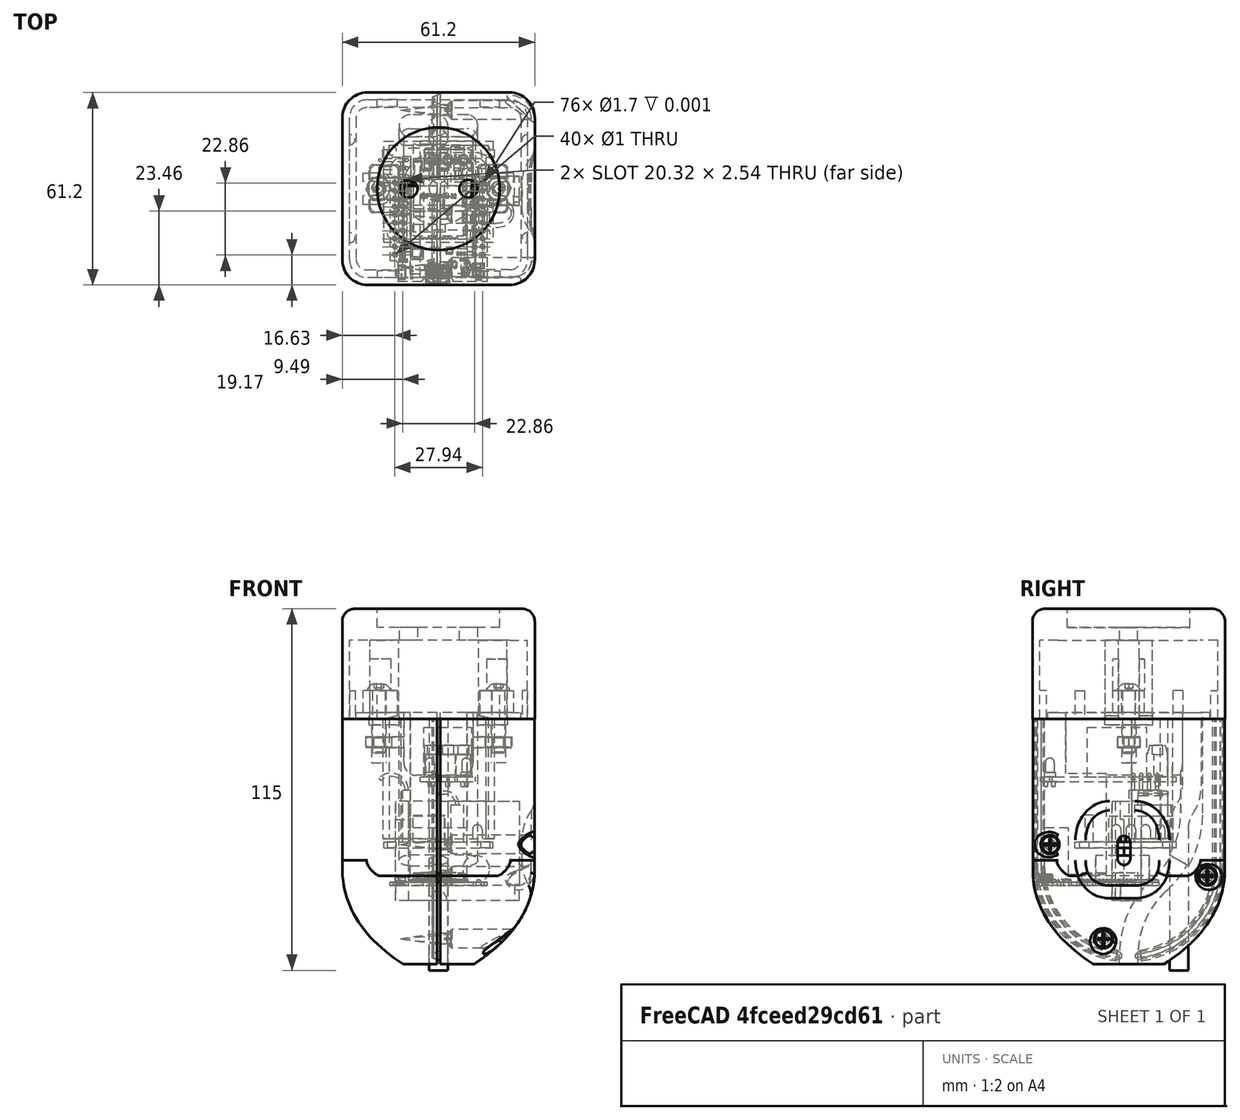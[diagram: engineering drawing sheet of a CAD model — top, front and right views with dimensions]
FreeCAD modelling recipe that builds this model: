
FCSTD DOCUMENT  (FreeCAD 1.0R39109 (Git))
Label: BedroomFan
License: All rights reserved
LicenseURL: http://en.wikipedia.org/wiki/All_rights_reserved
objects: Sketcher::SketchObject×104, PartDesign::Pocket×33, PartDesign::Body×22, PartDesign::Pad×17, PartDesign::Revolution×13, PartDesign::Groove×9, PartDesign::SubShapeBinder×9, PartDesign::Mirrored×8, PartDesign::SubtractivePipe×7, Part::Compound×5, PartDesign::Fillet×4, PartDesign::Plane×4, Part::FeaturePython×4, PartDesign::PolarPattern×3, PartDesign::AdditivePipe×3, PartDesign::SubtractiveLoft×2, PartDesign::LinearPattern×2, PartDesign::Point×2, Part::Feature×1, PartDesign::MultiTransform×1
note: 547 computed .brp shape members not serialized (recipe doc carries the construction recipe); baked Part::Feature solids carry a one-line shape summary decoded from their .brp

FEATURE [Part::Feature] Part__Feature  label="MH-ET_LIVE_MiniKit"
  shape: bbox 31.02 x 99.68 x 39.44 mm, 5494 faces, 23 solids (baked)
FEATURE [Sketcher::SketchObject] Sketch009
  ArcFitTolerance = 0
  AttachmentSupport = -> [XY_Plane001]
  FullyConstrained = true
  MakeInternals = false
  MapMode = 5
  sketch-geometry (8):
    g0: LineSegment StartX=0 StartY=8.8 StartZ=0 EndX=43.2 EndY=8.8 EndZ=0
    g1: LineSegment StartX=43.2 StartY=8.8 StartZ=0 EndX=43.2 EndY=-8.8 EndZ=0
    g2: LineSegment StartX=43.2 StartY=-8.8 StartZ=0 EndX=0 EndY=-8.8 EndZ=0
    g3: LineSegment StartX=0 StartY=-8.8 StartZ=0 EndX=0 EndY=8.8 EndZ=0
    g4: Circle CenterX=3.2 CenterY=2.54 CenterZ=0 NormalX=0 NormalY=0 NormalZ=1 AngleXU=0 Radius=0.4
    g5: Circle CenterX=3.2 CenterY=0 CenterZ=0 NormalX=0 NormalY=0 NormalZ=1 AngleXU=0 Radius=0.4
    g6: Circle CenterX=3.2 CenterY=-2.54 CenterZ=0 NormalX=0 NormalY=0 NormalZ=1 AngleXU=0 Radius=0.4
    g7: LineSegment [constr] StartX=3.2 StartY=2.54 StartZ=0 EndX=3.2 EndY=-2.54 EndZ=0
  constraints (21):
    c: Coincident(g0,g1)
    c: Coincident(g1,g2)
    c: Coincident(g2,g3)
    c: Coincident(g3,g0)
    c: Horizontal(g0)
    c: Horizontal(g2)
    c: Vertical(g3)
    c: PointOnObject(g0,g-2)
    c: Symmetric(g1,g0,g-1)
    c: DistanceY(g1,g1) = 17.6
    c: DistanceX(g0,g0) = 43.2
    c: PointOnObject(g5,g-1)
    c: Symmetric(g6,g4,g-1)
    c: Coincident(g7,g4)
    c: Coincident(g7,g6)
    c: PointOnObject(g5,g7)
    c: Equal(g6,g5)
    c: Equal(g5,g4)
    c: Radius(g4) = 0.4
    c: DistanceY(g7,g7) = 5.08
    c: DistanceX(g4) = 3.2
FEATURE [PartDesign::Pad] Pad006
  Direction = (0,0,1)
  Length = 1.6
  Length2 = 100
  Profile = -> Sketch009
  Suppressed = false
  Type = 0
FEATURE [PartDesign::Body] Body001  label="PCB"
  AllowCompound = false
  Group = -> [Sketch009,Pad006]
  Origin = -> Origin001
  Tip = -> Pad006
FEATURE [Sketcher::SketchObject] Sketch010
  ArcFitTolerance = 0
  AttachmentOffset = pos=(0,0,1.6) rot=(0,0,1;0rad)
  AttachmentSupport = -> [XY_Plane002]
  FullyConstrained = true
  MakeInternals = false
  MapMode = 5
  Placement = pos=(0,0,1.6) rot=(0,0,1;0rad)
  sketch-geometry (4):
    g0: LineSegment StartX=14.8 StartY=7.6 StartZ=0 EndX=33.8 EndY=7.6 EndZ=0
    g1: LineSegment StartX=33.8 StartY=7.6 StartZ=0 EndX=33.8 EndY=-7.6 EndZ=0
    g2: LineSegment StartX=33.8 StartY=-7.6 StartZ=0 EndX=14.8 EndY=-7.6 EndZ=0
    g3: LineSegment StartX=14.8 StartY=-7.6 StartZ=0 EndX=14.8 EndY=7.6 EndZ=0
  constraints (11):
    c: Coincident(g0,g1)
    c: Coincident(g1,g2)
    c: Coincident(g2,g3)
    c: Coincident(g3,g0)
    c: Horizontal(g0)
    c: Horizontal(g2)
    c: Vertical(g3)
    c: Symmetric(g1,g0,g-1)
    c: DistanceX(g0,g0) = 19
    c: DistanceY(g1,g1) = 15.2
    c: DistanceX(g0) = 14.8
FEATURE [PartDesign::Pad] Pad007
  Direction = (0,0,1)
  Length = 15.7
  Length2 = 100
  Profile = -> Sketch010
  Suppressed = false
  Type = 0
FEATURE [PartDesign::Body] Body002  label="JQC-3FF-S-Z"
  AllowCompound = false
  Group = -> [Sketch010,Pad007]
  Origin = -> Origin002
  Tip = -> Pad007
FEATURE [Sketcher::SketchObject] Sketch011
  ArcFitTolerance = 0
  AttachmentSupport = -> [XZ_Plane003]
  FullyConstrained = true
  MakeInternals = false
  MapMode = 5
  Placement = pos=(0,0,0) rot=(1,0,0;1.5708rad)
  sketch-geometry (7):
    g0: LineSegment StartX=34.6 StartY=11.6 StartZ=0 EndX=39.6 EndY=11.6 EndZ=0
    g1: LineSegment StartX=40.4 StartY=8.6 StartZ=0 EndX=40.4 EndY=1.6 EndZ=0
    g2: LineSegment StartX=40.4 StartY=1.6 StartZ=0 EndX=33.8 EndY=1.6 EndZ=0
    g3: LineSegment StartX=33.8 StartY=1.6 StartZ=0 EndX=33.8 EndY=8.6 EndZ=0
    g4: LineSegment StartX=34.6 StartY=11.6 StartZ=0 EndX=33.8 EndY=8.6 EndZ=0
    g5: LineSegment StartX=39.6 StartY=11.6 StartZ=0 EndX=40.4 EndY=8.6 EndZ=0
    g6: LineSegment [constr] StartX=37.1 StartY=11.6 StartZ=0 EndX=37.1 EndY=1.6 EndZ=0
  constraints (19):
    c: Coincident(g1,g2)
    c: Coincident(g2,g3)
    c: Horizontal(g0)
    c: Vertical(g1)
    c: DistanceY(g1) = 1.6
    c: Coincident(g3,g4)
    c: Coincident(g4,g0)
    c: Coincident(g0,g5)
    c: Coincident(g1,g5)
    c: PointOnObject(g6,g0)
    c: PointOnObject(g6,g2)
    c: Symmetric(g1,g2,g6)
    c: Symmetric(g1,g3,g6)
    c: Symmetric(g0,g0,g6)
    c: DistanceX(g2) = 33.8
    c: DistanceX(g0,g0) = 5
    c: DistanceY(g1,g0) = 10
    c: DistanceY(g1,g1) = 7
    c: DistanceX(g1) = 40.4
FEATURE [PartDesign::Pad] Pad008
  Direction = (0,-1,2e-16)
  Length = 15
  Length2 = 100
  Midplane = true
  Placement = pos=(0,0,0) rot=(1,0,0;1.5708rad)
  Profile = -> Sketch011
  Suppressed = false
  Type = 0
FEATURE [Sketcher::SketchObject] Sketch012
  ArcFitTolerance = 0
  AttachmentOffset = pos=(0,0,36) rot=(0,0,1;0rad)
  AttachmentSupport = -> [YZ_Plane003]
  FullyConstrained = true
  MakeInternals = false
  MapMode = 5
  Placement = pos=(36,0,0) rot=(0.57735,0.57735,0.57735;2.0944rad)
  sketch-geometry (16):
    g0: LineSegment StartX=-7.05 StartY=8.6 StartZ=0 EndX=-2.65 EndY=8.6 EndZ=0
    g1: LineSegment StartX=-2.65 StartY=8.6 StartZ=0 EndX=-2.65 EndY=2.1 EndZ=0
    g2: LineSegment StartX=-2.65 StartY=2.1 StartZ=0 EndX=-7.05 EndY=2.1 EndZ=0
    g3: LineSegment StartX=-7.05 StartY=2.1 StartZ=0 EndX=-7.05 EndY=8.6 EndZ=0
    g4: LineSegment [constr] StartX=-7.05 StartY=8.6 StartZ=0 EndX=-7.5 EndY=8.6 EndZ=0
    g5: LineSegment [constr] StartX=-2.2 StartY=8.6 StartZ=0 EndX=-2.65 EndY=8.6 EndZ=0
    g6: LineSegment StartX=-2.2 StartY=8.6 StartZ=0 EndX=2.2 EndY=8.6 EndZ=0
    g7: LineSegment StartX=2.2 StartY=8.6 StartZ=0 EndX=2.2 EndY=2.1 EndZ=0
    g8: LineSegment StartX=2.2 StartY=2.1 StartZ=0 EndX=-2.2 EndY=2.1 EndZ=0
    g9: LineSegment StartX=-2.2 StartY=2.1 StartZ=0 EndX=-2.2 EndY=8.6 EndZ=0
    g10: LineSegment StartX=2.65 StartY=8.6 StartZ=0 EndX=7.05 EndY=8.6 EndZ=0
    g11: LineSegment StartX=7.05 StartY=8.6 StartZ=0 EndX=7.05 EndY=2.1 EndZ=0
    g12: LineSegment StartX=7.05 StartY=2.1 StartZ=0 EndX=2.65 EndY=2.1 EndZ=0
    g13: LineSegment StartX=2.65 StartY=2.1 StartZ=0 EndX=2.65 EndY=8.6 EndZ=0
    g14: LineSegment [constr] StartX=2.65 StartY=8.6 StartZ=0 EndX=2.2 EndY=8.6 EndZ=0
    g15: LineSegment [constr] StartX=7.05 StartY=8.6 StartZ=0 EndX=7.5 EndY=8.6 EndZ=0
  constraints (45):
    c: Coincident(g0,g1)
    c: Coincident(g1,g2)
    c: Coincident(g2,g3)
    c: Coincident(g3,g0)
    c: Horizontal(g0)
    c: Horizontal(g2)
    c: Vertical(g1)
    c: Vertical(g3)
    c: DistanceX(g0,g0) = 4.4
    c: DistanceY(g0) = 8.6
    c: DistanceY(g3,g3) = 6.5
    c: Coincident(g4,g0)
    c: Horizontal(g4)
    c: Coincident(g5,g0)
    c: Equal(g5,g4)
    c: Horizontal(g5)
    c: Coincident(g6,g7)
    c: Coincident(g7,g8)
    c: Coincident(g8,g9)
    c: Coincident(g9,g6)
    c: Horizontal(g6)
    c: Horizontal(g8)
    c: Vertical(g7)
    c: Vertical(g9)
    c: Coincident(g6,g5)
    c: Coincident(g10,g11)
    c: Coincident(g11,g12)
    c: Coincident(g12,g13)
    c: Coincident(g13,g10)
    c: Horizontal(g10)
    c: Horizontal(g12)
    c: Vertical(g11)
    c: Vertical(g13)
    c: Coincident(g14,g10)
    c: Coincident(g14,g6)
    c: Horizontal(g14)
    c: Coincident(g15,g10)
    c: Equal(g15,g14)
    c: Equal(g14,g5)
    c: DistanceX(g4,g15) = 15
    c: Equal(g0,g6)
    c: Equal(g6,g10)
    c: Symmetric(g4,g15,g-2)
    c: Equal(g1,g9)
    c: Equal(g9,g13)
FEATURE [PartDesign::Pocket] Pocket
  BaseFeature = -> Pad008
  Direction = (-1,0,0)
  Length = 5
  Length2 = 100
  Placement = pos=(0,0,0) rot=(1,0,0;1.5708rad)
  Profile = -> Sketch012
  Reversed = true
  Suppressed = false
  Type = 1
FEATURE [Sketcher::SketchObject] Sketch013
  ArcFitTolerance = 0
  AttachmentOffset = pos=(0,0,8.6) rot=(0,0,1;0rad)
  AttachmentSupport = -> [XY_Plane003]
  ExternalGeometry = -> [Pocket]
  FullyConstrained = true
  MakeInternals = false
  MapMode = 5
  Placement = pos=(0,0,8.6) rot=(0,0,1;0rad)
  sketch-geometry (5):
    g0: Circle CenterX=37.1 CenterY=-4.85 CenterZ=0 NormalX=0 NormalY=0 NormalZ=1 AngleXU=0 Radius=1.75
    g1: LineSegment [constr] StartX=37.1 StartY=-2.65 StartZ=0 EndX=37.1 EndY=-7.05 EndZ=0
    g2: LineSegment [constr] StartX=38.85 StartY=-4.85 StartZ=0 EndX=35.35 EndY=-4.85 EndZ=0
    g3: Circle CenterX=37.1 CenterY=4.85 CenterZ=0 NormalX=0 NormalY=0 NormalZ=1 AngleXU=0 Radius=1.75
    g4: Circle CenterX=37.1 CenterY=0 CenterZ=0 NormalX=0 NormalY=0 NormalZ=1 AngleXU=0 Radius=1.75
  constraints (14):
    c: PointOnObject(g1,g-3)
    c: PointOnObject(g1,g-4)
    c: PointOnObject(g2,g0)
    c: PointOnObject(g2,g0)
    c: PointOnObject(g0,g1)
    c: PointOnObject(g0,g2)
    c: Symmetric(g-3,g-4,g2)
    c: Radius(g0) = 1.75
    c: Symmetric(g-5,g-6,g1)
    c: PointOnObject(g4,g-1)
    c: Symmetric(g3,g0,g-1)
    c: PointOnObject(g4,g1)
    c: Equal(g0,g4)
    c: Equal(g4,g3)
FEATURE [PartDesign::Pocket] Pocket001
  BaseFeature = -> Pocket
  Direction = (0,0,-1)
  Length = 5
  Length2 = 100
  Placement = pos=(0,0,0) rot=(1,0,0;1.5708rad)
  Profile = -> Sketch013
  Reversed = true
  Suppressed = false
  Type = 1
FEATURE [PartDesign::Body] Body003  label="Connectors"
  AllowCompound = false
  Group = -> [Sketch011,Pad008,Sketch012,Pocket,Sketch013,Pocket001]
  Origin = -> Origin003
  Tip = -> Pocket001
FEATURE [Sketcher::SketchObject] Sketch014
  ArcFitTolerance = 0
  AttachmentOffset = pos=(0,0,2.9) rot=(0,0,1;0rad)
  AttachmentSupport = -> [YZ_Plane004]
  FullyConstrained = true
  MakeInternals = false
  MapMode = 5
  Placement = pos=(2.9,0,0) rot=(0.57735,0.57735,0.57735;2.0944rad)
  sketch-geometry (6):
    g0: ArcOfCircle CenterX=0 CenterY=6.05 CenterZ=0 NormalX=0 NormalY=0 NormalZ=1 AngleXU=0 Radius=1.45 StartAngle=1.5708 EndAngle=3.14159
    g1: LineSegment StartX=-1.45 StartY=6.05 StartZ=0 EndX=-1.45 EndY=3 EndZ=0
    g2: LineSegment StartX=-1.45 StartY=3 StartZ=0 EndX=-1.75 EndY=3 EndZ=0
    g3: LineSegment StartX=-1.75 StartY=3 StartZ=0 EndX=-1.75 EndY=1.6 EndZ=0
    g4: LineSegment StartX=-1.75 StartY=1.6 StartZ=0 EndX=0 EndY=1.6 EndZ=0
    g5: LineSegment StartX=0 StartY=1.6 StartZ=0 EndX=0 EndY=7.5 EndZ=0
  constraints (18):
    c: Vertical(g1)
    c: Coincident(g1,g2)
    c: Coincident(g2,g3)
    c: Coincident(g3,g4)
    c: Horizontal(g4)
    c: Coincident(g4,g5)
    c: Coincident(g5,g0)
    c: Vertical(g5)
    c: Tangent(g0,g1) = -1.5708
    c: PointOnObject(g0,g5)
    c: Horizontal(g2)
    c: Vertical(g3)
    c: DistanceY(g3) = 1.6
    c: DistanceY(g0) = 7.5
    c: DistanceX(g0,g0) = 1.45
    c: DistanceX(g4,g4) = 1.75
    c: DistanceY(g2) = 3
    c: PointOnObject(g4,g-2)
FEATURE [PartDesign::Revolution] Revolution001
  Angle = 360
  Angle2 = 60
  Axis = (0,0,1)
  Base = (2.9,0,0)
  Placement = pos=(0,0,0) rot=(0.57735,0.57735,0.57735;2.0944rad)
  Profile = -> Sketch014
  ReferenceAxis = -> Sketch014 [V_Axis]
  Suppressed = false
  Type = 0
FEATURE [PartDesign::Body] Body004  label="LEDgreen"
  AllowCompound = false
  Group = -> [Sketch014,Revolution001]
  Origin = -> Origin004
  Placement = pos=(0,5.8,0) rot=(0,0,1;0rad)
  Tip = -> Revolution001
FEATURE [Sketcher::SketchObject] Sketch015
  ArcFitTolerance = 0
  AttachmentOffset = pos=(0,0,2.9) rot=(0,0,1;0rad)
  AttachmentSupport = -> [YZ_Plane004]
  FullyConstrained = true
  MakeInternals = false
  MapMode = 5
  Placement = pos=(2.9,0,0) rot=(0.57735,0.57735,0.57735;2.0944rad)
  sketch-geometry (6):
    g0: ArcOfCircle CenterX=0 CenterY=6.05 CenterZ=0 NormalX=0 NormalY=0 NormalZ=1 AngleXU=0 Radius=1.45 StartAngle=1.5708 EndAngle=3.14159
    g1: LineSegment StartX=-1.45 StartY=6.05 StartZ=0 EndX=-1.45 EndY=3 EndZ=0
    g2: LineSegment StartX=-1.45 StartY=3 StartZ=0 EndX=-1.75 EndY=3 EndZ=0
    g3: LineSegment StartX=-1.75 StartY=3 StartZ=0 EndX=-1.75 EndY=1.6 EndZ=0
    g4: LineSegment StartX=-1.75 StartY=1.6 StartZ=0 EndX=0 EndY=1.6 EndZ=0
    g5: LineSegment StartX=1e-16 StartY=1.6 StartZ=0 EndX=1e-16 EndY=7.5 EndZ=0
  constraints (18):
    c: Vertical(g1)
    c: Coincident(g1,g2)
    c: Coincident(g2,g3)
    c: Coincident(g3,g4)
    c: Horizontal(g4)
    c: Coincident(g4,g5)
    c: Coincident(g5,g0)
    c: Vertical(g5)
    c: Tangent(g0,g1) = -1.5708
    c: PointOnObject(g0,g5)
    c: Horizontal(g2)
    c: Vertical(g3)
    c: DistanceY(g3) = 1.6
    c: DistanceY(g0) = 7.5
    c: DistanceX(g0,g0) = 1.45
    c: DistanceX(g4,g4) = 1.75
    c: DistanceY(g2) = 3
    c: PointOnObject(g4,g-2)
FEATURE [PartDesign::Revolution] Revolution002
  Angle = 360
  Angle2 = 60
  Axis = (0,0,1)
  Base = (2.9,0,0)
  Placement = pos=(0,0,0) rot=(0.57735,0.57735,0.57735;2.0944rad)
  Profile = -> Sketch015
  ReferenceAxis = -> Sketch015 [V_Axis]
  Suppressed = false
  Type = 0
FEATURE [PartDesign::Body] Body005  label="LEDred"
  AllowCompound = false
  Group = -> [Sketch015,Revolution002]
  Origin = -> Origin005
  Placement = pos=(0,-5.8,0) rot=(0,0,1;0rad)
  Tip = -> Revolution002
FEATURE [Sketcher::SketchObject] Sketch016
  ArcFitTolerance = 0
  AttachmentSupport = -> [YZ_Plane006]
  FullyConstrained = true
  MakeInternals = false
  MapMode = 5
  Placement = pos=(0,0,0) rot=(0.57735,0.57735,0.57735;2.0944rad)
  sketch-geometry (5):
    g0: LineSegment StartX=1.2 StartY=0 StartZ=0 EndX=0 EndY=0 EndZ=0
    g1: LineSegment StartX=0 StartY=0 StartZ=0 EndX=0 EndY=-1.5 EndZ=0
    g2: LineSegment StartX=0 StartY=-1.5 StartZ=0 EndX=0.6 EndY=-1.5 EndZ=0
    g3: LineSegment StartX=0.6 StartY=-1.5 StartZ=0 EndX=0.6 EndY=-0.6 EndZ=0
    g4: ArcOfCircle CenterX=1.2 CenterY=-0.6 CenterZ=0 NormalX=0 NormalY=0 NormalZ=1 AngleXU=0 Radius=0.6 StartAngle=1.5708 EndAngle=3.14159
  constraints (13):
    c: PointOnObject(g0,g-1)
    c: Coincident(g0,g-1)
    c: Coincident(g0,g1)
    c: PointOnObject(g1,g-2)
    c: Coincident(g1,g2)
    c: Horizontal(g2)
    c: Coincident(g2,g3)
    c: Vertical(g3)
    c: Tangent(g0,g4) = -1.5708
    c: Tangent(g3,g4) = 1.5708
    c: DistanceX(g2,g2) = 0.6
    c: DistanceY(g1,g1) = 1.5
    c: Radius(g4) = 0.6
FEATURE [PartDesign::Revolution] Revolution003
  Angle = 360
  Angle2 = 60
  Axis = (0,0,1)
  Base = (0,0,0)
  Placement = pos=(0,0,0) rot=(0.57735,0.57735,0.57735;2.0944rad)
  Profile = -> Sketch016
  ReferenceAxis = -> Sketch016 [V_Axis]
  Reversed = true
  Suppressed = false
  Type = 0
FEATURE [PartDesign::Body] Body006  label="Pin001"
  AllowCompound = false
  Group = -> [Sketch016,Revolution003]
  Origin = -> Origin006
  Placement = pos=(1.7,5.7,0) rot=(0,0,1;0rad)
  Tip = -> Revolution003
FEATURE [Sketcher::SketchObject] Sketch017
  ArcFitTolerance = 0
  AttachmentSupport = -> [YZ_Plane006]
  FullyConstrained = true
  MakeInternals = false
  MapMode = 5
  Placement = pos=(0,0,0) rot=(0.57735,0.57735,0.57735;2.0944rad)
  sketch-geometry (5):
    g0: LineSegment StartX=1.2 StartY=0 StartZ=0 EndX=0 EndY=0 EndZ=0
    g1: LineSegment StartX=0 StartY=0 StartZ=0 EndX=0 EndY=-1.5 EndZ=0
    g2: LineSegment StartX=0 StartY=-1.5 StartZ=0 EndX=0.6 EndY=-1.5 EndZ=0
    g3: LineSegment StartX=0.6 StartY=-1.5 StartZ=0 EndX=0.6 EndY=-0.6 EndZ=0
    g4: ArcOfCircle CenterX=1.2 CenterY=-0.6 CenterZ=0 NormalX=0 NormalY=0 NormalZ=1 AngleXU=0 Radius=0.6 StartAngle=1.5708 EndAngle=3.14159
  constraints (13):
    c: PointOnObject(g0,g-1)
    c: Coincident(g0,g-1)
    c: Coincident(g0,g1)
    c: PointOnObject(g1,g-2)
    c: Coincident(g1,g2)
    c: Horizontal(g2)
    c: Coincident(g2,g3)
    c: Vertical(g3)
    c: Tangent(g0,g4) = -1.5708
    c: Tangent(g3,g4) = 1.5708
    c: DistanceX(g2,g2) = 0.6
    c: DistanceY(g1,g1) = 1.5
    c: Radius(g4) = 0.6
FEATURE [PartDesign::Revolution] Revolution004
  Angle = 360
  Angle2 = 60
  Axis = (0,0,1)
  Base = (0,0,0)
  Placement = pos=(0,0,0) rot=(0.57735,0.57735,0.57735;2.0944rad)
  Profile = -> Sketch017
  ReferenceAxis = -> Sketch017 [V_Axis]
  Reversed = true
  Suppressed = false
  Type = 0
FEATURE [PartDesign::Body] Body007  label="Pin002"
  AllowCompound = false
  Group = -> [Sketch017,Revolution004]
  Origin = -> Origin007
  Placement = pos=(4.1,5.7,0) rot=(0,0,1;0rad)
  Tip = -> Revolution004
FEATURE [Sketcher::SketchObject] Sketch018
  ArcFitTolerance = 0
  AttachmentSupport = -> [YZ_Plane006]
  FullyConstrained = true
  MakeInternals = false
  MapMode = 5
  Placement = pos=(0,0,0) rot=(0.57735,0.57735,0.57735;2.0944rad)
  sketch-geometry (5):
    g0: LineSegment StartX=1.2 StartY=0 StartZ=0 EndX=0 EndY=0 EndZ=0
    g1: LineSegment StartX=0 StartY=0 StartZ=0 EndX=0 EndY=-1.5 EndZ=0
    g2: LineSegment StartX=0 StartY=-1.5 StartZ=0 EndX=0.6 EndY=-1.5 EndZ=0
    g3: LineSegment StartX=0.6 StartY=-1.5 StartZ=0 EndX=0.6 EndY=-0.6 EndZ=0
    g4: ArcOfCircle CenterX=1.2 CenterY=-0.6 CenterZ=0 NormalX=0 NormalY=0 NormalZ=1 AngleXU=0 Radius=0.6 StartAngle=1.5708 EndAngle=3.14159
  constraints (13):
    c: PointOnObject(g0,g-1)
    c: Coincident(g0,g-1)
    c: Coincident(g0,g1)
    c: PointOnObject(g1,g-2)
    c: Coincident(g1,g2)
    c: Horizontal(g2)
    c: Coincident(g2,g3)
    c: Vertical(g3)
    c: Tangent(g0,g4) = -1.5708
    c: Tangent(g3,g4) = 1.5708
    c: DistanceX(g2,g2) = 0.6
    c: DistanceY(g1,g1) = 1.5
    c: Radius(g4) = 0.6
FEATURE [PartDesign::Revolution] Revolution005
  Angle = 360
  Angle2 = 60
  Axis = (0,0,1)
  Base = (0,0,0)
  Placement = pos=(0,0,0) rot=(0.57735,0.57735,0.57735;2.0944rad)
  Profile = -> Sketch018
  ReferenceAxis = -> Sketch018 [V_Axis]
  Reversed = true
  Suppressed = false
  Type = 0
FEATURE [PartDesign::Body] Body008  label="Pin003"
  AllowCompound = false
  Group = -> [Sketch018,Revolution005]
  Origin = -> Origin008
  Placement = pos=(4.1,-5.9,0) rot=(0,0,1;0rad)
  Tip = -> Revolution005
FEATURE [Sketcher::SketchObject] Sketch019
  ArcFitTolerance = 0
  AttachmentSupport = -> [YZ_Plane006]
  FullyConstrained = true
  MakeInternals = false
  MapMode = 5
  Placement = pos=(0,0,0) rot=(0.57735,0.57735,0.57735;2.0944rad)
  sketch-geometry (5):
    g0: LineSegment StartX=1.2 StartY=0 StartZ=0 EndX=0 EndY=0 EndZ=0
    g1: LineSegment StartX=0 StartY=0 StartZ=0 EndX=0 EndY=-1.5 EndZ=0
    g2: LineSegment StartX=0 StartY=-1.5 StartZ=0 EndX=0.6 EndY=-1.5 EndZ=0
    g3: LineSegment StartX=0.6 StartY=-1.5 StartZ=0 EndX=0.6 EndY=-0.6 EndZ=0
    g4: ArcOfCircle CenterX=1.2 CenterY=-0.6 CenterZ=0 NormalX=0 NormalY=0 NormalZ=1 AngleXU=0 Radius=0.6 StartAngle=1.5708 EndAngle=3.14159
  constraints (13):
    c: PointOnObject(g0,g-1)
    c: Coincident(g0,g-1)
    c: Coincident(g0,g1)
    c: PointOnObject(g1,g-2)
    c: Coincident(g1,g2)
    c: Horizontal(g2)
    c: Coincident(g2,g3)
    c: Vertical(g3)
    c: Tangent(g0,g4) = -1.5708
    c: Tangent(g3,g4) = 1.5708
    c: DistanceX(g2,g2) = 0.6
    c: DistanceY(g1,g1) = 1.5
    c: Radius(g4) = 0.6
FEATURE [PartDesign::Revolution] Revolution006
  Angle = 360
  Angle2 = 60
  Axis = (0,0,1)
  Base = (0,0,0)
  Placement = pos=(0,0,0) rot=(0.57735,0.57735,0.57735;2.0944rad)
  Profile = -> Sketch019
  ReferenceAxis = -> Sketch019 [V_Axis]
  Reversed = true
  Suppressed = false
  Type = 0
FEATURE [PartDesign::Body] Body009  label="Pin004"
  AllowCompound = false
  Group = -> [Sketch019,Revolution006]
  Origin = -> Origin009
  Placement = pos=(1.7,-5.9,0) rot=(0,0,1;0rad)
  Tip = -> Revolution006
FEATURE [Sketcher::SketchObject] Sketch020
  ArcFitTolerance = 0
  AttachmentSupport = -> [YZ_Plane006]
  FullyConstrained = true
  MakeInternals = false
  MapMode = 5
  Placement = pos=(0,0,0) rot=(0.57735,0.57735,0.57735;2.0944rad)
  sketch-geometry (5):
    g0: LineSegment StartX=1.2 StartY=0 StartZ=0 EndX=0 EndY=0 EndZ=0
    g1: LineSegment StartX=0 StartY=0 StartZ=0 EndX=0 EndY=-1.5 EndZ=0
    g2: LineSegment StartX=0 StartY=-1.5 StartZ=0 EndX=0.6 EndY=-1.5 EndZ=0
    g3: LineSegment StartX=0.6 StartY=-1.5 StartZ=0 EndX=0.6 EndY=-0.6 EndZ=0
    g4: ArcOfCircle CenterX=1.2 CenterY=-0.6 CenterZ=0 NormalX=0 NormalY=0 NormalZ=1 AngleXU=0 Radius=0.6 StartAngle=1.5708 EndAngle=3.14159
  constraints (13):
    c: PointOnObject(g0,g-1)
    c: Coincident(g0,g-1)
    c: Coincident(g0,g1)
    c: PointOnObject(g1,g-2)
    c: Coincident(g1,g2)
    c: Horizontal(g2)
    c: Coincident(g2,g3)
    c: Vertical(g3)
    c: Tangent(g0,g4) = -1.5708
    c: Tangent(g3,g4) = 1.5708
    c: DistanceX(g2,g2) = 0.6
    c: DistanceY(g1,g1) = 1.5
    c: Radius(g4) = 0.6
FEATURE [PartDesign::Revolution] Revolution007
  Angle = 360
  Angle2 = 60
  Axis = (0,0,1)
  Base = (0,0,0)
  Placement = pos=(0,0,0) rot=(0.57735,0.57735,0.57735;2.0944rad)
  Profile = -> Sketch020
  ReferenceAxis = -> Sketch020 [V_Axis]
  Reversed = true
  Suppressed = false
  Type = 0
FEATURE [PartDesign::Body] Body010  label="Pin005"
  AllowCompound = false
  Group = -> [Sketch020,Revolution007]
  Origin = -> Origin010
  Placement = pos=(37.1,-4.8,0) rot=(0,0,1;0rad)
  Tip = -> Revolution007
FEATURE [Sketcher::SketchObject] Sketch021
  ArcFitTolerance = 0
  AttachmentSupport = -> [YZ_Plane006]
  FullyConstrained = true
  MakeInternals = false
  MapMode = 5
  Placement = pos=(0,0,0) rot=(0.57735,0.57735,0.57735;2.0944rad)
  sketch-geometry (5):
    g0: LineSegment StartX=1.2 StartY=0 StartZ=0 EndX=0 EndY=0 EndZ=0
    g1: LineSegment StartX=0 StartY=0 StartZ=0 EndX=0 EndY=-1.5 EndZ=0
    g2: LineSegment StartX=0 StartY=-1.5 StartZ=0 EndX=0.6 EndY=-1.5 EndZ=0
    g3: LineSegment StartX=0.6 StartY=-1.5 StartZ=0 EndX=0.6 EndY=-0.6 EndZ=0
    g4: ArcOfCircle CenterX=1.2 CenterY=-0.6 CenterZ=0 NormalX=0 NormalY=0 NormalZ=1 AngleXU=0 Radius=0.6 StartAngle=1.5708 EndAngle=3.14159
  constraints (13):
    c: PointOnObject(g0,g-1)
    c: Coincident(g0,g-1)
    c: Coincident(g0,g1)
    c: PointOnObject(g1,g-2)
    c: Coincident(g1,g2)
    c: Horizontal(g2)
    c: Coincident(g2,g3)
    c: Vertical(g3)
    c: Tangent(g0,g4) = -1.5708
    c: Tangent(g3,g4) = 1.5708
    c: DistanceX(g2,g2) = 0.6
    c: DistanceY(g1,g1) = 1.5
    c: Radius(g4) = 0.6
FEATURE [PartDesign::Revolution] Revolution008
  Angle = 360
  Angle2 = 60
  Axis = (0,0,1)
  Base = (0,0,0)
  Placement = pos=(0,0,0) rot=(0.57735,0.57735,0.57735;2.0944rad)
  Profile = -> Sketch021
  ReferenceAxis = -> Sketch021 [V_Axis]
  Reversed = true
  Suppressed = false
  Type = 0
FEATURE [PartDesign::Body] Body011  label="Pin006"
  AllowCompound = false
  Group = -> [Sketch021,Revolution008]
  Origin = -> Origin011
  Placement = pos=(37.1,9e-16,0) rot=(0,0,1;0rad)
  Tip = -> Revolution008
FEATURE [Sketcher::SketchObject] Sketch022
  ArcFitTolerance = 0
  AttachmentSupport = -> [YZ_Plane006]
  FullyConstrained = true
  MakeInternals = false
  MapMode = 5
  Placement = pos=(0,0,0) rot=(0.57735,0.57735,0.57735;2.0944rad)
  sketch-geometry (5):
    g0: LineSegment StartX=1.2 StartY=0 StartZ=0 EndX=0 EndY=0 EndZ=0
    g1: LineSegment StartX=0 StartY=0 StartZ=0 EndX=0 EndY=-1.5 EndZ=0
    g2: LineSegment StartX=0 StartY=-1.5 StartZ=0 EndX=0.6 EndY=-1.5 EndZ=0
    g3: LineSegment StartX=0.6 StartY=-1.5 StartZ=0 EndX=0.6 EndY=-0.6 EndZ=0
    g4: ArcOfCircle CenterX=1.2 CenterY=-0.6 CenterZ=0 NormalX=0 NormalY=0 NormalZ=1 AngleXU=0 Radius=0.6 StartAngle=1.5708 EndAngle=3.14159
  constraints (13):
    c: PointOnObject(g0,g-1)
    c: Coincident(g0,g-1)
    c: Coincident(g0,g1)
    c: PointOnObject(g1,g-2)
    c: Coincident(g1,g2)
    c: Horizontal(g2)
    c: Coincident(g2,g3)
    c: Vertical(g3)
    c: Tangent(g0,g4) = -1.5708
    c: Tangent(g3,g4) = 1.5708
    c: DistanceX(g2,g2) = 0.6
    c: DistanceY(g1,g1) = 1.5
    c: Radius(g4) = 0.6
FEATURE [PartDesign::Revolution] Revolution009
  Angle = 360
  Angle2 = 60
  Axis = (0,0,1)
  Base = (0,0,0)
  Placement = pos=(0,0,0) rot=(0.57735,0.57735,0.57735;2.0944rad)
  Profile = -> Sketch022
  ReferenceAxis = -> Sketch022 [V_Axis]
  Reversed = true
  Suppressed = false
  Type = 0
FEATURE [PartDesign::Body] Body012  label="Pin007"
  AllowCompound = false
  Group = -> [Sketch022,Revolution009]
  Origin = -> Origin012
  Placement = pos=(37.1,4.8,0) rot=(0,0,1;0rad)
  Tip = -> Revolution009
FEATURE [Part::Compound] Compound  label="Relay JQC-3FF-S-Z"
  Links = -> [Body001,Body002,Body003,Body004,Body005,Body006,Body007,Body008,Body009,Body010,Body011,Body012]
  Placement = pos=(3,-28,-20) rot=(0,0,1;1.5708rad)
FEATURE [Sketcher::SketchObject] Sketch023
  ArcFitTolerance = 0
  AttachmentSupport = -> [XY_Plane013]
  FullyConstrained = true
  MakeInternals = false
  MapMode = 5
  sketch-geometry (12):
    g0: LineSegment StartX=-22.6 StartY=30.6 StartZ=0 EndX=22.6 EndY=30.6 EndZ=0
    g1: LineSegment StartX=30.6 StartY=22.6 StartZ=0 EndX=30.6 EndY=-22.6 EndZ=0
    g2: LineSegment StartX=22.6 StartY=-30.6 StartZ=0 EndX=-22.6 EndY=-30.6 EndZ=0
    g3: LineSegment StartX=-30.6 StartY=-22.6 StartZ=0 EndX=-30.6 EndY=22.6 EndZ=0
    g4: ArcOfCircle CenterX=-22.6 CenterY=22.6 CenterZ=0 NormalX=0 NormalY=0 NormalZ=1 AngleXU=0 Radius=8 StartAngle=1.5708 EndAngle=3.14159
    g5: ArcOfCircle CenterX=22.6 CenterY=22.6 CenterZ=0 NormalX=0 NormalY=0 NormalZ=1 AngleXU=0 Radius=8 StartAngle=2.39e-14 EndAngle=1.5708
    g6: ArcOfCircle CenterX=22.6 CenterY=-22.6 CenterZ=0 NormalX=0 NormalY=0 NormalZ=1 AngleXU=0 Radius=8 StartAngle=4.71239 EndAngle=6.28319
    g7: ArcOfCircle CenterX=-22.6 CenterY=-22.6 CenterZ=0 NormalX=0 NormalY=0 NormalZ=1 AngleXU=0 Radius=8 StartAngle=3.14159 EndAngle=4.71239
    g8: LineSegment [constr] StartX=-22.6 StartY=22.6 StartZ=0 EndX=22.6 EndY=22.6 EndZ=0
    g9: LineSegment [constr] StartX=22.6 StartY=22.6 StartZ=0 EndX=22.6 EndY=-22.6 EndZ=0
    g10: LineSegment [constr] StartX=22.6 StartY=-22.6 StartZ=0 EndX=-22.6 EndY=-22.6 EndZ=0
    g11: LineSegment [constr] StartX=-22.6 StartY=-22.6 StartZ=0 EndX=-22.6 EndY=22.6 EndZ=0
  constraints (26):
    c: Horizontal(g0)
    c: Horizontal(g2)
    c: Vertical(g1)
    c: Vertical(g3)
    c: Tangent(g3,g4) = 1.5708
    c: Tangent(g0,g4) = 1.5708
    c: Tangent(g0,g5) = 1.5708
    c: Tangent(g1,g5) = 1.5708
    c: Tangent(g1,g6) = 1.5708
    c: Tangent(g2,g6) = 1.5708
    c: Tangent(g2,g7) = 1.5708
    c: Tangent(g3,g7) = 1.5708
    c: Coincident(g8,g9)
    c: Coincident(g9,g10)
    c: Coincident(g10,g11)
    c: Coincident(g11,g8)
    c: Horizontal(g10)
    c: Coincident(g8,g4)
    c: Coincident(g9,g6)
    c: Coincident(g5,g8)
    c: Coincident(g7,g10)
    c: Symmetric(g5,g6,g-1)
    c: Symmetric(g5,g4,g-2)
    c: Equal(g9,g8)
    c: DistanceX(g3,g1) = 61.2
    c: Radius(g5) = 8
FEATURE [PartDesign::Pad] Pad009
  Direction = (0,0,1)
  Length = 35
  Length2 = 100
  Profile = -> Sketch023
  Suppressed = false
  Type = 0
FEATURE [Sketcher::SketchObject] Sketch024
  ArcFitTolerance = 0
  AttachmentSupport = -> [XY_Plane013]
  ExternalGeometry = -> [Sketch023]
  FullyConstrained = true
  MakeInternals = false
  MapMode = 5
  sketch-geometry (12):
    g0: LineSegment [constr] StartX=22.6 StartY=22.6 StartZ=0 EndX=-22.6 EndY=22.6 EndZ=0
    g1: LineSegment [constr] StartX=-22.6 StartY=22.6 StartZ=0 EndX=-22.6 EndY=-22.6 EndZ=0
    g2: LineSegment [constr] StartX=-22.6 StartY=-22.6 StartZ=0 EndX=22.6 EndY=-22.6 EndZ=0
    g3: LineSegment [constr] StartX=22.6 StartY=-22.6 StartZ=0 EndX=22.6 EndY=22.6 EndZ=0
    g4: LineSegment StartX=-22.6 StartY=28.3 StartZ=0 EndX=22.6 EndY=28.3 EndZ=0
    g5: LineSegment StartX=28.3 StartY=22.6 StartZ=0 EndX=28.3 EndY=-22.6 EndZ=0
    g6: LineSegment StartX=22.6 StartY=-28.3 StartZ=0 EndX=-22.6 EndY=-28.3 EndZ=0
    g7: LineSegment StartX=-28.3 StartY=-22.6 StartZ=0 EndX=-28.3 EndY=22.6 EndZ=0
    g8: ArcOfCircle CenterX=22.6 CenterY=22.6 CenterZ=0 NormalX=0 NormalY=0 NormalZ=1 AngleXU=0 Radius=5.7 StartAngle=0 EndAngle=1.5708
    g9: ArcOfCircle CenterX=-22.6 CenterY=22.6 CenterZ=0 NormalX=0 NormalY=0 NormalZ=1 AngleXU=0 Radius=5.7 StartAngle=1.5708 EndAngle=3.14159
    g10: ArcOfCircle CenterX=-22.6 CenterY=-22.6 CenterZ=0 NormalX=0 NormalY=0 NormalZ=1 AngleXU=0 Radius=5.7 StartAngle=3.14159 EndAngle=4.71239
    g11: ArcOfCircle CenterX=22.6 CenterY=-22.6 CenterZ=0 NormalX=0 NormalY=0 NormalZ=1 AngleXU=0 Radius=5.7 StartAngle=4.71239 EndAngle=6.28319
  constraints (25):
    c: Coincident(g0,g1)
    c: Coincident(g1,g2)
    c: Coincident(g2,g3)
    c: Coincident(g3,g0)
    c: Horizontal(g2)
    c: Vertical(g1)
    c: Coincident(g0,g-3)
    c: Symmetric(g0,g2,g-1)
    c: Symmetric(g0,g0,g-2)
    c: Horizontal(g4)
    c: Horizontal(g6)
    c: Vertical(g5)
    c: Tangent(g5,g8) = 1.5708
    c: Tangent(g4,g8) = 1.5708
    c: Tangent(g4,g9) = 1.5708
    c: Tangent(g7,g9) = 1.5708
    c: Tangent(g7,g10) = 1.5708
    c: Tangent(g6,g10) = 1.5708
    c: Tangent(g6,g11) = 1.5708
    c: Tangent(g5,g11) = 1.5708
    c: Coincident(g0,g8)
    c: Coincident(g0,g9)
    c: Coincident(g1,g10)
    c: Coincident(g2,g11)
    c: DistanceX(g5,g-3) = 2.3
FEATURE [PartDesign::Pocket] Pocket002
  BaseFeature = -> Pad009
  Direction = (0,0,-1)
  Length = 25
  Length2 = 100
  Profile = -> Sketch024
  Reversed = true
  Suppressed = false
  Type = 0
FEATURE [Sketcher::SketchObject] Sketch025
  ArcFitTolerance = 0
  AttachmentSupport = -> [XY_Plane013]
  FullyConstrained = true
  MakeInternals = false
  MapMode = 5
  sketch-geometry (4):
    g0: LineSegment StartX=19.5 StartY=28.6 StartZ=0 EndX=13.1 EndY=28.6 EndZ=0
    g1: LineSegment StartX=13.1 StartY=28.6 StartZ=0 EndX=13.1 EndY=26.1 EndZ=0
    g2: LineSegment StartX=13.1 StartY=26.1 StartZ=0 EndX=19.5 EndY=26.1 EndZ=0
    g3: LineSegment StartX=19.5 StartY=26.1 StartZ=0 EndX=19.5 EndY=28.6 EndZ=0
  constraints (12):
    c: Coincident(g0,g1)
    c: Coincident(g1,g2)
    c: Coincident(g2,g3)
    c: Coincident(g3,g0)
    c: Horizontal(g0)
    c: Horizontal(g2)
    c: Vertical(g1)
    c: Vertical(g3)
    c: DistanceX(g2) = 19.5
    c: DistanceX(g2,g2) = 6.4
    c: DistanceY(g2) = 26.1
    c: DistanceY(g3,g3) = 2.5
FEATURE [PartDesign::Pad] Pad010
  BaseFeature = -> Pocket002
  Direction = (0,0,1)
  Length = 9
  Length2 = 100
  Profile = -> Sketch025
  Suppressed = false
  Type = 0
FEATURE [Sketcher::SketchObject] Sketch026
  ArcFitTolerance = 0
  AttachmentSupport = -> [XY_Plane013]
  FullyConstrained = true
  MakeInternals = false
  MapMode = 5
  sketch-geometry (2):
    g0: Circle CenterX=28.1 CenterY=15.6 CenterZ=0 NormalX=0 NormalY=0 NormalZ=1 AngleXU=0 Radius=1.55
    g1: LineSegment [constr] StartX=28.1 StartY=15.6 StartZ=0 EndX=26.55 EndY=15.6 EndZ=0
  constraints (6):
    c: Radius(g0) = 1.55
    c: Coincident(g1,g0)
    c: PointOnObject(g1,g0)
    c: Horizontal(g1)
    c: DistanceX(g1) = 26.55
    c: DistanceY(g0) = 15.6
FEATURE [PartDesign::Pad] Pad011
  BaseFeature = -> Pad010
  Direction = (0,0,1)
  Length = 9
  Length2 = 100
  Profile = -> Sketch026
  Suppressed = false
  Type = 0
FEATURE [Sketcher::SketchObject] Sketch027
  ArcFitTolerance = 0
  AttachmentSupport = -> [XY_Plane013]
  FullyConstrained = true
  MakeInternals = false
  MapMode = 5
  sketch-geometry (6):
    g0: LineSegment StartX=21.8 StartY=3.3 StartZ=0 EndX=12.7 EndY=3.3 EndZ=0
    g1: LineSegment StartX=12.7 StartY=3.3 StartZ=0 EndX=12.7 EndY=5.5 EndZ=0
    g2: LineSegment StartX=14.7 StartY=7.5 StartZ=0 EndX=19.8 EndY=7.5 EndZ=0
    g3: LineSegment StartX=21.8 StartY=5.5 StartZ=0 EndX=21.8 EndY=3.3 EndZ=0
    g4: ArcOfCircle CenterX=19.8 CenterY=5.5 CenterZ=0 NormalX=0 NormalY=0 NormalZ=1 AngleXU=0 Radius=2 StartAngle=6.77e-14 EndAngle=1.5708
    g5: ArcOfCircle CenterX=14.7 CenterY=5.5 CenterZ=0 NormalX=0 NormalY=0 NormalZ=1 AngleXU=0 Radius=2 StartAngle=1.5708 EndAngle=3.14159
  constraints (16):
    c: Coincident(g0,g1)
    c: Coincident(g3,g0)
    c: Horizontal(g0)
    c: Horizontal(g2)
    c: Vertical(g1)
    c: Vertical(g3)
    c: Tangent(g3,g4) = 1.5708
    c: Tangent(g2,g4) = 1.5708
    c: Tangent(g2,g5) = 1.5708
    c: Tangent(g1,g5) = 1.5708
    c: DistanceX(g0,g0) = 9.1
    c: DistanceY(g0,g2) = 4.2
    c: DistanceY(g0) = 3.3
    c: DistanceX(g3) = 21.8
    c: Equal(g5,g4)
    c: Radius(g4) = 2
FEATURE [PartDesign::Pad] Pad012
  BaseFeature = -> Pad011
  Direction = (0,0,1)
  Length = 33
  Length2 = 100
  Profile = -> Sketch027
  Suppressed = false
  Type = 0
FEATURE [PartDesign::Mirrored] Mirrored
  MirrorPlane = -> YZ_Plane014
  Suppressed = false
  TransformMode = 0
FEATURE [PartDesign::Mirrored] Mirrored001
  MirrorPlane = -> XZ_Plane013
  Suppressed = false
  TransformMode = 0
FEATURE [PartDesign::MultiTransform] MultiTransform
  BaseFeature = -> Pad012
  Originals = -> [Pad010,Pad012,Pad011]
  Suppressed = false
  TransformMode = 0
  Transformations = -> [Mirrored,Mirrored001]
FEATURE [Sketcher::SketchObject] Sketch028
  ArcFitTolerance = 0
  AttachmentSupport = -> [XZ_Plane013]
  FullyConstrained = true
  MakeInternals = false
  MapMode = 5
  Placement = pos=(0,0,0) rot=(1,0,0;1.5708rad)
  sketch-geometry (4):
    g0: LineSegment StartX=-12.75 StartY=1 StartZ=0 EndX=12.75 EndY=1 EndZ=0
    g1: LineSegment StartX=12.75 StartY=1 StartZ=0 EndX=17.5 EndY=0 EndZ=0
    g2: LineSegment StartX=17.5 StartY=0 StartZ=0 EndX=-17.5 EndY=0 EndZ=0
    g3: LineSegment StartX=-17.5 StartY=0 StartZ=0 EndX=-12.75 EndY=1 EndZ=0
  constraints (10):
    c: Coincident(g0,g1)
    c: Coincident(g1,g2)
    c: Coincident(g2,g3)
    c: Coincident(g3,g0)
    c: PointOnObject(g1,g-1)
    c: Symmetric(g0,g0,g-2)
    c: Symmetric(g1,g2,g-2)
    c: DistanceX(g2,g2) = 35
    c: DistanceX(g0,g0) = 25.5
    c: DistanceY(g1,g1) = 1
FEATURE [PartDesign::Pocket] Pocket003
  BaseFeature = -> MultiTransform
  Direction = (0,1,-2e-16)
  Length = 20
  Length2 = 100
  Midplane = true
  Profile = -> Sketch028
  Suppressed = false
  Type = 0
FEATURE [Sketcher::SketchObject] Sketch029
  ArcFitTolerance = 0
  AttachmentOffset = pos=(0,0,2) rot=(0,0,1;0rad)
  AttachmentSupport = -> [XY_Plane013]
  FullyConstrained = true
  MakeInternals = false
  MapMode = 5
  Placement = pos=(0,0,2) rot=(0,0,1;0rad)
  sketch-geometry (9):
    g0: LineSegment StartX=23.95 StartY=5 StartZ=0 EndX=12.95 EndY=5 EndZ=0
    g1: LineSegment StartX=12.95 StartY=5 StartZ=0 EndX=12.95 EndY=-5 EndZ=0
    g2: LineSegment StartX=12.95 StartY=-5 StartZ=0 EndX=23.95 EndY=-5 EndZ=0
    g3: LineSegment StartX=23.95 StartY=-5 StartZ=0 EndX=23.95 EndY=-2.25 EndZ=0
    g4: ArcOfCircle CenterX=19 CenterY=0 CenterZ=0 NormalX=0 NormalY=0 NormalZ=1 AngleXU=0 Radius=2.25 StartAngle=1.5708 EndAngle=4.71239
    g5: LineSegment StartX=19 StartY=-2.25 StartZ=0 EndX=23.95 EndY=-2.25 EndZ=0
    g6: LineSegment StartX=19 StartY=2.25 StartZ=0 EndX=23.95 EndY=2.25 EndZ=0
    g7: LineSegment StartX=23.95 StartY=2.25 StartZ=0 EndX=23.95 EndY=5 EndZ=0
    g8: GeomPoint [constr] X=16.75 Y=0 Z=0
  constraints (23):
    c: Coincident(g0,g1)
    c: Coincident(g1,g2)
    c: Coincident(g2,g3)
    c: Coincident(g7,g0)
    c: Horizontal(g0)
    c: Horizontal(g2)
    c: Vertical(g1)
    c: Symmetric(g2,g0,g-1)
    c: Tangent(g4,g6) = 1.5708
    c: Tangent(g4,g5) = -1.5708
    c: Horizontal(g5)
    c: PointOnObject(g4,g-1)
    c: Coincident(g7,g6)
    c: Tangent(g3,g7)
    c: Coincident(g5,g3)
    c: Radius(g4) = 2.25
    c: Horizontal(g6)
    c: PointOnObject(g8,g4)
    c: PointOnObject(g8,g-1)
    c: DistanceX(g4) = 19
    c: DistanceX(g0) = 23.95
    c: DistanceY(g2,g0) = 10
    c: DistanceX(g0,g0) = 11
FEATURE [PartDesign::Pad] Pad013
  BaseFeature = -> Pocket003
  Direction = (0,0,1)
  Length = 7
  Length2 = 100
  Profile = -> Sketch029
  Suppressed = false
  Type = 0
FEATURE [Sketcher::SketchObject] Sketch030
  ArcFitTolerance = 0
  AttachmentOffset = pos=(0,0,9) rot=(0,0,1;0rad)
  AttachmentSupport = -> [XY_Plane013]
  FullyConstrained = true
  MakeInternals = false
  MapMode = 5
  Placement = pos=(0,0,9) rot=(0,0,1;0rad)
  sketch-geometry (4):
    g0: ArcOfCircle CenterX=19 CenterY=0 CenterZ=0 NormalX=0 NormalY=0 NormalZ=1 AngleXU=0 Radius=5 StartAngle=1.5708 EndAngle=4.71239
    g1: LineSegment StartX=19 StartY=-5 StartZ=0 EndX=25 EndY=-5 EndZ=0
    g2: LineSegment StartX=19 StartY=5 StartZ=0 EndX=25 EndY=5 EndZ=0
    g3: LineSegment StartX=25 StartY=5 StartZ=0 EndX=25 EndY=-5 EndZ=0
  constraints (11):
    c: Tangent(g0,g2) = 1.5708
    c: Tangent(g0,g1) = -1.5708
    c: Coincident(g1,g3) = -1.5708
    c: Coincident(g2,g3) = 1.5708
    c: Horizontal(g1)
    c: PointOnObject(g0,g-1)
    c: Vertical(g3)
    c: DistanceX(g0) = 19
    c: Radius(g0) = 5
    c: Horizontal(g2)
    c: DistanceX(g2) = 25
FEATURE [PartDesign::Pocket] Pocket004
  BaseFeature = -> Pad013
  Direction = (0,0,-1)
  Length = 10
  Length2 = 100
  Profile = -> Sketch030
  Reversed = true
  Suppressed = false
  Type = 0
FEATURE [PartDesign::Mirrored] Mirrored002
  BaseFeature = -> Pocket004
  MirrorPlane = -> YZ_Plane014
  Originals = -> [Pad013,Pocket004]
  Suppressed = false
  TransformMode = 0
FEATURE [Sketcher::SketchObject] Sketch031
  ArcFitTolerance = 0
  AttachmentSupport = -> [XZ_Plane013]
  FullyConstrained = true
  MakeInternals = false
  MapMode = 5
  Placement = pos=(0,0,0) rot=(1,0,0;1.5708rad)
  sketch-geometry (4):
    g0: LineSegment StartX=0 StartY=35 StartZ=0 EndX=0 EndY=29 EndZ=0
    g1: LineSegment StartX=0 StartY=29 StartZ=0 EndX=19.5 EndY=29 EndZ=0
    g2: LineSegment StartX=19.5 StartY=29 StartZ=0 EndX=19.5 EndY=35 EndZ=0
    g3: LineSegment StartX=0 StartY=35 StartZ=0 EndX=19.5 EndY=35 EndZ=0
  constraints (12):
    c: Coincident(g0,g1)
    c: Coincident(g1,g2)
    c: Horizontal(g1)
    c: Vertical(g0)
    c: Vertical(g2)
    c: PointOnObject(g0,g-2)
    c: DistanceX(g2) = 19.5
    c: DistanceY(g2) = 35
    c: DistanceY(g2,g2) = 6
    c: Coincident(g3,g0)
    c: Coincident(g3,g2)
    c: Horizontal(g3)
FEATURE [PartDesign::Groove] Groove
  Angle = 360
  Angle2 = 60
  Axis = (-3e-16,3e-16,1)
  Base = (0,0,0)
  BaseFeature = -> Mirrored002
  Profile = -> Sketch031
  ReferenceAxis = -> Z_Axis013
  Suppressed = false
  Type = 0
FEATURE [Sketcher::SketchObject] Sketch032
  ArcFitTolerance = 0
  AttachmentSupport = -> [XY_Plane013]
  FullyConstrained = true
  MakeInternals = false
  MapMode = 5
  sketch-geometry (2):
    g0: Circle CenterX=9.5 CenterY=0 CenterZ=0 NormalX=0 NormalY=0 NormalZ=1 AngleXU=0 Radius=2.85
    g1: Circle CenterX=-9.5 CenterY=0 CenterZ=0 NormalX=0 NormalY=0 NormalZ=1 AngleXU=0 Radius=2.85
  constraints (5):
    c: PointOnObject(g0,g-1)
    c: Symmetric(g0,g1,g-2)
    c: DistanceX(g1,g0) = 19
    c: Equal(g1,g0)
    c: Radius(g0) = 2.85
FEATURE [PartDesign::Pocket] Pocket005
  BaseFeature = -> Groove
  Direction = (0,0,-1)
  Length = 5
  Length2 = 100
  Midplane = true
  Profile = -> Sketch032
  Suppressed = false
  Type = 1
FEATURE [PartDesign::Fillet] Fillet001
  Base = -> Pocket005 [Edge52]
  BaseFeature = -> Pocket005
  Radius = 4
  SupportTransform = false
  Suppressed = false
  UseAllEdges = false
FEATURE [PartDesign::Body] Body013  label="Wallsocket"
  AllowCompound = false
  Group = -> [Sketch023,Pad009,Sketch024,Pocket002,Sketch025,Pad010,Sketch026,Pad011,Sketch027,Pad012,MultiTransform,Mirrored,Mirrored001,Sketch028,Pocket003,Sketch029,Pad013,Sketch030,Pocket004,Mirrored002,Sketch031,Groove,Sketch032,Pocket005,Fillet001]
  Origin = -> Origin013
  Tip = -> Fillet001
FEATURE [Sketcher::SketchObject] Sketch033  label="bl base"
  ArcFitTolerance = 0
  AttachmentSupport = -> [XZ_Plane014]
  FullyConstrained = true
  MakeInternals = false
  MapMode = 5
  Placement = pos=(0,0,0) rot=(1,0,0;1.5708rad)
  sketch-geometry (4):
    g0: LineSegment StartX=-30.5 StartY=2 StartZ=0 EndX=30.5 EndY=2 EndZ=0
    g1: LineSegment StartX=30.5 StartY=2 StartZ=0 EndX=30.5 EndY=-78 EndZ=0
    g2: LineSegment StartX=30.5 StartY=-78 StartZ=0 EndX=-30.5 EndY=-78 EndZ=0
    g3: LineSegment StartX=-30.5 StartY=-78 StartZ=0 EndX=-30.5 EndY=2 EndZ=0
  constraints (11):
    c: Coincident(g0,g1)
    c: Coincident(g1,g2)
    c: Coincident(g2,g3)
    c: Coincident(g3,g0)
    c: Horizontal(g2)
    c: Vertical(g1)
    c: Vertical(g3)
    c: Symmetric(g0,g0,g-2)
    c: DistanceY(g0) = 2
    c: DistanceX(g0,g0) = 61
    c: DistanceY(g1,g1) = 80
FEATURE [PartDesign::Pad] Pad014  label="BL Base"
  Direction = (0,-1,2e-16)
  Length = 61
  Length2 = 100
  Midplane = true
  Placement = pos=(0,0,0) rot=(1,0,0;1.5708rad)
  Profile = -> Sketch033
  Suppressed = false
  Type = 0
FEATURE [Sketcher::SketchObject] Sketch035  label="bm side -46"
  ArcFitTolerance = 0
  AttachmentOffset = pos=(0,0,-50) rot=(0,0,1;0rad)
  AttachmentSupport = -> [XY_Plane014]
  FullyConstrained = true
  MakeInternals = false
  MapMode = 5
  Placement = pos=(0,0,-50) rot=(0,0,1;0rad)
  sketch-geometry (16):
    g0: LineSegment StartX=-18.5 StartY=30.5 StartZ=0 EndX=18.5 EndY=30.5 EndZ=0
    g1: LineSegment StartX=30.5 StartY=18.5 StartZ=0 EndX=30.5 EndY=-18.5 EndZ=0
    g2: LineSegment StartX=18.5 StartY=-30.5 StartZ=0 EndX=-18.5 EndY=-30.5 EndZ=0
    g3: LineSegment StartX=-30.5 StartY=-18.5 StartZ=0 EndX=-30.5 EndY=18.5 EndZ=0
    g4: ArcOfCircle CenterX=18.5 CenterY=18.5 CenterZ=0 NormalX=0 NormalY=0 NormalZ=1 AngleXU=0 Radius=12 StartAngle=0 EndAngle=1.5708
    g5: ArcOfCircle CenterX=18.5 CenterY=-18.5 CenterZ=0 NormalX=0 NormalY=0 NormalZ=1 AngleXU=0 Radius=12 StartAngle=4.71239 EndAngle=6.28319
    g6: ArcOfCircle CenterX=-18.5 CenterY=-18.5 CenterZ=0 NormalX=0 NormalY=0 NormalZ=1 AngleXU=0 Radius=12 StartAngle=3.14159 EndAngle=4.71239
    g7: ArcOfCircle CenterX=-18.5 CenterY=18.5 CenterZ=0 NormalX=0 NormalY=0 NormalZ=1 AngleXU=0 Radius=12 StartAngle=1.5708 EndAngle=3.14159
    g8: LineSegment [constr] StartX=-18.5 StartY=18.5 StartZ=0 EndX=18.5 EndY=18.5 EndZ=0
    g9: LineSegment [constr] StartX=18.5 StartY=18.5 StartZ=0 EndX=18.5 EndY=-18.5 EndZ=0
    g10: LineSegment [constr] StartX=18.5 StartY=-18.5 StartZ=0 EndX=-18.5 EndY=-18.5 EndZ=0
    g11: LineSegment [constr] StartX=-18.5 StartY=-18.5 StartZ=0 EndX=-18.5 EndY=18.5 EndZ=0
    g12: LineSegment StartX=-32.5 StartY=32.5 StartZ=0 EndX=32.5 EndY=32.5 EndZ=0
    g13: LineSegment StartX=32.5 StartY=32.5 StartZ=0 EndX=32.5 EndY=-32.5 EndZ=0
    g14: LineSegment StartX=32.5 StartY=-32.5 StartZ=0 EndX=-32.5 EndY=-32.5 EndZ=0
    g15: LineSegment StartX=-32.5 StartY=-32.5 StartZ=0 EndX=-32.5 EndY=32.5 EndZ=0
  constraints (36):
    c: Horizontal(g0)
    c: Horizontal(g2)
    c: Vertical(g1)
    c: Vertical(g3)
    c: Tangent(g0,g4) = 1.5708
    c: Tangent(g1,g4) = 1.5708
    c: Tangent(g2,g5) = 1.5708
    c: Tangent(g1,g5) = 1.5708
    c: Tangent(g3,g6) = 1.5708
    c: Tangent(g2,g6) = 1.5708
    c: Tangent(g0,g7) = 1.5708
    c: Tangent(g3,g7) = 1.5708
    c: Coincident(g8,g9)
    c: Coincident(g9,g10)
    c: Coincident(g10,g11)
    c: Coincident(g11,g8)
    c: Horizontal(g10)
    c: Coincident(g8,g7)
    c: Coincident(g9,g5)
    c: Coincident(g4,g8)
    c: Coincident(g6,g10)
    c: DistanceX(g3,g1) = 61
    c: Radius(g4) = 12
    c: Equal(g9,g8)
    c: Symmetric(g4,g5,g-1)
    c: Symmetric(g4,g7,g-2)
    c: Coincident(g12,g13)
    c: Coincident(g13,g14)
    c: Coincident(g14,g15)
    c: Coincident(g15,g12)
    c: Horizontal(g14)
    c: Vertical(g15)
    c: Symmetric(g12,g13,g-1)
    c: Symmetric(g12,g12,g-2)
    c: Equal(g12,g13)
    c: DistanceX(g12,g12) = 65
FEATURE [Sketcher::SketchObject] Sketch036  label="bm side -45"
  ArcFitTolerance = 0
  AttachmentOffset = pos=(0,0,-45) rot=(0,0,1;0rad)
  AttachmentSupport = -> [XY_Plane014]
  FullyConstrained = true
  MakeInternals = false
  MapMode = 5
  Placement = pos=(0,0,-45) rot=(0,0,1;0rad)
  sketch-geometry (16):
    g0: LineSegment StartX=-22.5 StartY=30.5 StartZ=0 EndX=22.5 EndY=30.5 EndZ=0
    g1: LineSegment StartX=30.5 StartY=22.5 StartZ=0 EndX=30.5 EndY=-22.5 EndZ=0
    g2: LineSegment StartX=22.5 StartY=-30.5 StartZ=0 EndX=-22.5 EndY=-30.5 EndZ=0
    g3: LineSegment StartX=-30.5 StartY=-22.5 StartZ=0 EndX=-30.5 EndY=22.5 EndZ=0
    g4: ArcOfCircle CenterX=22.5 CenterY=22.5 CenterZ=0 NormalX=0 NormalY=0 NormalZ=1 AngleXU=0 Radius=8 StartAngle=1e-16 EndAngle=1.5708
    g5: ArcOfCircle CenterX=22.5 CenterY=-22.5 CenterZ=0 NormalX=0 NormalY=0 NormalZ=1 AngleXU=0 Radius=8 StartAngle=4.71239 EndAngle=6.28319
    g6: ArcOfCircle CenterX=-22.5 CenterY=-22.5 CenterZ=0 NormalX=0 NormalY=0 NormalZ=1 AngleXU=0 Radius=8 StartAngle=3.14159 EndAngle=4.71239
    g7: ArcOfCircle CenterX=-22.5 CenterY=22.5 CenterZ=0 NormalX=0 NormalY=0 NormalZ=1 AngleXU=0 Radius=8 StartAngle=1.5708 EndAngle=3.14159
    g8: LineSegment [constr] StartX=-22.5 StartY=22.5 StartZ=0 EndX=22.5 EndY=22.5 EndZ=0
    g9: LineSegment [constr] StartX=22.5 StartY=22.5 StartZ=0 EndX=22.5 EndY=-22.5 EndZ=0
    g10: LineSegment [constr] StartX=22.5 StartY=-22.5 StartZ=0 EndX=-22.5 EndY=-22.5 EndZ=0
    g11: LineSegment [constr] StartX=-22.5 StartY=-22.5 StartZ=0 EndX=-22.5 EndY=22.5 EndZ=0
    g12: LineSegment StartX=-32.5 StartY=32.5 StartZ=0 EndX=32.5 EndY=32.5 EndZ=0
    g13: LineSegment StartX=32.5 StartY=32.5 StartZ=0 EndX=32.5 EndY=-32.5 EndZ=0
    g14: LineSegment StartX=32.5 StartY=-32.5 StartZ=0 EndX=-32.5 EndY=-32.5 EndZ=0
    g15: LineSegment StartX=-32.5 StartY=-32.5 StartZ=0 EndX=-32.5 EndY=32.5 EndZ=0
  constraints (36):
    c: Horizontal(g0)
    c: Horizontal(g2)
    c: Vertical(g1)
    c: Vertical(g3)
    c: Tangent(g0,g4) = 1.5708
    c: Tangent(g1,g4) = 1.5708
    c: Tangent(g2,g5) = 1.5708
    c: Tangent(g1,g5) = 1.5708
    c: Tangent(g3,g6) = 1.5708
    c: Tangent(g2,g6) = 1.5708
    c: Tangent(g0,g7) = 1.5708
    c: Tangent(g3,g7) = 1.5708
    c: Coincident(g8,g9)
    c: Coincident(g9,g10)
    c: Coincident(g10,g11)
    c: Coincident(g11,g8)
    c: Horizontal(g10)
    c: Coincident(g8,g7)
    c: Coincident(g9,g5)
    c: Coincident(g4,g8)
    c: Coincident(g6,g10)
    c: DistanceX(g3,g1) = 61
    c: Radius(g4) = 8
    c: Equal(g9,g8)
    c: Symmetric(g4,g5,g-1)
    c: Symmetric(g4,g7,g-2)
    c: Coincident(g12,g13)
    c: Coincident(g13,g14)
    c: Coincident(g14,g15)
    c: Coincident(g15,g12)
    c: Horizontal(g14)
    c: Vertical(g15)
    c: Symmetric(g12,g13,g-1)
    c: Symmetric(g12,g12,g-2)
    c: Equal(g12,g13)
    c: DistanceX(g12,g12) = 65
FEATURE [Sketcher::SketchObject] Sketch037  label="bm side -80"
  ArcFitTolerance = 0
  AttachmentOffset = pos=(0,0,-80) rot=(0,0,1;0rad)
  AttachmentSupport = -> [XY_Plane014]
  FullyConstrained = true
  MakeInternals = false
  MapMode = 5
  Placement = pos=(0,0,-80) rot=(0,0,1;0rad)
  sketch-geometry (16):
    g0: LineSegment StartX=-0.1 StartY=8 StartZ=0 EndX=0.1 EndY=8 EndZ=0
    g1: LineSegment StartX=8 StartY=0.1 StartZ=0 EndX=8 EndY=-0.1 EndZ=0
    g2: LineSegment StartX=0.1 StartY=-8 StartZ=0 EndX=-0.1 EndY=-8 EndZ=0
    g3: LineSegment StartX=-8 StartY=-0.1 StartZ=0 EndX=-8 EndY=0.1 EndZ=0
    g4: ArcOfCircle CenterX=0.1 CenterY=0.1 CenterZ=0 NormalX=0 NormalY=0 NormalZ=1 AngleXU=0 Radius=7.9 StartAngle=0 EndAngle=1.5708
    g5: ArcOfCircle CenterX=0.1 CenterY=-0.1 CenterZ=0 NormalX=0 NormalY=0 NormalZ=1 AngleXU=0 Radius=7.9 StartAngle=4.71239 EndAngle=6.28319
    g6: ArcOfCircle CenterX=-0.1 CenterY=-0.1 CenterZ=0 NormalX=0 NormalY=0 NormalZ=1 AngleXU=0 Radius=7.9 StartAngle=3.14159 EndAngle=4.71239
    g7: ArcOfCircle CenterX=-0.1 CenterY=0.1 CenterZ=0 NormalX=0 NormalY=0 NormalZ=1 AngleXU=0 Radius=7.9 StartAngle=1.5708 EndAngle=3.14159
    g8: LineSegment [constr] StartX=-0.1 StartY=0.1 StartZ=0 EndX=0.1 EndY=0.1 EndZ=0
    g9: LineSegment [constr] StartX=0.1 StartY=0.1 StartZ=0 EndX=0.1 EndY=-0.1 EndZ=0
    g10: LineSegment [constr] StartX=0.1 StartY=-0.1 StartZ=0 EndX=-0.1 EndY=-0.1 EndZ=0
    g11: LineSegment [constr] StartX=-0.1 StartY=-0.1 StartZ=0 EndX=-0.1 EndY=0.1 EndZ=0
    g12: LineSegment StartX=-32.5 StartY=32.5 StartZ=0 EndX=32.5 EndY=32.5 EndZ=0
    g13: LineSegment StartX=32.5 StartY=32.5 StartZ=0 EndX=32.5 EndY=-32.5 EndZ=0
    g14: LineSegment StartX=32.5 StartY=-32.5 StartZ=0 EndX=-32.5 EndY=-32.5 EndZ=0
    g15: LineSegment StartX=-32.5 StartY=-32.5 StartZ=0 EndX=-32.5 EndY=32.5 EndZ=0
  constraints (36):
    c: Horizontal(g0)
    c: Horizontal(g2)
    c: Vertical(g1)
    c: Vertical(g3)
    c: Tangent(g0,g4) = 1.5708
    c: Tangent(g1,g4) = 1.5708
    c: Tangent(g2,g5) = 1.5708
    c: Tangent(g1,g5) = 1.5708
    c: Tangent(g3,g6) = 1.5708
    c: Tangent(g2,g6) = 1.5708
    c: Tangent(g0,g7) = 1.5708
    c: Tangent(g3,g7) = 1.5708
    c: Coincident(g8,g9)
    c: Coincident(g9,g10)
    c: Coincident(g10,g11)
    c: Coincident(g11,g8)
    c: Horizontal(g10)
    c: Coincident(g8,g7)
    c: Coincident(g9,g5)
    c: Coincident(g4,g8)
    c: Coincident(g6,g10)
    c: DistanceX(g3,g1) = 16
    c: Radius(g4) = 7.9
    c: Equal(g9,g8)
    c: Symmetric(g4,g5,g-1)
    c: Symmetric(g4,g7,g-2)
    c: Coincident(g12,g13)
    c: Coincident(g13,g14)
    c: Coincident(g14,g15)
    c: Coincident(g15,g12)
    c: Horizontal(g14)
    c: Vertical(g15)
    c: Symmetric(g12,g13,g-1)
    c: Symmetric(g12,g12,g-2)
    c: Equal(g12,g13)
    c: DistanceX(g12,g12) = 65
FEATURE [PartDesign::SubtractiveLoft] SubtractiveLoft  label="BL Side rear"
  BaseFeature = -> Pad014
  Closed = false
  Placement = pos=(0,0,0) rot=(1,0,0;1.5708rad)
  Profile = -> Sketch036
  Ruled = false
  Sections = -> [Sketch035,Sketch037]
  Suppressed = false
FEATURE [Sketcher::SketchObject] Sketch039  label="c cable trj"
  ArcFitTolerance = 0
  AttachmentSupport = -> [YZ_Plane016]
  FullyConstrained = true
  MakeInternals = false
  MapMode = 5
  Placement = pos=(0,0,0) rot=(0.57735,0.57735,0.57735;2.0944rad)
  sketch-geometry (4):
    g0: LineSegment StartX=20 StartY=0 StartZ=0 EndX=20 EndY=-21.7335 EndZ=0
    g1: ArcOfCircle CenterX=8 CenterY=-21.7335 CenterZ=0 NormalX=0 NormalY=0 NormalZ=1 AngleXU=0 Radius=12 StartAngle=5.6975 EndAngle=6.28319
    g2: LineSegment StartX=16 StartY=-35 StartZ=0 EndX=16 EndY=-80 EndZ=0
    g3: ArcOfCircle CenterX=28 CenterY=-35 CenterZ=0 NormalX=0 NormalY=0 NormalZ=1 AngleXU=0 Radius=12 StartAngle=2.55591 EndAngle=3.14159
  constraints (12):
    c: PointOnObject(g0,g-1)
    c: Vertical(g0)
    c: DistanceX(g0) = 20
    c: Tangent(g0,g1) = 1.5708
    c: Radius(g1) = 12
    c: Vertical(g2)
    c: DistanceX(g-1,g2) = 16
    c: Tangent(g1,g3) = 1.5708
    c: Tangent(g2,g3) = -1.5708
    c: Equal(g3,g1)
    c: DistanceY(g2,g-1) = 35
    c: DistanceY(g2,g-1) = 80
FEATURE [PartDesign::Pocket] Pocket006  label="BL Side front"
  BaseFeature = -> SubtractiveLoft
  Direction = (0,0,-1)
  Length = 5
  Length2 = 100
  Placement = pos=(0,0,0) rot=(1,0,0;1.5708rad)
  Profile = -> Sketch036
  Reversed = true
  Suppressed = false
  Type = 1
FEATURE [Sketcher::SketchObject] Sketch040  label="bl cutout wallsocket"
  ArcFitTolerance = 0
  AttachmentSupport = -> [XY_Plane014]
  FullyConstrained = true
  MakeInternals = false
  MapMode = 5
  sketch-geometry (16):
    g0: LineSegment StartX=-22.7 StartY=25.8 StartZ=0 EndX=22.7 EndY=25.8 EndZ=0
    g1: LineSegment StartX=26.2 StartY=22.3 StartZ=0 EndX=26.2 EndY=-22.3 EndZ=0
    g2: LineSegment StartX=22.7 StartY=-25.8 StartZ=0 EndX=-22.7 EndY=-25.8 EndZ=0
    g3: LineSegment StartX=-26.2 StartY=-22.3 StartZ=0 EndX=-26.2 EndY=22.3 EndZ=0
    g4: ArcOfCircle CenterX=-22.7 CenterY=22.3 CenterZ=0 NormalX=0 NormalY=0 NormalZ=1 AngleXU=0 Radius=3.5 StartAngle=1.5708 EndAngle=3.14159
    g5: ArcOfCircle CenterX=22.7 CenterY=22.3 CenterZ=0 NormalX=0 NormalY=0 NormalZ=1 AngleXU=0 Radius=3.5 StartAngle=0 EndAngle=1.5708
    g6: ArcOfCircle CenterX=22.7 CenterY=-22.3 CenterZ=0 NormalX=0 NormalY=0 NormalZ=1 AngleXU=0 Radius=3.5 StartAngle=4.71239 EndAngle=6.28319
    g7: ArcOfCircle CenterX=-22.7 CenterY=-22.3 CenterZ=0 NormalX=0 NormalY=0 NormalZ=1 AngleXU=0 Radius=3.5 StartAngle=3.14159 EndAngle=4.71239
    g8: LineSegment [constr] StartX=-22.7 StartY=22.3 StartZ=0 EndX=22.7 EndY=22.3 EndZ=0
    g9: LineSegment [constr] StartX=22.7 StartY=22.3 StartZ=0 EndX=22.7 EndY=-22.3 EndZ=0
    g10: LineSegment [constr] StartX=22.7 StartY=-22.3 StartZ=0 EndX=-22.7 EndY=-22.3 EndZ=0
    g11: LineSegment [constr] StartX=-22.7 StartY=-22.3 StartZ=0 EndX=-22.7 EndY=22.3 EndZ=0
    g12: LineSegment StartX=-35 StartY=35 StartZ=0 EndX=35 EndY=35 EndZ=0
    g13: LineSegment StartX=35 StartY=35 StartZ=0 EndX=35 EndY=-35 EndZ=0
    g14: LineSegment StartX=35 StartY=-35 StartZ=0 EndX=-35 EndY=-35 EndZ=0
    g15: LineSegment StartX=-35 StartY=-35 StartZ=0 EndX=-35 EndY=35 EndZ=0
  constraints (36):
    c: Horizontal(g0)
    c: Horizontal(g2)
    c: Vertical(g1)
    c: Vertical(g3)
    c: Tangent(g3,g4) = 1.5708
    c: Tangent(g0,g4) = 1.5708
    c: Tangent(g0,g5) = 1.5708
    c: Tangent(g1,g5) = 1.5708
    c: Tangent(g1,g6) = 1.5708
    c: Tangent(g2,g6) = 1.5708
    c: Tangent(g3,g7) = 1.5708
    c: Tangent(g2,g7) = 1.5708
    c: Coincident(g8,g9)
    c: Coincident(g9,g10)
    c: Coincident(g10,g11)
    c: Coincident(g11,g8)
    c: Horizontal(g10)
    c: Coincident(g8,g4)
    c: Coincident(g9,g6)
    c: Coincident(g5,g8)
    c: Coincident(g7,g10)
    c: Symmetric(g4,g5,g-2)
    c: Symmetric(g5,g6,g-1)
    c: DistanceX(g3,g1) = 52.4
    c: DistanceY(g2,g0) = 51.6
    c: Radius(g5) = 3.5
    c: Coincident(g12,g13)
    c: Coincident(g13,g14)
    c: Coincident(g14,g15)
    c: Coincident(g15,g12)
    c: Horizontal(g14)
    c: Vertical(g15)
    c: Symmetric(g13,g12,g-1)
    c: Symmetric(g12,g12,g-2)
    c: Equal(g13,g12)
    c: DistanceX(g12,g12) = 70
FEATURE [PartDesign::Pocket] Pocket007  label="BL Cutout wallsocket"
  BaseFeature = -> Pocket006
  Direction = (0,0,-1)
  Length = 5
  Length2 = 100
  Placement = pos=(0,0,0) rot=(1,0,0;1.5708rad)
  Profile = -> Sketch040
  Reversed = true
  Suppressed = false
  Type = 1
FEATURE [Sketcher::SketchObject] Sketch041  label="bl cutout notch wallsocket"
  ArcFitTolerance = 0
  AttachmentOffset = pos=(0,0,-2) rot=(0,0,1;0rad)
  AttachmentSupport = -> [XY_Plane014]
  FullyConstrained = true
  MakeInternals = false
  MapMode = 5
  Placement = pos=(0,0,-2) rot=(0,0,1;0rad)
  sketch-geometry (12):
    g0: LineSegment StartX=13.6 StartY=7.6 StartZ=0 EndX=20.8 EndY=7.6 EndZ=0
    g1: LineSegment StartX=22 StartY=6.4 StartZ=0 EndX=22 EndY=-6.4 EndZ=0
    g2: LineSegment StartX=20.8 StartY=-7.6 StartZ=0 EndX=13.6 EndY=-7.6 EndZ=0
    g3: LineSegment StartX=12.4 StartY=-6.4 StartZ=0 EndX=12.4 EndY=6.4 EndZ=0
    g4: ArcOfCircle CenterX=13.6 CenterY=6.4 CenterZ=0 NormalX=0 NormalY=0 NormalZ=1 AngleXU=0 Radius=1.2 StartAngle=1.5708 EndAngle=3.14159
    g5: ArcOfCircle CenterX=20.8 CenterY=6.4 CenterZ=0 NormalX=0 NormalY=0 NormalZ=1 AngleXU=0 Radius=1.2 StartAngle=0 EndAngle=1.5708
    g6: ArcOfCircle CenterX=20.8 CenterY=-6.4 CenterZ=0 NormalX=0 NormalY=0 NormalZ=1 AngleXU=0 Radius=1.2 StartAngle=4.71239 EndAngle=6.28319
    g7: ArcOfCircle CenterX=13.6 CenterY=-6.4 CenterZ=0 NormalX=0 NormalY=0 NormalZ=1 AngleXU=0 Radius=1.2 StartAngle=3.14159 EndAngle=4.71239
    g8: LineSegment [constr] StartX=13.6 StartY=6.4 StartZ=0 EndX=20.8 EndY=6.4 EndZ=0
    g9: LineSegment [constr] StartX=20.8 StartY=6.4 StartZ=0 EndX=20.8 EndY=-6.4 EndZ=0
    g10: LineSegment [constr] StartX=20.8 StartY=-6.4 StartZ=0 EndX=13.6 EndY=-6.4 EndZ=0
    g11: LineSegment [constr] StartX=13.6 StartY=-6.4 StartZ=0 EndX=13.6 EndY=6.4 EndZ=0
  constraints (27):
    c: Horizontal(g0)
    c: Horizontal(g2)
    c: Vertical(g1)
    c: Vertical(g3)
    c: Tangent(g3,g4) = 1.5708
    c: Tangent(g0,g4) = 1.5708
    c: Tangent(g0,g5) = 1.5708
    c: Tangent(g1,g5) = 1.5708
    c: Tangent(g1,g6) = 1.5708
    c: Tangent(g2,g6) = 1.5708
    c: Tangent(g2,g7) = 1.5708
    c: Tangent(g3,g7) = 1.5708
    c: Coincident(g8,g9)
    c: Coincident(g9,g10)
    c: Coincident(g10,g11)
    c: Coincident(g11,g8)
    c: Horizontal(g8)
    c: Horizontal(g10)
    c: Coincident(g8,g4)
    c: Coincident(g9,g6)
    c: Coincident(g5,g8)
    c: Coincident(g7,g10)
    c: Symmetric(g5,g6,g-1)
    c: DistanceY(g2,g0) = 15.2
    c: DistanceX(g1) = 22
    c: DistanceX(g3,g1) = 9.6
    c: Radius(g5) = 1.2
FEATURE [PartDesign::Pocket] Pocket008  label="BL cutout notch wallsocket R"
  BaseFeature = -> Pocket007
  Direction = (0,0,-1)
  Length = 5
  Length2 = 100
  Placement = pos=(0,0,0) rot=(1,0,0;1.5708rad)
  Profile = -> Sketch041
  Reversed = true
  Suppressed = false
  Type = 1
FEATURE [PartDesign::Mirrored] Mirrored003  label="BL cutout notch wallsocket L"
  BaseFeature = -> Pocket008
  MirrorPlane = -> YZ_Plane015
  Originals = -> [Pocket008]
  Placement = pos=(0,0,0) rot=(1,0,0;1.5708rad)
  Suppressed = false
  TransformMode = 0
FEATURE [Sketcher::SketchObject] Sketch042  label="bl nutslot"
  ArcFitTolerance = 0
  AttachmentOffset = pos=(0,0,-5.7) rot=(0,0,1;0rad)
  AttachmentSupport = -> [XY_Plane014]
  FullyConstrained = true
  MakeInternals = false
  MapMode = 5
  Placement = pos=(0,0,-5.7) rot=(0,0,1;0rad)
  sketch-geometry (8):
    g0: LineSegment StartX=21.1218 StartY=3.675 StartZ=0 EndX=-21.1218 EndY=3.675 EndZ=0
    g1: LineSegment StartX=-21.1218 StartY=3.675 StartZ=0 EndX=-23.2435 EndY=9e-16 EndZ=0
    g2: LineSegment StartX=-23.2435 StartY=9e-16 StartZ=0 EndX=-21.1218 EndY=-3.675 EndZ=0
    g3: LineSegment StartX=-21.1218 StartY=-3.675 StartZ=0 EndX=21.1218 EndY=-3.675 EndZ=0
    g4: LineSegment StartX=21.1218 StartY=-3.675 StartZ=0 EndX=23.2435 EndY=0 EndZ=0
    g5: LineSegment StartX=23.2435 StartY=0 StartZ=0 EndX=21.1218 EndY=3.675 EndZ=0
    g6: Circle [constr] CenterX=-19 CenterY=0 CenterZ=0 NormalX=0 NormalY=0 NormalZ=1 AngleXU=0 Radius=3.675
    g7: Circle [constr] CenterX=19 CenterY=0 CenterZ=0 NormalX=0 NormalY=0 NormalZ=1 AngleXU=0 Radius=3.675
  constraints (22):
    c: Coincident(g0,g1)
    c: Coincident(g1,g2)
    c: Coincident(g2,g3)
    c: Coincident(g3,g4)
    c: Coincident(g4,g5)
    c: Coincident(g5,g0)
    c: Symmetric(g2,g0,g-1)
    c: Horizontal(g0)
    c: Horizontal(g3)
    c: Angle(g2,g1) = 2.0944
    c: Equal(g2,g1)
    c: Equal(g1,g5)
    c: Equal(g5,g4)
    c: DistanceY(g2,g0) = 7.35
    c: PointOnObject(g6,g-1)
    c: Tangent(g6,g0)
    c: Tangent(g6,g1)
    c: PointOnObject(g4,g-1)
    c: Tangent(g7,g5)
    c: Equal(g7,g6)
    c: Symmetric(g7,g6,g-2)
    c: DistanceX(g6,g7) = 38
FEATURE [PartDesign::Pocket] Pocket009  label="BL Nutslot"
  BaseFeature = -> Mirrored003
  Direction = (0,0,-1)
  Length = 3.5
  Length2 = 100
  Placement = pos=(0,0,0) rot=(1,0,0;1.5708rad)
  Profile = -> Sketch042
  Suppressed = false
  Type = 0
FEATURE [Sketcher::SketchObject] Sketch043  label="bl bolthole"
  ArcFitTolerance = 0
  AttachmentSupport = -> [XZ_Plane014]
  FullyConstrained = true
  MakeInternals = false
  MapMode = 5
  Placement = pos=(0,0,0) rot=(1,0,0;1.5708rad)
  sketch-geometry (5):
    g0: LineSegment StartX=19 StartY=3 StartZ=0 EndX=21.3 EndY=3 EndZ=0
    g1: LineSegment StartX=21.3 StartY=3 StartZ=0 EndX=21.3 EndY=-14 EndZ=0
    g2: LineSegment StartX=21.3 StartY=-14 StartZ=0 EndX=19 EndY=-14 EndZ=0
    g3: LineSegment StartX=19 StartY=-14 StartZ=0 EndX=19 EndY=3 EndZ=0
    g4: LineSegment [constr] StartX=19 StartY=-14 StartZ=0 EndX=19 EndY=-16.3 EndZ=0
  constraints (15):
    c: Coincident(g0,g1)
    c: Coincident(g1,g2)
    c: Coincident(g2,g3)
    c: Coincident(g3,g0)
    c: Horizontal(g0)
    c: Horizontal(g2)
    c: Vertical(g1)
    c: Vertical(g3)
    c: DistanceX(g0) = 19
    c: DistanceY(g0) = 3
    c: DistanceX(g0,g0) = 2.3
    c: DistanceY(g1,g1) = 17
    c: Coincident(g4,g2)
    c: Vertical(g4)
    c: Equal(g2,g4)
FEATURE [PartDesign::Groove] Groove001  label="BL Bolt hole R"
  Angle = 360
  Angle2 = 60
  Axis = (0,-5e-16,-2.3)
  Base = (19,-3.1e-15,-14)
  BaseFeature = -> Pocket009
  Placement = pos=(0,0,0) rot=(1,0,0;1.5708rad)
  Profile = -> Sketch043
  ReferenceAxis = -> Sketch043 [Axis]
  Reversed = true
  Suppressed = false
  Type = 0
FEATURE [PartDesign::Mirrored] Mirrored004  label="BL Bolt hole L"
  BaseFeature = -> Groove001
  MirrorPlane = -> YZ_Plane015
  Originals = -> [Groove001]
  Placement = pos=(0,0,0) rot=(1,0,0;1.5708rad)
  Suppressed = false
  TransformMode = 0
FEATURE [Sketcher::SketchObject] Sketch044  label="bl stepper pocket"
  ArcFitTolerance = 0
  AttachmentSupport = -> [XY_Plane014]
  FullyConstrained = true
  MakeInternals = false
  MapMode = 5
  sketch-geometry (12):
    g0: LineSegment StartX=-17.75 StartY=12.4 StartZ=0 EndX=-15.75 EndY=12.4 EndZ=0
    g1: LineSegment StartX=17.75 StartY=12.4 StartZ=0 EndX=17.75 EndY=9.9 EndZ=0
    g2: LineSegment StartX=17.75 StartY=9.9 StartZ=0 EndX=15 EndY=9.9 EndZ=0
    g3: LineSegment StartX=-17.75 StartY=9.9 StartZ=0 EndX=-17.75 EndY=12.4 EndZ=0
    g4: LineSegment StartX=-15.75 StartY=13.9 StartZ=0 EndX=15.75 EndY=13.9 EndZ=0
    g5: LineSegment StartX=15.75 StartY=13.9 StartZ=0 EndX=15.75 EndY=12.4 EndZ=0
    g6: LineSegment StartX=-15.75 StartY=12.4 StartZ=0 EndX=-15.75 EndY=13.9 EndZ=0
    g7: LineSegment StartX=15.75 StartY=12.4 StartZ=0 EndX=17.75 EndY=12.4 EndZ=0
    g8: LineSegment StartX=15 StartY=9.9 StartZ=0 EndX=15 EndY=0.9 EndZ=0
    g9: LineSegment StartX=15 StartY=0.9 StartZ=0 EndX=-12 EndY=0.9 EndZ=0
    g10: LineSegment StartX=-12 StartY=0.9 StartZ=0 EndX=-12 EndY=9.9 EndZ=0
    g11: LineSegment StartX=-12 StartY=9.9 StartZ=0 EndX=-17.75 EndY=9.9 EndZ=0
  constraints (32):
    c: Coincident(g7,g1)
    c: Coincident(g1,g2)
    c: Coincident(g11,g3)
    c: Coincident(g3,g0)
    c: Horizontal(g2)
    c: Vertical(g1)
    c: Vertical(g3)
    c: Symmetric(g7,g0,g-2)
    c: DistanceX(g0,g7) = 35.5
    c: DistanceY(g0) = 12.4
    c: DistanceY(g3,g3) = 2.5
    c: Coincident(g4,g5)
    c: Coincident(g6,g4)
    c: Vertical(g5)
    c: Vertical(g6)
    c: Symmetric(g4,g4,g-2)
    c: Tangent(g0,g7)
    c: Coincident(g0,g6)
    c: DistanceX(g0,g0) = 2
    c: DistanceY(g6,g6) = 1.5
    c: Coincident(g5,g7)
    c: Coincident(g8,g9)
    c: Coincident(g9,g10)
    c: Horizontal(g9)
    c: Vertical(g8)
    c: Vertical(g10)
    c: DistanceX(g8) = 15
    c: DistanceX(g10,g-1) = 12
    c: Tangent(g2,g11)
    c: Coincident(g10,g11)
    c: Coincident(g2,g8)
    c: DistanceY(g8,g8) = 9
FEATURE [PartDesign::Pocket] Pocket010  label="BL Stepper pocket"
  BaseFeature = -> Mirrored004
  Direction = (0,0,-1)
  Length = 38.2
  Length2 = 100
  Placement = pos=(0,0,0) rot=(1,0,0;1.5708rad)
  Profile = -> Sketch044
  Suppressed = false
  Type = 0
FEATURE [Sketcher::SketchObject] Sketch045  label="bl esp pcb pocket"
  ArcFitTolerance = 0
  AttachmentSupport = -> [YZ_Plane015]
  FullyConstrained = true
  MakeInternals = false
  MapMode = 5
  Placement = pos=(0,0,0) rot=(0.57735,0.57735,0.57735;2.0944rad)
  sketch-geometry (4):
    g0: LineSegment StartX=-4.3 StartY=-26.2 StartZ=0 EndX=-2.7 EndY=-26.2 EndZ=0
    g1: LineSegment StartX=-2.7 StartY=-26.2 StartZ=0 EndX=-2.7 EndY=-57.8 EndZ=0
    g2: LineSegment StartX=-2.7 StartY=-57.8 StartZ=0 EndX=-4.3 EndY=-57.8 EndZ=0
    g3: LineSegment StartX=-4.3 StartY=-57.8 StartZ=0 EndX=-4.3 EndY=-26.2 EndZ=0
  constraints (12):
    c: Coincident(g0,g1)
    c: Coincident(g1,g2)
    c: Coincident(g2,g3)
    c: Coincident(g3,g0)
    c: Horizontal(g0)
    c: Horizontal(g2)
    c: Vertical(g1)
    c: Vertical(g3)
    c: DistanceX(g0,g-1) = 2.7
    c: DistanceX(g0,g0) = 1.6
    c: DistanceY(g0,g-1) = 26.2
    c: DistanceY(g3,g3) = 31.6
FEATURE [PartDesign::Pocket] Pocket011  label="BL ESP PCB pocket"
  BaseFeature = -> Pocket010
  Direction = (-1,0,0)
  Length = 13.7
  Length2 = 25.7
  Placement = pos=(0,0,0) rot=(1,0,0;1.5708rad)
  Profile = -> Sketch045
  Suppressed = false
  Type = 4
FEATURE [Sketcher::SketchObject] Sketch046  label="bl esp component pocket"
  ArcFitTolerance = 0
  AttachmentSupport = -> [XZ_Plane014]
  ExternalGeometry = -> [Sketch045,Pocket011]
  FullyConstrained = true
  MakeInternals = false
  MapMode = 5
  Placement = pos=(0,0,0) rot=(1,0,0;1.5708rad)
  sketch-geometry (6):
    g0: LineSegment StartX=-9.5 StartY=-26.2 StartZ=0 EndX=25.7 EndY=-26.2 EndZ=0
    g1: LineSegment StartX=25.7 StartY=-26.2 StartZ=0 EndX=25.7 EndY=-52.8 EndZ=0
    g2: LineSegment StartX=24.2 StartY=-57.8 StartZ=0 EndX=-9.5 EndY=-57.8 EndZ=0
    g3: LineSegment StartX=-9.5 StartY=-57.8 StartZ=0 EndX=-9.5 EndY=-26.2 EndZ=0
    g4: LineSegment StartX=25.7 StartY=-52.8 StartZ=0 EndX=24.2 EndY=-52.8 EndZ=0
    g5: LineSegment StartX=24.2 StartY=-52.8 StartZ=0 EndX=24.2 EndY=-57.8 EndZ=0
  constraints (18):
    c: Coincident(g0,g1)
    c: Coincident(g2,g3)
    c: Coincident(g3,g0)
    c: Horizontal(g0)
    c: Horizontal(g2)
    c: Vertical(g1)
    c: Vertical(g3)
    c: PointOnObject(g-3,g0)
    c: PointOnObject(g-3,g2)
    c: DistanceX(g2,g-3) = 9.5
    c: DistanceX(g0) = 25.7
    c: Coincident(g4,g5)
    c: Horizontal(g4)
    c: Vertical(g5)
    c: Coincident(g1,g4)
    c: Coincident(g5,g2)
    c: DistanceY(g5,g5) = 5
    c: DistanceX(g4,g4) = 1.5
FEATURE [PartDesign::Pocket] Pocket012  label="BL ESP Component pocket"
  BaseFeature = -> Pocket011
  Direction = (0,1,-2e-16)
  Length = 4
  Length2 = 5.3
  Placement = pos=(0,0,0) rot=(1,0,0;1.5708rad)
  Profile = -> Sketch046
  Suppressed = false
  Type = 4
FEATURE [Sketcher::SketchObject] Sketch047  label="bl esp usb pocket"
  ArcFitTolerance = 0
  AttachmentOffset = pos=(0,0,18) rot=(0,0,1;0rad)
  AttachmentSupport = -> [YZ_Plane015]
  FullyConstrained = true
  MakeInternals = false
  MapMode = 5
  Placement = pos=(18,0,0) rot=(0.57735,0.57735,0.57735;2.0944rad)
  sketch-geometry (4):
    g0: ArcOfCircle CenterX=-1.5 CenterY=-39.2 CenterZ=0 NormalX=0 NormalY=0 NormalZ=1 AngleXU=0 Radius=2 StartAngle=1.4e-15 EndAngle=3.14159
    g1: ArcOfCircle CenterX=-1.5 CenterY=-44.5 CenterZ=0 NormalX=0 NormalY=0 NormalZ=1 AngleXU=0 Radius=2 StartAngle=3.14159 EndAngle=6.28319
    g2: LineSegment StartX=-3.5 StartY=-39.2 StartZ=0 EndX=-3.5 EndY=-44.5 EndZ=0
    g3: LineSegment StartX=0.5 StartY=-39.2 StartZ=0 EndX=0.5 EndY=-44.5 EndZ=0
  constraints (10):
    c: Tangent(g0,g3)
    c: Tangent(g0,g2)
    c: Tangent(g2,g1)
    c: Tangent(g3,g1)
    c: Vertical(g2)
    c: Equal(g0,g1)
    c: Radius(g0) = 2
    c: DistanceY(g1,g0) = 5.3
    c: DistanceY(g0,g-1) = 39.2
    c: DistanceX(g0,g-1) = 1.5
FEATURE [PartDesign::Pocket] Pocket013  label="BL ESP USB pocket"
  BaseFeature = -> Pocket012
  Direction = (-1,0,0)
  Length = 5
  Length2 = 100
  Placement = pos=(0,0,0) rot=(1,0,0;1.5708rad)
  Profile = -> Sketch047
  Reversed = true
  Suppressed = false
  Type = 1
FEATURE [Sketcher::SketchObject] Sketch048  label="bl usb recess trj"
  ArcFitTolerance = 0
  AttachmentSupport = -> [XZ_Plane014]
  FullyConstrained = true
  MakeInternals = false
  MapMode = 5
  Placement = pos=(0,0,0) rot=(1,0,0;1.5708rad)
  sketch-geometry (3):
    g0: ArcOfCircle CenterX=42.5 CenterY=-38.5 CenterZ=0 NormalX=0 NormalY=0 NormalZ=1 AngleXU=0 Radius=16 StartAngle=1.5708 EndAngle=3.14159
    g1: ArcOfCircle CenterX=42.5 CenterY=-45 CenterZ=0 NormalX=0 NormalY=0 NormalZ=1 AngleXU=0 Radius=16 StartAngle=3.14159 EndAngle=4.71239
    g2: LineSegment StartX=26.5 StartY=-38.5 StartZ=0 EndX=26.5 EndY=-45 EndZ=0
  constraints (10):
    c: Vertical(g2)
    c: DistanceX(g2) = 26.5
    c: Tangent(g0,g2) = -1.5708
    c: Tangent(g1,g2) = -1.5708
    c: DistanceY(g0,g-1) = 38.5
    c: DistanceY(g2,g2) = 6.5
    c: Radius(g1) = 16
    c: Equal(g1,g0)
    c: Vertical(g1,g0)
    c: Vertical(g0,g0)
FEATURE [Sketcher::SketchObject] Sketch049  label="bl usb recess crs"
  ArcFitTolerance = 0
  AttachmentOffset = pos=(0,0,-40) rot=(0,0,1;0rad)
  AttachmentSupport = -> [XY_Plane014]
  FullyConstrained = true
  MakeInternals = false
  MapMode = 5
  Placement = pos=(0,0,-40) rot=(0,0,1;0rad)
  sketch-geometry (4):
    g0: ArcOfCircle CenterX=38.5 CenterY=2 CenterZ=0 NormalX=0 NormalY=0 NormalZ=1 AngleXU=0 Radius=12 StartAngle=-3.6e-15 EndAngle=3.14159
    g1: ArcOfCircle CenterX=38.5 CenterY=-6 CenterZ=0 NormalX=0 NormalY=0 NormalZ=1 AngleXU=0 Radius=12 StartAngle=3.14159 EndAngle=6.28319
    g2: LineSegment StartX=26.5 StartY=2 StartZ=0 EndX=26.5 EndY=-6 EndZ=0
    g3: LineSegment StartX=50.5 StartY=2 StartZ=0 EndX=50.5 EndY=-6 EndZ=0
  constraints (10):
    c: Tangent(g0,g3)
    c: Tangent(g0,g2)
    c: Tangent(g2,g1)
    c: Tangent(g3,g1)
    c: Vertical(g2)
    c: Equal(g0,g1)
    c: DistanceX(g0) = 26.5
    c: DistanceY(g-1,g0) = 2
    c: DistanceY(g1,g-1) = 6
    c: Radius(g0) = 12
FEATURE [PartDesign::SubtractivePipe] SubtractivePipe  label="BL ESP USB recess"
  AuxilleryCurvelinear = true
  AuxillerySpineTangent = false
  BaseFeature = -> Pocket013
  Binormal = (0,0,0)
  Mode = 0
  Placement = pos=(0,0,0) rot=(1,0,0;1.5708rad)
  Profile = -> Sketch049
  Spine = -> Sketch048
  SpineTangent = false
  Suppressed = false
  Transformation = 0
  Transition = 0
FEATURE [Sketcher::SketchObject] Sketch050  label="bl esp antenna cutout"
  ArcFitTolerance = 0
  AttachmentOffset = pos=(0,0,1.5) rot=(0,0,1;0rad)
  AttachmentSupport = -> [XZ_Plane014]
  FullyConstrained = true
  MakeInternals = false
  MapMode = 5
  Placement = pos=(0,-1.5,3e-16) rot=(1,0,0;1.5708rad)
  sketch-geometry (4):
    g0: LineSegment StartX=-13.7 StartY=-32 StartZ=0 EndX=-5.7 EndY=-32 EndZ=0
    g1: LineSegment StartX=-5.7 StartY=-32 StartZ=0 EndX=-5.7 EndY=-52.5 EndZ=0
    g2: LineSegment StartX=-5.7 StartY=-52.5 StartZ=0 EndX=-13.7 EndY=-52.5 EndZ=0
    g3: LineSegment StartX=-13.7 StartY=-52.5 StartZ=0 EndX=-13.7 EndY=-32 EndZ=0
  constraints (12):
    c: Coincident(g0,g1)
    c: Coincident(g1,g2)
    c: Coincident(g2,g3)
    c: Coincident(g3,g0)
    c: Horizontal(g0)
    c: Horizontal(g2)
    c: Vertical(g1)
    c: Vertical(g3)
    c: DistanceX(g0,g-1) = 13.7
    c: DistanceX(g0,g0) = 8
    c: DistanceY(g0,g-1) = 32
    c: DistanceY(g3,g3) = 20.5
FEATURE [PartDesign::Pocket] Pocket014  label="BL ESP antenna cutout"
  BaseFeature = -> SubtractivePipe
  Direction = (0,1,-2e-16)
  Length = 2
  Length2 = 100
  Placement = pos=(0,0,0) rot=(1,0,0;1.5708rad)
  Profile = -> Sketch050
  Reversed = true
  Suppressed = false
  Type = 0
FEATURE [Sketcher::SketchObject] Sketch051  label="bl relay cutout"
  ArcFitTolerance = 0
  AttachmentSupport = -> [YZ_Plane015]
  FullyConstrained = true
  MakeInternals = false
  MapMode = 5
  Placement = pos=(0,0,0) rot=(0.57735,0.57735,0.57735;2.0944rad)
  sketch-geometry (6):
    g0: LineSegment StartX=-7.1 StartY=5 StartZ=0 EndX=-27 EndY=5 EndZ=0
    g1: LineSegment StartX=-27 StartY=5 StartZ=0 EndX=-27 EndY=-34.7 EndZ=0
    g2: LineSegment StartX=-19.1 StartY=-49.5 StartZ=0 EndX=-7.1 EndY=-49.5 EndZ=0
    g3: LineSegment StartX=-7.1 StartY=-49.5 StartZ=0 EndX=-7.1 EndY=5 EndZ=0
    g4: LineSegment StartX=-19.1 StartY=-34.7 StartZ=0 EndX=-27 EndY=-34.7 EndZ=0
    g5: LineSegment StartX=-19.1 StartY=-49.5 StartZ=0 EndX=-19.1 EndY=-34.7 EndZ=0
  constraints (18):
    c: Coincident(g0,g1)
    c: Coincident(g2,g3)
    c: Coincident(g3,g0)
    c: Horizontal(g0)
    c: Horizontal(g2)
    c: Vertical(g1)
    c: Vertical(g3)
    c: Coincident(g5,g4)
    c: Horizontal(g4)
    c: Vertical(g5)
    c: DistanceX(g2,g-1) = 7.1
    c: Coincident(g5,g2)
    c: Coincident(g4,g1)
    c: DistanceY(g2,g-1) = 49.5
    c: DistanceX(g2,g2) = 12
    c: DistanceY(g5,g5) = 14.8
    c: DistanceY(g0) = 5
    c: DistanceX(g0,g-1) = 27
FEATURE [PartDesign::Pocket] Pocket015  label="BL Relay cutout"
  BaseFeature = -> Pocket014
  Direction = (-1,0,0)
  Length = 18
  Length2 = 100
  Midplane = true
  Placement = pos=(0,0,0) rot=(1,0,0;1.5708rad)
  Profile = -> Sketch051
  Suppressed = false
  Type = 0
FEATURE [Sketcher::SketchObject] Sketch052  label="bl narrow cable crs"
  ArcFitTolerance = 0
  AttachmentOffset = pos=(0,0,-80) rot=(0,0,1;0rad)
  AttachmentSupport = -> [XY_Plane014]
  FullyConstrained = true
  MakeInternals = false
  MapMode = 5
  Placement = pos=(0,0,-80) rot=(0,0,1;0rad)
  sketch-geometry (1):
    g0: Circle CenterX=0 CenterY=0 CenterZ=0 NormalX=0 NormalY=0 NormalZ=1 AngleXU=0 Radius=3
  constraints (2):
    c: Coincident(g0,g-1)
    c: Radius(g0) = 3
FEATURE [Sketcher::SketchObject] Sketch053  label="bl narrow cable trj"
  ArcFitTolerance = 0
  AttachmentSupport = -> [YZ_Plane015]
  FullyConstrained = true
  MakeInternals = false
  MapMode = 5
  Placement = pos=(0,0,0) rot=(0.57735,0.57735,0.57735;2.0944rad)
  sketch-geometry (4):
    g0: LineSegment StartX=0 StartY=-100 StartZ=0 EndX=0 EndY=-75 EndZ=0
    g1: ArcOfCircle CenterX=30.3125 CenterY=-75 CenterZ=0 NormalX=0 NormalY=0 NormalZ=1 AngleXU=0 Radius=30.3125 StartAngle=2.30514 EndAngle=3.14159
    g2: ArcOfCircle CenterX=-10.3125 CenterY=-30 CenterZ=0 NormalX=0 NormalY=0 NormalZ=1 AngleXU=0 Radius=30.3125 StartAngle=5.44674 EndAngle=6.28319
    g3: LineSegment StartX=20 StartY=0 StartZ=0 EndX=20 EndY=-30 EndZ=0
  constraints (12):
    c: PointOnObject(g0,g-2)
    c: PointOnObject(g0,g-2)
    c: DistanceY(g0,g-1) = 100
    c: Tangent(g0,g1) = 1.5708
    c: Tangent(g2,g1) = 1.5708
    c: DistanceY(g0,g-1) = 75
    c: PointOnObject(g3,g-1)
    c: Vertical(g3)
    c: DistanceX(g3) = 20
    c: Tangent(g2,g3) = 1.5708
    c: DistanceY(g3,g3) = 30
    c: Equal(g1,g2)
FEATURE [PartDesign::SubtractivePipe] SubtractivePipe001  label="BL Narrow cable channel"
  AuxilleryCurvelinear = true
  AuxillerySpineTangent = false
  BaseFeature = -> Pocket015
  Binormal = (0,0,0)
  Mode = 0
  Placement = pos=(0,0,0) rot=(1,0,0;1.5708rad)
  Profile = -> Sketch052
  Spine = -> Sketch053
  SpineTangent = false
  Suppressed = false
  Transformation = 0
  Transition = 0
FEATURE [Sketcher::SketchObject] Sketch054  label="bl wide cable trj"
  ArcFitTolerance = 0
  AttachmentSupport = -> [YZ_Plane015]
  ExternalGeometry = -> [Sketch053]
  FullyConstrained = true
  MakeInternals = false
  MapMode = 5
  Placement = pos=(0,0,0) rot=(0.57735,0.57735,0.57735;2.0944rad)
  sketch-geometry (2):
    g0: ArcOfCircle CenterX=-10.3125 CenterY=-30 CenterZ=0 NormalX=0 NormalY=0 NormalZ=1 AngleXU=0 Radius=30.3125 StartAngle=5.76553 EndAngle=6.28319
    g1: LineSegment StartX=20 StartY=-30 StartZ=0 EndX=20 EndY=3 EndZ=0
  constraints (6):
    c: Vertical(g1)
    c: Tangent(g0,g1) = -1.5708
    c: DistanceY(g0,g1) = 48
    c: Coincident(g-3,g0)
    c: PointOnObject(g-3,g1)
    c: DistanceY(g-1,g1) = 3
FEATURE [Sketcher::SketchObject] Sketch055  label="bl wide cable crs"
  ArcFitTolerance = 0
  AttachmentSupport = -> [XY_Plane014]
  FullyConstrained = true
  MakeInternals = false
  MapMode = 5
  sketch-geometry (4):
    g0: ArcOfCircle CenterX=-9 CenterY=20 CenterZ=0 NormalX=0 NormalY=0 NormalZ=1 AngleXU=0 Radius=3.5 StartAngle=1.5708 EndAngle=4.71239
    g1: ArcOfCircle CenterX=9 CenterY=20 CenterZ=0 NormalX=0 NormalY=0 NormalZ=1 AngleXU=0 Radius=3.5 StartAngle=4.71239 EndAngle=7.85398
    g2: LineSegment StartX=-9 StartY=16.5 StartZ=0 EndX=9 EndY=16.5 EndZ=0
    g3: LineSegment StartX=-9 StartY=23.5 StartZ=0 EndX=9 EndY=23.5 EndZ=0
  constraints (9):
    c: Tangent(g0,g3)
    c: Tangent(g0,g2)
    c: Tangent(g2,g1)
    c: Tangent(g3,g1)
    c: Horizontal(g2)
    c: Symmetric(g1,g0,g-2)
    c: DistanceY(g1) = 20
    c: DistanceX(g3,g3) = 18
    c: Radius(g1) = 3.5
FEATURE [PartDesign::SubtractivePipe] SubtractivePipe002  label="BL Wide cable channel"
  AuxilleryCurvelinear = true
  AuxillerySpineTangent = false
  BaseFeature = -> SubtractivePipe001
  Binormal = (0,0,0)
  Mode = 0
  Placement = pos=(0,0,0) rot=(1,0,0;1.5708rad)
  Profile = -> Sketch055
  Spine = -> Sketch054
  SpineTangent = false
  Suppressed = false
  Transformation = 0
  Transition = 0
FEATURE [Sketcher::SketchObject] Sketch056  label="bl large cable channel"
  ArcFitTolerance = 0
  AttachmentSupport = -> [XZ_Plane014]
  FullyConstrained = true
  MakeInternals = false
  MapMode = 5
  Placement = pos=(0,0,0) rot=(1,0,0;1.5708rad)
  sketch-geometry (6):
    g0: LineSegment StartX=-11 StartY=4 StartZ=0 EndX=11 EndY=4 EndZ=0
    g1: LineSegment StartX=11 StartY=4 StartZ=0 EndX=11 EndY=-14 EndZ=0
    g2: LineSegment StartX=7 StartY=-18 StartZ=0 EndX=-7 EndY=-18 EndZ=0
    g3: LineSegment StartX=-11 StartY=-14 StartZ=0 EndX=-11 EndY=4 EndZ=0
    g4: ArcOfCircle CenterX=-7 CenterY=-14 CenterZ=0 NormalX=0 NormalY=0 NormalZ=1 AngleXU=0 Radius=4 StartAngle=3.14159 EndAngle=4.71239
    g5: ArcOfCircle CenterX=7 CenterY=-14 CenterZ=0 NormalX=0 NormalY=0 NormalZ=1 AngleXU=0 Radius=4 StartAngle=4.71239 EndAngle=6.28319
  constraints (15):
    c: Coincident(g0,g1)
    c: Coincident(g3,g0)
    c: Horizontal(g2)
    c: Vertical(g1)
    c: Vertical(g3)
    c: Symmetric(g0,g0,g-2)
    c: DistanceX(g0,g0) = 22
    c: Tangent(g3,g4) = 1.5708
    c: Tangent(g2,g4) = 1.5708
    c: Tangent(g2,g5) = 1.5708
    c: Tangent(g1,g5) = 1.5708
    c: Equal(g5,g4)
    c: DistanceY(g2,g-1) = 18
    c: Radius(g5) = 4
    c: DistanceY(g0) = 4
FEATURE [PartDesign::Pocket] Pocket016  label="BL Large cable channel"
  BaseFeature = -> SubtractivePipe002
  Direction = (0,1,-2e-16)
  Length = 40
  Length2 = 100
  Midplane = true
  Placement = pos=(0,0,0) rot=(1,0,0;1.5708rad)
  Profile = -> Sketch056
  Suppressed = false
  Type = 0
FEATURE [Sketcher::SketchObject] Sketch057
  ArcFitTolerance = 0
  AttachmentSupport = -> [XZ_Plane016]
  FullyConstrained = true
  MakeInternals = false
  MapMode = 5
  Placement = pos=(0,0,0) rot=(1,0,0;1.5708rad)
  sketch-geometry (5):
    g0: LineSegment StartX=0 StartY=0 StartZ=0 EndX=0 EndY=-16 EndZ=0
    g1: LineSegment StartX=0 StartY=-16 StartZ=0 EndX=1.5 EndY=-1.25 EndZ=0
    g2: LineSegment StartX=1.5 StartY=-1.25 StartZ=0 EndX=2.65 EndY=-0.1 EndZ=0
    g3: LineSegment StartX=2.65 StartY=0 StartZ=0 EndX=0 EndY=0 EndZ=0
    g4: LineSegment StartX=2.65 StartY=-0.1 StartZ=0 EndX=2.65 EndY=0 EndZ=0
  constraints (14):
    c: Coincident(g-1,g0)
    c: Vertical(g0)
    c: Coincident(g0,g1)
    c: Coincident(g1,g2)
    c: Coincident(g3,g0)
    c: DistanceY(g0,g0) = 16
    c: Angle(g3,g2) = 0.785398
    c: DistanceX(g0,g1) = 1.5
    c: Horizontal(g3)
    c: Coincident(g4,g2)
    c: Vertical(g4)
    c: Coincident(g3,g4)
    c: DistanceX(g3) = 2.65
    c: DistanceY(g4,g4) = 0.1
FEATURE [PartDesign::Revolution] Revolution010
  AllowMultiFace = false
  Angle = 360
  Angle2 = 60
  Axis = (-3e-16,3e-16,1)
  Base = (0,0,0)
  Placement = pos=(0,0,0) rot=(1,0,0;1.5708rad)
  Profile = -> Sketch057
  ReferenceAxis = -> Z_Axis016
  Reversed = true
  Suppressed = false
  Type = 0
FEATURE [Sketcher::SketchObject] Sketch058
  ArcFitTolerance = 0
  AttachmentSupport = -> [XZ_Plane016]
  FullyConstrained = true
  MakeInternals = false
  MapMode = 5
  Placement = pos=(0,0,0) rot=(1,0,0;1.5708rad)
  sketch-geometry (3):
    g0: LineSegment StartX=-2 StartY=0 StartZ=0 EndX=0 EndY=-2 EndZ=0
    g1: LineSegment StartX=0 StartY=-2 StartZ=0 EndX=2 EndY=0 EndZ=0
    g2: LineSegment StartX=2 StartY=0 StartZ=0 EndX=-2 EndY=0 EndZ=0
  constraints (9):
    c: PointOnObject(g0,g-1)
    c: Coincident(g0,g1)
    c: PointOnObject(g1,g-1)
    c: Coincident(g1,g2)
    c: Coincident(g2,g0)
    c: PointOnObject(g0,g-2)
    c: Equal(g1,g0)
    c: Perpendicular(g0,g1)
    c: DistanceX(g2,g2) = 4
FEATURE [PartDesign::Pocket] Pocket017
  AllowMultiFace = false
  BaseFeature = -> Revolution010
  Direction = (0,1,-2e-16)
  Length = 0.6
  Length2 = 100
  Midplane = true
  Placement = pos=(0,0,0) rot=(1,0,0;1.5708rad)
  Profile = -> Sketch058
  Suppressed = false
  Type = 0
FEATURE [PartDesign::PolarPattern] PolarPattern
  Angle = 90
  Axis = -> Z_Axis016
  BaseFeature = -> Pocket017
  Mode = 0
  Occurrences = 2
  Offset = 120
  Originals = -> [Pocket017]
  Placement = pos=(0,0,0) rot=(1,0,0;1.5708rad)
  Suppressed = false
  TransformMode = 0
FEATURE [PartDesign::Body] Body016  label="SelftappingScrew3.0x16_01"
  AllowCompound = false
  Group = -> [Sketch057,Revolution010,Sketch058,Pocket017,PolarPattern]
  Origin = -> Origin016
  Tip = -> PolarPattern
FEATURE [Part::Compound] Compound001  label="SelftappingScrew3.0x16 001"
  Links = -> [Body016]
  Placement = pos=(4,25,-50) rot=(0.57735,0.57735,0.57735;2.0944rad)
FEATURE [Sketcher::SketchObject] Sketch059
  ArcFitTolerance = 0
  AttachmentSupport = -> [XZ_Plane017]
  FullyConstrained = true
  MakeInternals = false
  MapMode = 5
  Placement = pos=(0,0,0) rot=(1,0,0;1.5708rad)
  sketch-geometry (5):
    g0: LineSegment StartX=0 StartY=0 StartZ=0 EndX=0 EndY=-16 EndZ=0
    g1: LineSegment StartX=0 StartY=-16 StartZ=0 EndX=1.5 EndY=-1.25 EndZ=0
    g2: LineSegment StartX=1.5 StartY=-1.25 StartZ=0 EndX=2.65 EndY=-0.1 EndZ=0
    g3: LineSegment StartX=2.65 StartY=0 StartZ=0 EndX=0 EndY=0 EndZ=0
    g4: LineSegment StartX=2.65 StartY=-0.1 StartZ=0 EndX=2.65 EndY=0 EndZ=0
  constraints (14):
    c: Coincident(g-1,g0)
    c: Vertical(g0)
    c: Coincident(g0,g1)
    c: Coincident(g1,g2)
    c: Coincident(g3,g0)
    c: DistanceY(g0,g0) = 16
    c: Angle(g3,g2) = 0.785398
    c: DistanceX(g0,g1) = 1.5
    c: Horizontal(g3)
    c: Coincident(g4,g2)
    c: Vertical(g4)
    c: Coincident(g3,g4)
    c: DistanceX(g3) = 2.65
    c: DistanceY(g4,g4) = 0.1
FEATURE [PartDesign::Revolution] Revolution011
  AllowMultiFace = false
  Angle = 360
  Angle2 = 60
  Axis = (-3e-16,3e-16,1)
  Base = (0,0,0)
  Placement = pos=(0,0,0) rot=(1,0,0;1.5708rad)
  Profile = -> Sketch059
  ReferenceAxis = -> Z_Axis017
  Reversed = true
  Suppressed = false
  Type = 0
FEATURE [Sketcher::SketchObject] Sketch060
  ArcFitTolerance = 0
  AttachmentSupport = -> [XZ_Plane017]
  FullyConstrained = true
  MakeInternals = false
  MapMode = 5
  Placement = pos=(0,0,0) rot=(1,0,0;1.5708rad)
  sketch-geometry (3):
    g0: LineSegment StartX=-2 StartY=0 StartZ=0 EndX=0 EndY=-2 EndZ=0
    g1: LineSegment StartX=0 StartY=-2 StartZ=0 EndX=2 EndY=0 EndZ=0
    g2: LineSegment StartX=2 StartY=0 StartZ=0 EndX=-2 EndY=0 EndZ=0
  constraints (9):
    c: PointOnObject(g0,g-1)
    c: Coincident(g0,g1)
    c: PointOnObject(g1,g-1)
    c: Coincident(g1,g2)
    c: Coincident(g2,g0)
    c: PointOnObject(g0,g-2)
    c: Equal(g1,g0)
    c: Perpendicular(g0,g1)
    c: DistanceX(g2,g2) = 4
FEATURE [PartDesign::Pocket] Pocket018
  AllowMultiFace = false
  BaseFeature = -> Revolution011
  Direction = (0,1,-2e-16)
  Length = 0.6
  Length2 = 100
  Midplane = true
  Placement = pos=(0,0,0) rot=(1,0,0;1.5708rad)
  Profile = -> Sketch060
  Suppressed = false
  Type = 0
FEATURE [PartDesign::PolarPattern] PolarPattern001
  Angle = 90
  Axis = -> Z_Axis017
  BaseFeature = -> Pocket018
  Mode = 0
  Occurrences = 2
  Offset = 120
  Originals = -> [Pocket018]
  Placement = pos=(0,0,0) rot=(1,0,0;1.5708rad)
  Suppressed = false
  TransformMode = 0
FEATURE [PartDesign::Body] Body017  label="SelftappingScrew3.0x16_002"
  AllowCompound = false
  Group = -> [Sketch059,Revolution011,Sketch060,Pocket018,PolarPattern001]
  Origin = -> Origin017
  Tip = -> PolarPattern001
FEATURE [Part::Compound] Compound002  label="SelftappingScrew3.0x16 002"
  Links = -> [Body017]
  Placement = pos=(4,-25,-40) rot=(0.57735,0.57735,0.57735;2.0944rad)
FEATURE [Sketcher::SketchObject] Sketch061
  ArcFitTolerance = 0
  AttachmentSupport = -> [XZ_Plane018]
  FullyConstrained = true
  MakeInternals = false
  MapMode = 5
  Placement = pos=(0,0,0) rot=(1,0,0;1.5708rad)
  sketch-geometry (5):
    g0: LineSegment StartX=0 StartY=0 StartZ=0 EndX=0 EndY=-16 EndZ=0
    g1: LineSegment StartX=0 StartY=-16 StartZ=0 EndX=1.5 EndY=-1.25 EndZ=0
    g2: LineSegment StartX=1.5 StartY=-1.25 StartZ=0 EndX=2.65 EndY=-0.1 EndZ=0
    g3: LineSegment StartX=2.65 StartY=0 StartZ=0 EndX=0 EndY=0 EndZ=0
    g4: LineSegment StartX=2.65 StartY=-0.1 StartZ=0 EndX=2.65 EndY=0 EndZ=0
  constraints (14):
    c: Coincident(g-1,g0)
    c: Vertical(g0)
    c: Coincident(g0,g1)
    c: Coincident(g1,g2)
    c: Coincident(g3,g0)
    c: DistanceY(g0,g0) = 16
    c: Angle(g3,g2) = 0.785398
    c: DistanceX(g0,g1) = 1.5
    c: Horizontal(g3)
    c: Coincident(g4,g2)
    c: Vertical(g4)
    c: Coincident(g3,g4)
    c: DistanceX(g3) = 2.65
    c: DistanceY(g4,g4) = 0.1
FEATURE [PartDesign::Revolution] Revolution012
  AllowMultiFace = false
  Angle = 360
  Angle2 = 60
  Axis = (-3e-16,3e-16,1)
  Base = (0,0,0)
  Placement = pos=(0,0,0) rot=(1,0,0;1.5708rad)
  Profile = -> Sketch061
  ReferenceAxis = -> Z_Axis018
  Reversed = true
  Suppressed = false
  Type = 0
FEATURE [Sketcher::SketchObject] Sketch062
  ArcFitTolerance = 0
  AttachmentSupport = -> [XZ_Plane018]
  FullyConstrained = true
  MakeInternals = false
  MapMode = 5
  Placement = pos=(0,0,0) rot=(1,0,0;1.5708rad)
  sketch-geometry (3):
    g0: LineSegment StartX=-2 StartY=0 StartZ=0 EndX=0 EndY=-2 EndZ=0
    g1: LineSegment StartX=0 StartY=-2 StartZ=0 EndX=2 EndY=0 EndZ=0
    g2: LineSegment StartX=2 StartY=0 StartZ=0 EndX=-2 EndY=0 EndZ=0
  constraints (9):
    c: PointOnObject(g0,g-1)
    c: Coincident(g0,g1)
    c: PointOnObject(g1,g-1)
    c: Coincident(g1,g2)
    c: Coincident(g2,g0)
    c: PointOnObject(g0,g-2)
    c: Equal(g1,g0)
    c: Perpendicular(g0,g1)
    c: DistanceX(g2,g2) = 4
FEATURE [PartDesign::Pocket] Pocket019
  AllowMultiFace = false
  BaseFeature = -> Revolution012
  Direction = (0,1,-2e-16)
  Length = 0.6
  Length2 = 100
  Midplane = true
  Placement = pos=(0,0,0) rot=(1,0,0;1.5708rad)
  Profile = -> Sketch062
  Suppressed = false
  Type = 0
FEATURE [PartDesign::PolarPattern] PolarPattern002
  Angle = 90
  Axis = -> Z_Axis018
  BaseFeature = -> Pocket019
  Mode = 0
  Occurrences = 2
  Offset = 120
  Originals = -> [Pocket019]
  Placement = pos=(0,0,0) rot=(1,0,0;1.5708rad)
  Suppressed = false
  TransformMode = 0
FEATURE [PartDesign::Body] Body018  label="SelftappingScrew3.0x16_003"
  AllowCompound = false
  Group = -> [Sketch061,Revolution012,Sketch062,Pocket019,PolarPattern002]
  Origin = -> Origin018
  Tip = -> PolarPattern002
FEATURE [Part::Compound] Compound003  label="SelftappingScrew3.0x16 003"
  Links = -> [Body018]
  Placement = pos=(4,-8,-70) rot=(0.57735,0.57735,0.57735;2.0944rad)
FEATURE [Sketcher::SketchObject] Sketch063  label="bl screwhole 003"
  ArcFitTolerance = 0
  AttachmentOffset = pos=(0,0,8) rot=(0,0,1;0rad)
  AttachmentSupport = -> [XZ_Plane014]
  FullyConstrained = true
  MakeInternals = false
  MapMode = 5
  Placement = pos=(0,-8,1.8e-15) rot=(1,0,0;1.5708rad)
  sketch-geometry (7):
    g0: LineSegment StartX=35 StartY=-67 StartZ=0 EndX=4.3 EndY=-67 EndZ=0
    g1: LineSegment StartX=4.3 StartY=-67 StartZ=0 EndX=3 EndY=-68.3 EndZ=0
    g2: LineSegment StartX=3 StartY=-68.3 StartZ=0 EndX=0 EndY=-68.3 EndZ=0
    g3: LineSegment StartX=0 StartY=-68.3 StartZ=0 EndX=-12 EndY=-70 EndZ=0
    g4: LineSegment StartX=-12 StartY=-70 StartZ=0 EndX=35 EndY=-70 EndZ=0
    g5: LineSegment StartX=35 StartY=-70 StartZ=0 EndX=35 EndY=-67 EndZ=0
    g6: LineSegment [constr] StartX=35 StartY=-70 StartZ=0 EndX=38 EndY=-70 EndZ=0
  constraints (21):
    c: Horizontal(g0)
    c: Coincident(g0,g1)
    c: Coincident(g1,g2)
    c: Horizontal(g2)
    c: Coincident(g2,g3)
    c: Coincident(g3,g4)
    c: Horizontal(g4)
    c: Coincident(g4,g5)
    c: Coincident(g5,g0)
    c: Vertical(g5)
    c: Coincident(g6,g4)
    c: Horizontal(g6)
    c: Equal(g5,g6)
    c: DistanceY(g6,g-1) = 70
    c: DistanceY(g4,g1) = 1.7
    c: Angle(g1,g2) = 2.35619
    c: DistanceX(g1) = 3
    c: DistanceY(g5,g5) = 3
    c: PointOnObject(g2,g-2)
    c: DistanceX(g3,g3) = 12
    c: DistanceX(g0) = 35
FEATURE [PartDesign::Groove] Groove002  label="BL Screwhole 003"
  Angle = 360
  Angle2 = 60
  Axis = (3,0,0)
  Base = (35,-8,-70)
  BaseFeature = -> Pocket016
  Placement = pos=(0,0,0) rot=(1,0,0;1.5708rad)
  Profile = -> Sketch063
  ReferenceAxis = -> Sketch063 [Axis]
  Reversed = true
  Suppressed = false
  Type = 0
FEATURE [Sketcher::SketchObject] Sketch064  label="bl screwhole 001"
  ArcFitTolerance = 0
  AttachmentOffset = pos=(0,0,-25) rot=(0,0,1;0rad)
  AttachmentSupport = -> [XZ_Plane014]
  FullyConstrained = true
  MakeInternals = false
  MapMode = 5
  Placement = pos=(0,25,-5.6e-15) rot=(1,0,0;1.5708rad)
  sketch-geometry (7):
    g0: LineSegment StartX=35 StartY=-47 StartZ=0 EndX=4.3 EndY=-47 EndZ=0
    g1: LineSegment StartX=4.3 StartY=-47 StartZ=0 EndX=3 EndY=-48.3 EndZ=0
    g2: LineSegment StartX=3 StartY=-48.3 StartZ=0 EndX=0 EndY=-48.3 EndZ=0
    g3: LineSegment StartX=0 StartY=-48.3 StartZ=0 EndX=-12 EndY=-50 EndZ=0
    g4: LineSegment StartX=-12 StartY=-50 StartZ=0 EndX=35 EndY=-50 EndZ=0
    g5: LineSegment StartX=35 StartY=-50 StartZ=0 EndX=35 EndY=-47 EndZ=0
    g6: LineSegment [constr] StartX=35 StartY=-50 StartZ=0 EndX=32 EndY=-50 EndZ=0
  constraints (21):
    c: Horizontal(g0)
    c: Coincident(g0,g1)
    c: Coincident(g1,g2)
    c: Horizontal(g2)
    c: Coincident(g2,g3)
    c: Coincident(g3,g4)
    c: Horizontal(g4)
    c: Coincident(g4,g5)
    c: Coincident(g5,g0)
    c: Vertical(g5)
    c: Coincident(g6,g4)
    c: Horizontal(g6)
    c: Equal(g5,g6)
    c: DistanceY(g6,g-1) = 50
    c: DistanceY(g4,g1) = 1.7
    c: Angle(g1,g2) = 2.35619
    c: DistanceX(g1) = 3
    c: DistanceY(g5,g5) = 3
    c: PointOnObject(g2,g-2)
    c: DistanceX(g3,g3) = 12
    c: DistanceX(g0) = 35
FEATURE [PartDesign::Groove] Groove003  label="BL Screwhole 001"
  Angle = 360
  Angle2 = 60
  Axis = (-3,0,0)
  Base = (35,25,-50)
  BaseFeature = -> Groove002
  Placement = pos=(0,0,0) rot=(1,0,0;1.5708rad)
  Profile = -> Sketch064
  ReferenceAxis = -> Sketch064 [Axis]
  Suppressed = false
  Type = 0
FEATURE [Sketcher::SketchObject] Sketch065  label="bl screwhole 002"
  ArcFitTolerance = 0
  AttachmentOffset = pos=(0,0,25) rot=(0,0,1;0rad)
  AttachmentSupport = -> [XZ_Plane014]
  FullyConstrained = true
  MakeInternals = false
  MapMode = 5
  Placement = pos=(0,-25,5.6e-15) rot=(1,0,0;1.5708rad)
  sketch-geometry (7):
    g0: LineSegment StartX=35 StartY=-37 StartZ=0 EndX=4.3 EndY=-37 EndZ=0
    g1: LineSegment StartX=4.3 StartY=-37 StartZ=0 EndX=3 EndY=-38.3 EndZ=0
    g2: LineSegment StartX=3 StartY=-38.3 StartZ=0 EndX=0 EndY=-38.3 EndZ=0
    g3: LineSegment StartX=0 StartY=-38.3 StartZ=0 EndX=-12 EndY=-40 EndZ=0
    g4: LineSegment StartX=-12 StartY=-40 StartZ=0 EndX=35 EndY=-40 EndZ=0
    g5: LineSegment StartX=35 StartY=-40 StartZ=0 EndX=35 EndY=-37 EndZ=0
    g6: LineSegment [constr] StartX=35 StartY=-40 StartZ=0 EndX=32 EndY=-40 EndZ=0
  constraints (21):
    c: Horizontal(g0)
    c: Coincident(g0,g1)
    c: Coincident(g1,g2)
    c: Horizontal(g2)
    c: Coincident(g2,g3)
    c: Coincident(g3,g4)
    c: Horizontal(g4)
    c: Coincident(g4,g5)
    c: Coincident(g5,g0)
    c: Vertical(g5)
    c: Coincident(g6,g4)
    c: Horizontal(g6)
    c: Equal(g5,g6)
    c: DistanceY(g6,g-1) = 40
    c: DistanceY(g4,g1) = 1.7
    c: Angle(g1,g2) = 2.35619
    c: DistanceX(g1) = 3
    c: DistanceY(g5,g5) = 3
    c: PointOnObject(g2,g-2)
    c: DistanceX(g3,g3) = 12
    c: DistanceX(g0) = 35
FEATURE [PartDesign::Groove] Groove004  label="BL Screwhole 002"
  Angle = 360
  Angle2 = 60
  Axis = (-3,0,0)
  Base = (35,-25,-40)
  BaseFeature = -> Groove003
  Placement = pos=(0,0,0) rot=(1,0,0;1.5708rad)
  Profile = -> Sketch065
  ReferenceAxis = -> Sketch065 [Axis]
  Suppressed = false
  Type = 0
FEATURE [Sketcher::SketchObject] Sketch066  label="bl cutout left half"
  ArcFitTolerance = 0
  AttachmentSupport = -> [XZ_Plane014]
  FullyConstrained = true
  MakeInternals = false
  MapMode = 5
  Placement = pos=(0,0,0) rot=(1,0,0;1.5708rad)
  sketch-geometry (4):
    g0: LineSegment StartX=35 StartY=5 StartZ=0 EndX=-0.5 EndY=5 EndZ=0
    g1: LineSegment StartX=-0.5 StartY=5 StartZ=0 EndX=-0.5 EndY=-80 EndZ=0
    g2: LineSegment StartX=-0.5 StartY=-80 StartZ=0 EndX=35 EndY=-80 EndZ=0
    g3: LineSegment StartX=35 StartY=-80 StartZ=0 EndX=35 EndY=5 EndZ=0
  constraints (12):
    c: Coincident(g0,g1)
    c: Coincident(g1,g2)
    c: Coincident(g2,g3)
    c: Coincident(g3,g0)
    c: Horizontal(g0)
    c: Horizontal(g2)
    c: Vertical(g1)
    c: Vertical(g3)
    c: DistanceX(g1,g-1) = 0.5
    c: DistanceY(g2,g-1) = 80
    c: DistanceY(g0) = 5
    c: DistanceX(g0) = 35
FEATURE [PartDesign::Pocket] Pocket020  label="BL Cutout Left"
  BaseFeature = -> Groove004
  Direction = (0,1,-2e-16)
  Length = 5
  Length2 = 100
  Midplane = true
  Placement = pos=(0,0,0) rot=(1,0,0;1.5708rad)
  Profile = -> Sketch066
  Suppressed = false
  Type = 1
FEATURE [Sketcher::SketchObject] Sketch067  label="bl groove trj"
  ArcFitTolerance = 0
  AttachmentSupport = -> [YZ_Plane015]
  FullyConstrained = true
  MakeInternals = false
  MapMode = 5
  Placement = pos=(0,0,0) rot=(0.57735,0.57735,0.57735;2.0944rad)
  sketch-geometry (4):
    g0: LineSegment StartX=-28.5 StartY=4 StartZ=0 EndX=-28.5 EndY=-47 EndZ=0
    g1: ArcOfCircle CenterX=2e-16 CenterY=-47 CenterZ=0 NormalX=0 NormalY=0 NormalZ=1 AngleXU=0 Radius=28.5 StartAngle=3.14159 EndAngle=6.28319
    g2: LineSegment StartX=28.5 StartY=4 StartZ=0 EndX=28.5 EndY=-47 EndZ=0
    g3: ArcOfCircle CenterX=0 CenterY=4 CenterZ=0 NormalX=0 NormalY=0 NormalZ=1 AngleXU=0 Radius=28.5 StartAngle=0 EndAngle=3.14159
  constraints (11):
    c: Vertical(g0)
    c: Vertical(g2)
    c: PointOnObject(g3,g-2)
    c: Tangent(g0,g3) = -1.5708
    c: Tangent(g2,g3) = 1.5708
    c: Radius(g3) = 28.5
    c: Tangent(g0,g1) = -1.5708
    c: Horizontal(g2,g0)
    c: Coincident(g1,g2)
    c: DistanceY(g2,g2) = 51
    c: DistanceY(g1,g-1) = 47
FEATURE [Sketcher::SketchObject] Sketch068  label="bl groove crs"
  ArcFitTolerance = 0
  AttachmentSupport = -> [XY_Plane014]
  FullyConstrained = true
  MakeInternals = false
  MapMode = 5
  sketch-geometry (5):
    g0: LineSegment StartX=0 StartY=29.9284 StartZ=0 EndX=-2 EndY=29.1 EndZ=0
    g1: LineSegment StartX=-2 StartY=29.1 StartZ=0 EndX=-2 EndY=27.9 EndZ=0
    g2: LineSegment StartX=-2 StartY=27.9 StartZ=0 EndX=1.95151e-11 EndY=27.0716 EndZ=0
    g3: LineSegment StartX=1.95151e-11 StartY=27.0716 StartZ=0 EndX=0 EndY=29.9284 EndZ=0
    g4: LineSegment [constr] StartX=-2 StartY=28.5 StartZ=0 EndX=9.7575e-12 EndY=28.5 EndZ=0
  constraints (14):
    c: PointOnObject(g0,g-2)
    c: Coincident(g0,g1)
    c: Vertical(g1)
    c: Coincident(g1,g2)
    c: Coincident(g2,g3)
    c: Coincident(g3,g0)
    c: PointOnObject(g4,g1)
    c: PointOnObject(g4,g3)
    c: DistanceY(g4) = 28.5
    c: Symmetric(g2,g0,g4)
    c: Symmetric(g1,g0,g4)
    c: DistanceY(g1,g1) = 1.2
    c: Angle(g2,g0) = 0.785398
    c: DistanceX(g0,g0) = 2
FEATURE [PartDesign::SubtractivePipe] SubtractivePipe003
  AuxilleryCurvelinear = true
  AuxillerySpineTangent = false
  BaseFeature = -> Pocket020
  Binormal = (0,0,0)
  Mode = 0
  Placement = pos=(0,0,0) rot=(1,0,0;1.5708rad)
  Profile = -> Sketch068
  Spine = -> Sketch067
  SpineTangent = false
  Suppressed = false
  Transformation = 0
  Transition = 0
FEATURE [PartDesign::Body] Body014  label="Body Left"
  AllowCompound = false
  Group = -> [Sketch033,Pad014,Sketch035,Sketch036,Sketch037,SubtractiveLoft,Pocket006,Sketch040,Pocket007,Sketch041,Pocket008,Mirrored003,Sketch042,Pocket009,Sketch043,Groove001,Mirrored004,Sketch044,Pocket010,Sketch045,Pocket011,Sketch046,Pocket012,Sketch047,Pocket013,Sketch048,Sketch049,SubtractivePipe,Sketch050,Pocket014,Sketch051,Pocket015,Sketch052,Sketch053,SubtractivePipe001,Sketch054,Sketch055,+14 more]
  Origin = -> Origin014
  Tip = -> SubtractivePipe003
FEATURE [Sketcher::SketchObject] Sketch069  label="bl screwhole 004"
  ArcFitTolerance = 0
  AttachmentOffset = pos=(0,0,8) rot=(0,0,1;0rad)
  AttachmentSupport = -> [XZ_Plane019]
  FullyConstrained = true
  MakeInternals = false
  MapMode = 5
  Placement = pos=(0,-8,1.8e-15) rot=(1,0,0;1.5708rad)
  sketch-geometry (7):
    g0: LineSegment StartX=35 StartY=-67 StartZ=0 EndX=4.3 EndY=-67 EndZ=0
    g1: LineSegment StartX=4.3 StartY=-67 StartZ=0 EndX=3 EndY=-68.3 EndZ=0
    g2: LineSegment StartX=3 StartY=-68.3 StartZ=0 EndX=0 EndY=-68.3 EndZ=0
    g3: LineSegment StartX=0 StartY=-68.3 StartZ=0 EndX=-12 EndY=-70 EndZ=0
    g4: LineSegment StartX=-12 StartY=-70 StartZ=0 EndX=35 EndY=-70 EndZ=0
    g5: LineSegment StartX=35 StartY=-70 StartZ=0 EndX=35 EndY=-67 EndZ=0
    g6: LineSegment [constr] StartX=35 StartY=-70 StartZ=0 EndX=38 EndY=-70 EndZ=0
  constraints (21):
    c: Horizontal(g0)
    c: Coincident(g0,g1)
    c: Coincident(g1,g2)
    c: Horizontal(g2)
    c: Coincident(g2,g3)
    c: Coincident(g3,g4)
    c: Horizontal(g4)
    c: Coincident(g4,g5)
    c: Coincident(g5,g0)
    c: Vertical(g5)
    c: Coincident(g6,g4)
    c: Horizontal(g6)
    c: Equal(g5,g6)
    c: DistanceY(g6,g-1) = 70
    c: DistanceY(g4,g1) = 1.7
    c: Angle(g1,g2) = 2.35619
    c: DistanceX(g1) = 3
    c: DistanceY(g5,g5) = 3
    c: PointOnObject(g2,g-2)
    c: DistanceX(g3,g3) = 12
    c: DistanceX(g0) = 35
FEATURE [Sketcher::SketchObject] Sketch070  label="bl usb recess trj001"
  ArcFitTolerance = 0
  AttachmentSupport = -> [XZ_Plane019]
  FullyConstrained = true
  MakeInternals = false
  MapMode = 5
  Placement = pos=(0,0,0) rot=(1,0,0;1.5708rad)
  sketch-geometry (3):
    g0: ArcOfCircle CenterX=42.5 CenterY=-38.5 CenterZ=0 NormalX=0 NormalY=0 NormalZ=1 AngleXU=0 Radius=16 StartAngle=1.5708 EndAngle=3.14159
    g1: ArcOfCircle CenterX=42.5 CenterY=-45 CenterZ=0 NormalX=0 NormalY=0 NormalZ=1 AngleXU=0 Radius=16 StartAngle=3.14159 EndAngle=4.71239
    g2: LineSegment StartX=26.5 StartY=-38.5 StartZ=0 EndX=26.5 EndY=-45 EndZ=0
  constraints (10):
    c: Vertical(g2)
    c: DistanceX(g2) = 26.5
    c: Tangent(g0,g2) = -1.5708
    c: Tangent(g1,g2) = -1.5708
    c: DistanceY(g0,g-1) = 38.5
    c: DistanceY(g2,g2) = 6.5
    c: Radius(g1) = 16
    c: Equal(g1,g0)
    c: Vertical(g1,g0)
    c: Vertical(g0,g0)
FEATURE [Sketcher::SketchObject] Sketch071  label="bl usb recess crs001"
  ArcFitTolerance = 0
  AttachmentOffset = pos=(0,0,-40) rot=(0,0,1;0rad)
  AttachmentSupport = -> [XY_Plane019]
  FullyConstrained = true
  MakeInternals = false
  MapMode = 5
  Placement = pos=(0,0,-40) rot=(0,0,1;0rad)
  sketch-geometry (4):
    g0: ArcOfCircle CenterX=38.5 CenterY=2 CenterZ=0 NormalX=0 NormalY=0 NormalZ=1 AngleXU=0 Radius=12 StartAngle=-3.6e-15 EndAngle=3.14159
    g1: ArcOfCircle CenterX=38.5 CenterY=-6 CenterZ=0 NormalX=0 NormalY=0 NormalZ=1 AngleXU=0 Radius=12 StartAngle=3.14159 EndAngle=6.28319
    g2: LineSegment StartX=26.5 StartY=2 StartZ=0 EndX=26.5 EndY=-6 EndZ=0
    g3: LineSegment StartX=50.5 StartY=2 StartZ=0 EndX=50.5 EndY=-6 EndZ=0
  constraints (10):
    c: Tangent(g0,g3)
    c: Tangent(g0,g2)
    c: Tangent(g2,g1)
    c: Tangent(g3,g1)
    c: Vertical(g2)
    c: Equal(g0,g1)
    c: DistanceX(g0) = 26.5
    c: DistanceY(g-1,g0) = 2
    c: DistanceY(g1,g-1) = 6
    c: Radius(g0) = 12
FEATURE [Sketcher::SketchObject] Sketch072  label="bl esp usb pocket001"
  ArcFitTolerance = 0
  AttachmentOffset = pos=(0,0,18) rot=(0,0,1;0rad)
  AttachmentSupport = -> [YZ_Plane020]
  FullyConstrained = true
  MakeInternals = false
  MapMode = 5
  Placement = pos=(18,0,0) rot=(0.57735,0.57735,0.57735;2.0944rad)
  sketch-geometry (4):
    g0: ArcOfCircle CenterX=-1.5 CenterY=-39.2 CenterZ=0 NormalX=0 NormalY=0 NormalZ=1 AngleXU=0 Radius=2 StartAngle=1.4e-15 EndAngle=3.14159
    g1: ArcOfCircle CenterX=-1.5 CenterY=-44.5 CenterZ=0 NormalX=0 NormalY=0 NormalZ=1 AngleXU=0 Radius=2 StartAngle=3.14159 EndAngle=6.28319
    g2: LineSegment StartX=-3.5 StartY=-39.2 StartZ=0 EndX=-3.5 EndY=-44.5 EndZ=0
    g3: LineSegment StartX=0.5 StartY=-39.2 StartZ=0 EndX=0.5 EndY=-44.5 EndZ=0
  constraints (10):
    c: Tangent(g0,g3)
    c: Tangent(g0,g2)
    c: Tangent(g2,g1)
    c: Tangent(g3,g1)
    c: Vertical(g2)
    c: Equal(g0,g1)
    c: Radius(g0) = 2
    c: DistanceY(g1,g0) = 5.3
    c: DistanceY(g0,g-1) = 39.2
    c: DistanceX(g0,g-1) = 1.5
FEATURE [Sketcher::SketchObject] Sketch074  label="bl esp antenna cutout001"
  ArcFitTolerance = 0
  AttachmentOffset = pos=(0,0,1.5) rot=(0,0,1;0rad)
  AttachmentSupport = -> [XZ_Plane019]
  FullyConstrained = true
  MakeInternals = false
  MapMode = 5
  Placement = pos=(0,-1.5,3e-16) rot=(1,0,0;1.5708rad)
  sketch-geometry (4):
    g0: LineSegment StartX=-13.7 StartY=-32 StartZ=0 EndX=-5.7 EndY=-32 EndZ=0
    g1: LineSegment StartX=-5.7 StartY=-32 StartZ=0 EndX=-5.7 EndY=-52.5 EndZ=0
    g2: LineSegment StartX=-5.7 StartY=-52.5 StartZ=0 EndX=-13.7 EndY=-52.5 EndZ=0
    g3: LineSegment StartX=-13.7 StartY=-52.5 StartZ=0 EndX=-13.7 EndY=-32 EndZ=0
  constraints (12):
    c: Coincident(g0,g1)
    c: Coincident(g1,g2)
    c: Coincident(g2,g3)
    c: Coincident(g3,g0)
    c: Horizontal(g0)
    c: Horizontal(g2)
    c: Vertical(g1)
    c: Vertical(g3)
    c: DistanceX(g0,g-1) = 13.7
    c: DistanceX(g0,g0) = 8
    c: DistanceY(g0,g-1) = 32
    c: DistanceY(g3,g3) = 20.5
FEATURE [Sketcher::SketchObject] Sketch075  label="bl relay cutout001"
  ArcFitTolerance = 0
  AttachmentSupport = -> [YZ_Plane020]
  FullyConstrained = true
  MakeInternals = false
  MapMode = 5
  Placement = pos=(0,0,0) rot=(0.57735,0.57735,0.57735;2.0944rad)
  sketch-geometry (6):
    g0: LineSegment StartX=-7.1 StartY=5 StartZ=0 EndX=-27 EndY=5 EndZ=0
    g1: LineSegment StartX=-27 StartY=5 StartZ=0 EndX=-27 EndY=-34.7 EndZ=0
    g2: LineSegment StartX=-19.1 StartY=-49.5 StartZ=0 EndX=-7.1 EndY=-49.5 EndZ=0
    g3: LineSegment StartX=-7.1 StartY=-49.5 StartZ=0 EndX=-7.1 EndY=5 EndZ=0
    g4: LineSegment StartX=-19.1 StartY=-34.7 StartZ=0 EndX=-27 EndY=-34.7 EndZ=0
    g5: LineSegment StartX=-19.1 StartY=-49.5 StartZ=0 EndX=-19.1 EndY=-34.7 EndZ=0
  constraints (18):
    c: Coincident(g0,g1)
    c: Coincident(g2,g3)
    c: Coincident(g3,g0)
    c: Horizontal(g0)
    c: Horizontal(g2)
    c: Vertical(g1)
    c: Vertical(g3)
    c: Coincident(g5,g4)
    c: Horizontal(g4)
    c: Vertical(g5)
    c: DistanceX(g2,g-1) = 7.1
    c: Coincident(g5,g2)
    c: Coincident(g4,g1)
    c: DistanceY(g2,g-1) = 49.5
    c: DistanceX(g2,g2) = 12
    c: DistanceY(g5,g5) = 14.8
    c: DistanceY(g0) = 5
    c: DistanceX(g0,g-1) = 27
FEATURE [Sketcher::SketchObject] Sketch076  label="bl narrow cable trj001"
  ArcFitTolerance = 0
  AttachmentSupport = -> [YZ_Plane020]
  FullyConstrained = true
  MakeInternals = false
  MapMode = 5
  Placement = pos=(0,0,0) rot=(0.57735,0.57735,0.57735;2.0944rad)
  sketch-geometry (4):
    g0: LineSegment StartX=0 StartY=-100 StartZ=0 EndX=0 EndY=-75 EndZ=0
    g1: ArcOfCircle CenterX=30.3125 CenterY=-75 CenterZ=0 NormalX=0 NormalY=0 NormalZ=1 AngleXU=0 Radius=30.3125 StartAngle=2.30514 EndAngle=3.14159
    g2: ArcOfCircle CenterX=-10.3125 CenterY=-30 CenterZ=0 NormalX=0 NormalY=0 NormalZ=1 AngleXU=0 Radius=30.3125 StartAngle=5.44674 EndAngle=6.28319
    g3: LineSegment StartX=20 StartY=0 StartZ=0 EndX=20 EndY=-30 EndZ=0
  constraints (12):
    c: PointOnObject(g0,g-2)
    c: PointOnObject(g0,g-2)
    c: DistanceY(g0,g-1) = 100
    c: Tangent(g0,g1) = 1.5708
    c: Tangent(g2,g1) = 1.5708
    c: DistanceY(g0,g-1) = 75
    c: PointOnObject(g3,g-1)
    c: Vertical(g3)
    c: DistanceX(g3) = 20
    c: Tangent(g2,g3) = 1.5708
    c: DistanceY(g3,g3) = 30
    c: Equal(g1,g2)
FEATURE [Sketcher::SketchObject] Sketch077  label="bl wide cable trj001"
  ArcFitTolerance = 0
  AttachmentSupport = -> [YZ_Plane020]
  ExternalGeometry = -> [Sketch076]
  FullyConstrained = true
  MakeInternals = false
  MapMode = 5
  Placement = pos=(0,0,0) rot=(0.57735,0.57735,0.57735;2.0944rad)
  sketch-geometry (2):
    g0: ArcOfCircle CenterX=-10.3125 CenterY=-30 CenterZ=0 NormalX=0 NormalY=0 NormalZ=1 AngleXU=0 Radius=30.3125 StartAngle=5.76553 EndAngle=6.28319
    g1: LineSegment StartX=20 StartY=-30 StartZ=0 EndX=20 EndY=3 EndZ=0
  constraints (6):
    c: Vertical(g1)
    c: Tangent(g0,g1) = -1.5708
    c: DistanceY(g0,g1) = 48
    c: Coincident(g-3,g0)
    c: PointOnObject(g-3,g1)
    c: DistanceY(g-1,g1) = 3
FEATURE [Sketcher::SketchObject] Sketch078  label="bl narrow cable crs001"
  ArcFitTolerance = 0
  AttachmentOffset = pos=(0,0,-80) rot=(0,0,1;0rad)
  AttachmentSupport = -> [XY_Plane019]
  FullyConstrained = true
  MakeInternals = false
  MapMode = 5
  Placement = pos=(0,0,-80) rot=(0,0,1;0rad)
  sketch-geometry (1):
    g0: Circle CenterX=0 CenterY=0 CenterZ=0 NormalX=0 NormalY=0 NormalZ=1 AngleXU=0 Radius=3
  constraints (2):
    c: Coincident(g0,g-1)
    c: Radius(g0) = 3
FEATURE [Sketcher::SketchObject] Sketch079  label="bl screwhole 005"
  ArcFitTolerance = 0
  AttachmentOffset = pos=(0,0,-25) rot=(0,0,1;0rad)
  AttachmentSupport = -> [XZ_Plane019]
  FullyConstrained = true
  MakeInternals = false
  MapMode = 5
  Placement = pos=(0,25,-5.6e-15) rot=(1,0,0;1.5708rad)
  sketch-geometry (7):
    g0: LineSegment StartX=35 StartY=-47 StartZ=0 EndX=4.3 EndY=-47 EndZ=0
    g1: LineSegment StartX=4.3 StartY=-47 StartZ=0 EndX=3 EndY=-48.3 EndZ=0
    g2: LineSegment StartX=3 StartY=-48.3 StartZ=0 EndX=0 EndY=-48.3 EndZ=0
    g3: LineSegment StartX=0 StartY=-48.3 StartZ=0 EndX=-12 EndY=-50 EndZ=0
    g4: LineSegment StartX=-12 StartY=-50 StartZ=0 EndX=35 EndY=-50 EndZ=0
    g5: LineSegment StartX=35 StartY=-50 StartZ=0 EndX=35 EndY=-47 EndZ=0
    g6: LineSegment [constr] StartX=35 StartY=-50 StartZ=0 EndX=32 EndY=-50 EndZ=0
  constraints (21):
    c: Horizontal(g0)
    c: Coincident(g0,g1)
    c: Coincident(g1,g2)
    c: Horizontal(g2)
    c: Coincident(g2,g3)
    c: Coincident(g3,g4)
    c: Horizontal(g4)
    c: Coincident(g4,g5)
    c: Coincident(g5,g0)
    c: Vertical(g5)
    c: Coincident(g6,g4)
    c: Horizontal(g6)
    c: Equal(g5,g6)
    c: DistanceY(g6,g-1) = 50
    c: DistanceY(g4,g1) = 1.7
    c: Angle(g1,g2) = 2.35619
    c: DistanceX(g1) = 3
    c: DistanceY(g5,g5) = 3
    c: PointOnObject(g2,g-2)
    c: DistanceX(g3,g3) = 12
    c: DistanceX(g0) = 35
FEATURE [Sketcher::SketchObject] Sketch080  label="bl large cable channel001"
  ArcFitTolerance = 0
  AttachmentSupport = -> [XZ_Plane019]
  FullyConstrained = true
  MakeInternals = false
  MapMode = 5
  Placement = pos=(0,0,0) rot=(1,0,0;1.5708rad)
  sketch-geometry (6):
    g0: LineSegment StartX=-11 StartY=4 StartZ=0 EndX=11 EndY=4 EndZ=0
    g1: LineSegment StartX=11 StartY=4 StartZ=0 EndX=11 EndY=-14 EndZ=0
    g2: LineSegment StartX=7 StartY=-18 StartZ=0 EndX=-7 EndY=-18 EndZ=0
    g3: LineSegment StartX=-11 StartY=-14 StartZ=0 EndX=-11 EndY=4 EndZ=0
    g4: ArcOfCircle CenterX=-7 CenterY=-14 CenterZ=0 NormalX=0 NormalY=0 NormalZ=1 AngleXU=0 Radius=4 StartAngle=3.14159 EndAngle=4.71239
    g5: ArcOfCircle CenterX=7 CenterY=-14 CenterZ=0 NormalX=0 NormalY=0 NormalZ=1 AngleXU=0 Radius=4 StartAngle=4.71239 EndAngle=6.28319
  constraints (15):
    c: Coincident(g0,g1)
    c: Coincident(g3,g0)
    c: Horizontal(g2)
    c: Vertical(g1)
    c: Vertical(g3)
    c: Symmetric(g0,g0,g-2)
    c: DistanceX(g0,g0) = 22
    c: Tangent(g3,g4) = 1.5708
    c: Tangent(g2,g4) = 1.5708
    c: Tangent(g2,g5) = 1.5708
    c: Tangent(g1,g5) = 1.5708
    c: Equal(g5,g4)
    c: DistanceY(g2,g-1) = 18
    c: Radius(g5) = 4
    c: DistanceY(g0) = 4
FEATURE [Sketcher::SketchObject] Sketch081  label="bl wide cable crs001"
  ArcFitTolerance = 0
  AttachmentSupport = -> [XY_Plane019]
  FullyConstrained = true
  MakeInternals = false
  MapMode = 5
  sketch-geometry (4):
    g0: ArcOfCircle CenterX=-9 CenterY=20 CenterZ=0 NormalX=0 NormalY=0 NormalZ=1 AngleXU=0 Radius=3.5 StartAngle=1.5708 EndAngle=4.71239
    g1: ArcOfCircle CenterX=9 CenterY=20 CenterZ=0 NormalX=0 NormalY=0 NormalZ=1 AngleXU=0 Radius=3.5 StartAngle=4.71239 EndAngle=7.85398
    g2: LineSegment StartX=-9 StartY=16.5 StartZ=0 EndX=9 EndY=16.5 EndZ=0
    g3: LineSegment StartX=-9 StartY=23.5 StartZ=0 EndX=9 EndY=23.5 EndZ=0
  constraints (9):
    c: Tangent(g0,g3)
    c: Tangent(g0,g2)
    c: Tangent(g2,g1)
    c: Tangent(g3,g1)
    c: Horizontal(g2)
    c: Symmetric(g1,g0,g-2)
    c: DistanceY(g1) = 20
    c: DistanceX(g3,g3) = 18
    c: Radius(g1) = 3.5
FEATURE [Sketcher::SketchObject] Sketch082  label="bl base001"
  ArcFitTolerance = 0
  AttachmentSupport = -> [XZ_Plane019]
  FullyConstrained = true
  MakeInternals = false
  MapMode = 5
  Placement = pos=(0,0,0) rot=(1,0,0;1.5708rad)
  sketch-geometry (4):
    g0: LineSegment StartX=-30.5 StartY=2 StartZ=0 EndX=30.5 EndY=2 EndZ=0
    g1: LineSegment StartX=30.5 StartY=2 StartZ=0 EndX=30.5 EndY=-78 EndZ=0
    g2: LineSegment StartX=30.5 StartY=-78 StartZ=0 EndX=-30.5 EndY=-78 EndZ=0
    g3: LineSegment StartX=-30.5 StartY=-78 StartZ=0 EndX=-30.5 EndY=2 EndZ=0
  constraints (11):
    c: Coincident(g0,g1)
    c: Coincident(g1,g2)
    c: Coincident(g2,g3)
    c: Coincident(g3,g0)
    c: Horizontal(g2)
    c: Vertical(g1)
    c: Vertical(g3)
    c: Symmetric(g0,g0,g-2)
    c: DistanceY(g0) = 2
    c: DistanceX(g0,g0) = 61
    c: DistanceY(g1,g1) = 80
FEATURE [PartDesign::Pad] Pad015  label="BL Base001"
  Direction = (0,-1,2e-16)
  Length = 61
  Length2 = 100
  Midplane = true
  Placement = pos=(0,0,0) rot=(1,0,0;1.5708rad)
  Profile = -> Sketch082
  Suppressed = false
  Type = 0
FEATURE [Sketcher::SketchObject] Sketch083  label="bm side -081"
  ArcFitTolerance = 0
  AttachmentOffset = pos=(0,0,-45) rot=(0,0,1;0rad)
  AttachmentSupport = -> [XY_Plane019]
  FullyConstrained = true
  MakeInternals = false
  MapMode = 5
  Placement = pos=(0,0,-45) rot=(0,0,1;0rad)
  sketch-geometry (16):
    g0: LineSegment StartX=-22.5 StartY=30.5 StartZ=0 EndX=22.5 EndY=30.5 EndZ=0
    g1: LineSegment StartX=30.5 StartY=22.5 StartZ=0 EndX=30.5 EndY=-22.5 EndZ=0
    g2: LineSegment StartX=22.5 StartY=-30.5 StartZ=0 EndX=-22.5 EndY=-30.5 EndZ=0
    g3: LineSegment StartX=-30.5 StartY=-22.5 StartZ=0 EndX=-30.5 EndY=22.5 EndZ=0
    g4: ArcOfCircle CenterX=22.5 CenterY=22.5 CenterZ=0 NormalX=0 NormalY=0 NormalZ=1 AngleXU=0 Radius=8 StartAngle=1e-16 EndAngle=1.5708
    g5: ArcOfCircle CenterX=22.5 CenterY=-22.5 CenterZ=0 NormalX=0 NormalY=0 NormalZ=1 AngleXU=0 Radius=8 StartAngle=4.71239 EndAngle=6.28319
    g6: ArcOfCircle CenterX=-22.5 CenterY=-22.5 CenterZ=0 NormalX=0 NormalY=0 NormalZ=1 AngleXU=0 Radius=8 StartAngle=3.14159 EndAngle=4.71239
    g7: ArcOfCircle CenterX=-22.5 CenterY=22.5 CenterZ=0 NormalX=0 NormalY=0 NormalZ=1 AngleXU=0 Radius=8 StartAngle=1.5708 EndAngle=3.14159
    g8: LineSegment [constr] StartX=-22.5 StartY=22.5 StartZ=0 EndX=22.5 EndY=22.5 EndZ=0
    g9: LineSegment [constr] StartX=22.5 StartY=22.5 StartZ=0 EndX=22.5 EndY=-22.5 EndZ=0
    g10: LineSegment [constr] StartX=22.5 StartY=-22.5 StartZ=0 EndX=-22.5 EndY=-22.5 EndZ=0
    g11: LineSegment [constr] StartX=-22.5 StartY=-22.5 StartZ=0 EndX=-22.5 EndY=22.5 EndZ=0
    g12: LineSegment StartX=-32.5 StartY=32.5 StartZ=0 EndX=32.5 EndY=32.5 EndZ=0
    g13: LineSegment StartX=32.5 StartY=32.5 StartZ=0 EndX=32.5 EndY=-32.5 EndZ=0
    g14: LineSegment StartX=32.5 StartY=-32.5 StartZ=0 EndX=-32.5 EndY=-32.5 EndZ=0
    g15: LineSegment StartX=-32.5 StartY=-32.5 StartZ=0 EndX=-32.5 EndY=32.5 EndZ=0
  constraints (36):
    c: Horizontal(g0)
    c: Horizontal(g2)
    c: Vertical(g1)
    c: Vertical(g3)
    c: Tangent(g0,g4) = 1.5708
    c: Tangent(g1,g4) = 1.5708
    c: Tangent(g2,g5) = 1.5708
    c: Tangent(g1,g5) = 1.5708
    c: Tangent(g3,g6) = 1.5708
    c: Tangent(g2,g6) = 1.5708
    c: Tangent(g0,g7) = 1.5708
    c: Tangent(g3,g7) = 1.5708
    c: Coincident(g8,g9)
    c: Coincident(g9,g10)
    c: Coincident(g10,g11)
    c: Coincident(g11,g8)
    c: Horizontal(g10)
    c: Coincident(g8,g7)
    c: Coincident(g9,g5)
    c: Coincident(g4,g8)
    c: Coincident(g6,g10)
    c: DistanceX(g3,g1) = 61
    c: Radius(g4) = 8
    c: Equal(g9,g8)
    c: Symmetric(g4,g5,g-1)
    c: Symmetric(g4,g7,g-2)
    c: Coincident(g12,g13)
    c: Coincident(g13,g14)
    c: Coincident(g14,g15)
    c: Coincident(g15,g12)
    c: Horizontal(g14)
    c: Vertical(g15)
    c: Symmetric(g12,g13,g-1)
    c: Symmetric(g12,g12,g-2)
    c: Equal(g12,g13)
    c: DistanceX(g12,g12) = 65
FEATURE [Sketcher::SketchObject] Sketch084  label="bm side -082"
  ArcFitTolerance = 0
  AttachmentOffset = pos=(0,0,-50) rot=(0,0,1;0rad)
  AttachmentSupport = -> [XY_Plane019]
  FullyConstrained = true
  MakeInternals = false
  MapMode = 5
  Placement = pos=(0,0,-50) rot=(0,0,1;0rad)
  sketch-geometry (16):
    g0: LineSegment StartX=-18.5 StartY=30.5 StartZ=0 EndX=18.5 EndY=30.5 EndZ=0
    g1: LineSegment StartX=30.5 StartY=18.5 StartZ=0 EndX=30.5 EndY=-18.5 EndZ=0
    g2: LineSegment StartX=18.5 StartY=-30.5 StartZ=0 EndX=-18.5 EndY=-30.5 EndZ=0
    g3: LineSegment StartX=-30.5 StartY=-18.5 StartZ=0 EndX=-30.5 EndY=18.5 EndZ=0
    g4: ArcOfCircle CenterX=18.5 CenterY=18.5 CenterZ=0 NormalX=0 NormalY=0 NormalZ=1 AngleXU=0 Radius=12 StartAngle=0 EndAngle=1.5708
    g5: ArcOfCircle CenterX=18.5 CenterY=-18.5 CenterZ=0 NormalX=0 NormalY=0 NormalZ=1 AngleXU=0 Radius=12 StartAngle=4.71239 EndAngle=6.28319
    g6: ArcOfCircle CenterX=-18.5 CenterY=-18.5 CenterZ=0 NormalX=0 NormalY=0 NormalZ=1 AngleXU=0 Radius=12 StartAngle=3.14159 EndAngle=4.71239
    g7: ArcOfCircle CenterX=-18.5 CenterY=18.5 CenterZ=0 NormalX=0 NormalY=0 NormalZ=1 AngleXU=0 Radius=12 StartAngle=1.5708 EndAngle=3.14159
    g8: LineSegment [constr] StartX=-18.5 StartY=18.5 StartZ=0 EndX=18.5 EndY=18.5 EndZ=0
    g9: LineSegment [constr] StartX=18.5 StartY=18.5 StartZ=0 EndX=18.5 EndY=-18.5 EndZ=0
    g10: LineSegment [constr] StartX=18.5 StartY=-18.5 StartZ=0 EndX=-18.5 EndY=-18.5 EndZ=0
    g11: LineSegment [constr] StartX=-18.5 StartY=-18.5 StartZ=0 EndX=-18.5 EndY=18.5 EndZ=0
    g12: LineSegment StartX=-32.5 StartY=32.5 StartZ=0 EndX=32.5 EndY=32.5 EndZ=0
    g13: LineSegment StartX=32.5 StartY=32.5 StartZ=0 EndX=32.5 EndY=-32.5 EndZ=0
    g14: LineSegment StartX=32.5 StartY=-32.5 StartZ=0 EndX=-32.5 EndY=-32.5 EndZ=0
    g15: LineSegment StartX=-32.5 StartY=-32.5 StartZ=0 EndX=-32.5 EndY=32.5 EndZ=0
  constraints (36):
    c: Horizontal(g0)
    c: Horizontal(g2)
    c: Vertical(g1)
    c: Vertical(g3)
    c: Tangent(g0,g4) = 1.5708
    c: Tangent(g1,g4) = 1.5708
    c: Tangent(g2,g5) = 1.5708
    c: Tangent(g1,g5) = 1.5708
    c: Tangent(g3,g6) = 1.5708
    c: Tangent(g2,g6) = 1.5708
    c: Tangent(g0,g7) = 1.5708
    c: Tangent(g3,g7) = 1.5708
    c: Coincident(g8,g9)
    c: Coincident(g9,g10)
    c: Coincident(g10,g11)
    c: Coincident(g11,g8)
    c: Horizontal(g10)
    c: Coincident(g8,g7)
    c: Coincident(g9,g5)
    c: Coincident(g4,g8)
    c: Coincident(g6,g10)
    c: DistanceX(g3,g1) = 61
    c: Radius(g4) = 12
    c: Equal(g9,g8)
    c: Symmetric(g4,g5,g-1)
    c: Symmetric(g4,g7,g-2)
    c: Coincident(g12,g13)
    c: Coincident(g13,g14)
    c: Coincident(g14,g15)
    c: Coincident(g15,g12)
    c: Horizontal(g14)
    c: Vertical(g15)
    c: Symmetric(g12,g13,g-1)
    c: Symmetric(g12,g12,g-2)
    c: Equal(g12,g13)
    c: DistanceX(g12,g12) = 65
FEATURE [Sketcher::SketchObject] Sketch085  label="bl cutout notch wallsocket001"
  ArcFitTolerance = 0
  AttachmentOffset = pos=(0,0,-2) rot=(0,0,1;0rad)
  AttachmentSupport = -> [XY_Plane019]
  FullyConstrained = true
  MakeInternals = false
  MapMode = 5
  Placement = pos=(0,0,-2) rot=(0,0,1;0rad)
  sketch-geometry (12):
    g0: LineSegment StartX=13.6 StartY=7.6 StartZ=0 EndX=20.8 EndY=7.6 EndZ=0
    g1: LineSegment StartX=22 StartY=6.4 StartZ=0 EndX=22 EndY=-6.4 EndZ=0
    g2: LineSegment StartX=20.8 StartY=-7.6 StartZ=0 EndX=13.6 EndY=-7.6 EndZ=0
    g3: LineSegment StartX=12.4 StartY=-6.4 StartZ=0 EndX=12.4 EndY=6.4 EndZ=0
    g4: ArcOfCircle CenterX=13.6 CenterY=6.4 CenterZ=0 NormalX=0 NormalY=0 NormalZ=1 AngleXU=0 Radius=1.2 StartAngle=1.5708 EndAngle=3.14159
    g5: ArcOfCircle CenterX=20.8 CenterY=6.4 CenterZ=0 NormalX=0 NormalY=0 NormalZ=1 AngleXU=0 Radius=1.2 StartAngle=0 EndAngle=1.5708
    g6: ArcOfCircle CenterX=20.8 CenterY=-6.4 CenterZ=0 NormalX=0 NormalY=0 NormalZ=1 AngleXU=0 Radius=1.2 StartAngle=4.71239 EndAngle=6.28319
    g7: ArcOfCircle CenterX=13.6 CenterY=-6.4 CenterZ=0 NormalX=0 NormalY=0 NormalZ=1 AngleXU=0 Radius=1.2 StartAngle=3.14159 EndAngle=4.71239
    g8: LineSegment [constr] StartX=13.6 StartY=6.4 StartZ=0 EndX=20.8 EndY=6.4 EndZ=0
    g9: LineSegment [constr] StartX=20.8 StartY=6.4 StartZ=0 EndX=20.8 EndY=-6.4 EndZ=0
    g10: LineSegment [constr] StartX=20.8 StartY=-6.4 StartZ=0 EndX=13.6 EndY=-6.4 EndZ=0
    g11: LineSegment [constr] StartX=13.6 StartY=-6.4 StartZ=0 EndX=13.6 EndY=6.4 EndZ=0
  constraints (27):
    c: Horizontal(g0)
    c: Horizontal(g2)
    c: Vertical(g1)
    c: Vertical(g3)
    c: Tangent(g3,g4) = 1.5708
    c: Tangent(g0,g4) = 1.5708
    c: Tangent(g0,g5) = 1.5708
    c: Tangent(g1,g5) = 1.5708
    c: Tangent(g1,g6) = 1.5708
    c: Tangent(g2,g6) = 1.5708
    c: Tangent(g2,g7) = 1.5708
    c: Tangent(g3,g7) = 1.5708
    c: Coincident(g8,g9)
    c: Coincident(g9,g10)
    c: Coincident(g10,g11)
    c: Coincident(g11,g8)
    c: Horizontal(g8)
    c: Horizontal(g10)
    c: Coincident(g8,g4)
    c: Coincident(g9,g6)
    c: Coincident(g5,g8)
    c: Coincident(g7,g10)
    c: Symmetric(g5,g6,g-1)
    c: DistanceY(g2,g0) = 15.2
    c: DistanceX(g1) = 22
    c: DistanceX(g3,g1) = 9.6
    c: Radius(g5) = 1.2
FEATURE [Sketcher::SketchObject] Sketch086  label="bm side -083"
  ArcFitTolerance = 0
  AttachmentOffset = pos=(0,0,-80) rot=(0,0,1;0rad)
  AttachmentSupport = -> [XY_Plane019]
  FullyConstrained = true
  MakeInternals = false
  MapMode = 5
  Placement = pos=(0,0,-80) rot=(0,0,1;0rad)
  sketch-geometry (16):
    g0: LineSegment StartX=-0.1 StartY=8 StartZ=0 EndX=0.1 EndY=8 EndZ=0
    g1: LineSegment StartX=8 StartY=0.1 StartZ=0 EndX=8 EndY=-0.1 EndZ=0
    g2: LineSegment StartX=0.1 StartY=-8 StartZ=0 EndX=-0.1 EndY=-8 EndZ=0
    g3: LineSegment StartX=-8 StartY=-0.1 StartZ=0 EndX=-8 EndY=0.1 EndZ=0
    g4: ArcOfCircle CenterX=0.1 CenterY=0.1 CenterZ=0 NormalX=0 NormalY=0 NormalZ=1 AngleXU=0 Radius=7.9 StartAngle=0 EndAngle=1.5708
    g5: ArcOfCircle CenterX=0.1 CenterY=-0.1 CenterZ=0 NormalX=0 NormalY=0 NormalZ=1 AngleXU=0 Radius=7.9 StartAngle=4.71239 EndAngle=6.28319
    g6: ArcOfCircle CenterX=-0.1 CenterY=-0.1 CenterZ=0 NormalX=0 NormalY=0 NormalZ=1 AngleXU=0 Radius=7.9 StartAngle=3.14159 EndAngle=4.71239
    g7: ArcOfCircle CenterX=-0.1 CenterY=0.1 CenterZ=0 NormalX=0 NormalY=0 NormalZ=1 AngleXU=0 Radius=7.9 StartAngle=1.5708 EndAngle=3.14159
    g8: LineSegment [constr] StartX=-0.1 StartY=0.1 StartZ=0 EndX=0.1 EndY=0.1 EndZ=0
    g9: LineSegment [constr] StartX=0.1 StartY=0.1 StartZ=0 EndX=0.1 EndY=-0.1 EndZ=0
    g10: LineSegment [constr] StartX=0.1 StartY=-0.1 StartZ=0 EndX=-0.1 EndY=-0.1 EndZ=0
    g11: LineSegment [constr] StartX=-0.1 StartY=-0.1 StartZ=0 EndX=-0.1 EndY=0.1 EndZ=0
    g12: LineSegment StartX=-32.5 StartY=32.5 StartZ=0 EndX=32.5 EndY=32.5 EndZ=0
    g13: LineSegment StartX=32.5 StartY=32.5 StartZ=0 EndX=32.5 EndY=-32.5 EndZ=0
    g14: LineSegment StartX=32.5 StartY=-32.5 StartZ=0 EndX=-32.5 EndY=-32.5 EndZ=0
    g15: LineSegment StartX=-32.5 StartY=-32.5 StartZ=0 EndX=-32.5 EndY=32.5 EndZ=0
  constraints (36):
    c: Horizontal(g0)
    c: Horizontal(g2)
    c: Vertical(g1)
    c: Vertical(g3)
    c: Tangent(g0,g4) = 1.5708
    c: Tangent(g1,g4) = 1.5708
    c: Tangent(g2,g5) = 1.5708
    c: Tangent(g1,g5) = 1.5708
    c: Tangent(g3,g6) = 1.5708
    c: Tangent(g2,g6) = 1.5708
    c: Tangent(g0,g7) = 1.5708
    c: Tangent(g3,g7) = 1.5708
    c: Coincident(g8,g9)
    c: Coincident(g9,g10)
    c: Coincident(g10,g11)
    c: Coincident(g11,g8)
    c: Horizontal(g10)
    c: Coincident(g8,g7)
    c: Coincident(g9,g5)
    c: Coincident(g4,g8)
    c: Coincident(g6,g10)
    c: DistanceX(g3,g1) = 16
    c: Radius(g4) = 7.9
    c: Equal(g9,g8)
    c: Symmetric(g4,g5,g-1)
    c: Symmetric(g4,g7,g-2)
    c: Coincident(g12,g13)
    c: Coincident(g13,g14)
    c: Coincident(g14,g15)
    c: Coincident(g15,g12)
    c: Horizontal(g14)
    c: Vertical(g15)
    c: Symmetric(g12,g13,g-1)
    c: Symmetric(g12,g12,g-2)
    c: Equal(g12,g13)
    c: DistanceX(g12,g12) = 65
FEATURE [PartDesign::SubtractiveLoft] SubtractiveLoft001  label="BL Side rear001"
  BaseFeature = -> Pad015
  Closed = false
  Placement = pos=(0,0,0) rot=(1,0,0;1.5708rad)
  Profile = -> Sketch083
  Ruled = false
  Sections = -> [Sketch084,Sketch086]
  Suppressed = false
FEATURE [PartDesign::Pocket] Pocket027  label="BL Side front001"
  BaseFeature = -> SubtractiveLoft001
  Direction = (0,0,-1)
  Length = 5
  Length2 = 100
  Placement = pos=(0,0,0) rot=(1,0,0;1.5708rad)
  Profile = -> Sketch083
  Reversed = true
  Suppressed = false
  Type = 1
FEATURE [Sketcher::SketchObject] Sketch087  label="bl cutout wallsocket001"
  ArcFitTolerance = 0
  AttachmentSupport = -> [XY_Plane019]
  FullyConstrained = true
  MakeInternals = false
  MapMode = 5
  sketch-geometry (16):
    g0: LineSegment StartX=-22.7 StartY=25.8 StartZ=0 EndX=22.7 EndY=25.8 EndZ=0
    g1: LineSegment StartX=26.2 StartY=22.3 StartZ=0 EndX=26.2 EndY=-22.3 EndZ=0
    g2: LineSegment StartX=22.7 StartY=-25.8 StartZ=0 EndX=-22.7 EndY=-25.8 EndZ=0
    g3: LineSegment StartX=-26.2 StartY=-22.3 StartZ=0 EndX=-26.2 EndY=22.3 EndZ=0
    g4: ArcOfCircle CenterX=-22.7 CenterY=22.3 CenterZ=0 NormalX=0 NormalY=0 NormalZ=1 AngleXU=0 Radius=3.5 StartAngle=1.5708 EndAngle=3.14159
    g5: ArcOfCircle CenterX=22.7 CenterY=22.3 CenterZ=0 NormalX=0 NormalY=0 NormalZ=1 AngleXU=0 Radius=3.5 StartAngle=0 EndAngle=1.5708
    g6: ArcOfCircle CenterX=22.7 CenterY=-22.3 CenterZ=0 NormalX=0 NormalY=0 NormalZ=1 AngleXU=0 Radius=3.5 StartAngle=4.71239 EndAngle=6.28319
    g7: ArcOfCircle CenterX=-22.7 CenterY=-22.3 CenterZ=0 NormalX=0 NormalY=0 NormalZ=1 AngleXU=0 Radius=3.5 StartAngle=3.14159 EndAngle=4.71239
    g8: LineSegment [constr] StartX=-22.7 StartY=22.3 StartZ=0 EndX=22.7 EndY=22.3 EndZ=0
    g9: LineSegment [constr] StartX=22.7 StartY=22.3 StartZ=0 EndX=22.7 EndY=-22.3 EndZ=0
    g10: LineSegment [constr] StartX=22.7 StartY=-22.3 StartZ=0 EndX=-22.7 EndY=-22.3 EndZ=0
    g11: LineSegment [constr] StartX=-22.7 StartY=-22.3 StartZ=0 EndX=-22.7 EndY=22.3 EndZ=0
    g12: LineSegment StartX=-35 StartY=35 StartZ=0 EndX=35 EndY=35 EndZ=0
    g13: LineSegment StartX=35 StartY=35 StartZ=0 EndX=35 EndY=-35 EndZ=0
    g14: LineSegment StartX=35 StartY=-35 StartZ=0 EndX=-35 EndY=-35 EndZ=0
    g15: LineSegment StartX=-35 StartY=-35 StartZ=0 EndX=-35 EndY=35 EndZ=0
  constraints (36):
    c: Horizontal(g0)
    c: Horizontal(g2)
    c: Vertical(g1)
    c: Vertical(g3)
    c: Tangent(g3,g4) = 1.5708
    c: Tangent(g0,g4) = 1.5708
    c: Tangent(g0,g5) = 1.5708
    c: Tangent(g1,g5) = 1.5708
    c: Tangent(g1,g6) = 1.5708
    c: Tangent(g2,g6) = 1.5708
    c: Tangent(g3,g7) = 1.5708
    c: Tangent(g2,g7) = 1.5708
    c: Coincident(g8,g9)
    c: Coincident(g9,g10)
    c: Coincident(g10,g11)
    c: Coincident(g11,g8)
    c: Horizontal(g10)
    c: Coincident(g8,g4)
    c: Coincident(g9,g6)
    c: Coincident(g5,g8)
    c: Coincident(g7,g10)
    c: Symmetric(g4,g5,g-2)
    c: Symmetric(g5,g6,g-1)
    c: DistanceX(g3,g1) = 52.4
    c: DistanceY(g2,g0) = 51.6
    c: Radius(g5) = 3.5
    c: Coincident(g12,g13)
    c: Coincident(g13,g14)
    c: Coincident(g14,g15)
    c: Coincident(g15,g12)
    c: Horizontal(g14)
    c: Vertical(g15)
    c: Symmetric(g13,g12,g-1)
    c: Symmetric(g12,g12,g-2)
    c: Equal(g13,g12)
    c: DistanceX(g12,g12) = 70
FEATURE [PartDesign::Pocket] Pocket026  label="BL Cutout wallsocket001"
  BaseFeature = -> Pocket027
  Direction = (0,0,-1)
  Length = 5
  Length2 = 100
  Placement = pos=(0,0,0) rot=(1,0,0;1.5708rad)
  Profile = -> Sketch087
  Reversed = true
  Suppressed = false
  Type = 1
FEATURE [PartDesign::Pocket] Pocket029  label="BL cutout notch wallsocket R001"
  BaseFeature = -> Pocket026
  Direction = (0,0,-1)
  Length = 5
  Length2 = 100
  Placement = pos=(0,0,0) rot=(1,0,0;1.5708rad)
  Profile = -> Sketch085
  Reversed = true
  Suppressed = false
  Type = 1
FEATURE [PartDesign::Mirrored] Mirrored005  label="BL cutout notch wallsocket L001"
  BaseFeature = -> Pocket029
  MirrorPlane = -> YZ_Plane020
  Originals = -> [Pocket029]
  Placement = pos=(0,0,0) rot=(1,0,0;1.5708rad)
  Suppressed = false
  TransformMode = 0
FEATURE [Sketcher::SketchObject] Sketch088  label="bl stepper pocket001"
  ArcFitTolerance = 0
  AttachmentSupport = -> [XY_Plane019]
  FullyConstrained = true
  MakeInternals = false
  MapMode = 5
  sketch-geometry (12):
    g0: LineSegment StartX=-17.75 StartY=12.4 StartZ=0 EndX=-15.75 EndY=12.4 EndZ=0
    g1: LineSegment StartX=17.75 StartY=12.4 StartZ=0 EndX=17.75 EndY=9.9 EndZ=0
    g2: LineSegment StartX=17.75 StartY=9.9 StartZ=0 EndX=15 EndY=9.9 EndZ=0
    g3: LineSegment StartX=-17.75 StartY=9.9 StartZ=0 EndX=-17.75 EndY=12.4 EndZ=0
    g4: LineSegment StartX=-15.75 StartY=13.9 StartZ=0 EndX=15.75 EndY=13.9 EndZ=0
    g5: LineSegment StartX=15.75 StartY=13.9 StartZ=0 EndX=15.75 EndY=12.4 EndZ=0
    g6: LineSegment StartX=-15.75 StartY=12.4 StartZ=0 EndX=-15.75 EndY=13.9 EndZ=0
    g7: LineSegment StartX=15.75 StartY=12.4 StartZ=0 EndX=17.75 EndY=12.4 EndZ=0
    g8: LineSegment StartX=15 StartY=9.9 StartZ=0 EndX=15 EndY=0.9 EndZ=0
    g9: LineSegment StartX=15 StartY=0.9 StartZ=0 EndX=-12 EndY=0.9 EndZ=0
    g10: LineSegment StartX=-12 StartY=0.9 StartZ=0 EndX=-12 EndY=9.9 EndZ=0
    g11: LineSegment StartX=-12 StartY=9.9 StartZ=0 EndX=-17.75 EndY=9.9 EndZ=0
  constraints (32):
    c: Coincident(g7,g1)
    c: Coincident(g1,g2)
    c: Coincident(g11,g3)
    c: Coincident(g3,g0)
    c: Horizontal(g2)
    c: Vertical(g1)
    c: Vertical(g3)
    c: Symmetric(g7,g0,g-2)
    c: DistanceX(g0,g7) = 35.5
    c: DistanceY(g0) = 12.4
    c: DistanceY(g3,g3) = 2.5
    c: Coincident(g4,g5)
    c: Coincident(g6,g4)
    c: Vertical(g5)
    c: Vertical(g6)
    c: Symmetric(g4,g4,g-2)
    c: Tangent(g0,g7)
    c: Coincident(g0,g6)
    c: DistanceX(g0,g0) = 2
    c: DistanceY(g6,g6) = 1.5
    c: Coincident(g5,g7)
    c: Coincident(g8,g9)
    c: Coincident(g9,g10)
    c: Horizontal(g9)
    c: Vertical(g8)
    c: Vertical(g10)
    c: DistanceX(g8) = 15
    c: DistanceX(g10,g-1) = 12
    c: Tangent(g2,g11)
    c: Coincident(g10,g11)
    c: Coincident(g2,g8)
    c: DistanceY(g8,g8) = 9
FEATURE [Sketcher::SketchObject] Sketch089  label="bl nutslot001"
  ArcFitTolerance = 0
  AttachmentOffset = pos=(0,0,-5.7) rot=(0,0,1;0rad)
  AttachmentSupport = -> [XY_Plane019]
  FullyConstrained = true
  MakeInternals = false
  MapMode = 5
  Placement = pos=(0,0,-5.7) rot=(0,0,1;0rad)
  sketch-geometry (8):
    g0: LineSegment StartX=21.1218 StartY=3.675 StartZ=0 EndX=-21.1218 EndY=3.675 EndZ=0
    g1: LineSegment StartX=-21.1218 StartY=3.675 StartZ=0 EndX=-23.2435 EndY=9e-16 EndZ=0
    g2: LineSegment StartX=-23.2435 StartY=9e-16 StartZ=0 EndX=-21.1218 EndY=-3.675 EndZ=0
    g3: LineSegment StartX=-21.1218 StartY=-3.675 StartZ=0 EndX=21.1218 EndY=-3.675 EndZ=0
    g4: LineSegment StartX=21.1218 StartY=-3.675 StartZ=0 EndX=23.2435 EndY=0 EndZ=0
    g5: LineSegment StartX=23.2435 StartY=0 StartZ=0 EndX=21.1218 EndY=3.675 EndZ=0
    g6: Circle [constr] CenterX=-19 CenterY=0 CenterZ=0 NormalX=0 NormalY=0 NormalZ=1 AngleXU=0 Radius=3.675
    g7: Circle [constr] CenterX=19 CenterY=0 CenterZ=0 NormalX=0 NormalY=0 NormalZ=1 AngleXU=0 Radius=3.675
  constraints (22):
    c: Coincident(g0,g1)
    c: Coincident(g1,g2)
    c: Coincident(g2,g3)
    c: Coincident(g3,g4)
    c: Coincident(g4,g5)
    c: Coincident(g5,g0)
    c: Symmetric(g2,g0,g-1)
    c: Horizontal(g0)
    c: Horizontal(g3)
    c: Angle(g2,g1) = 2.0944
    c: Equal(g2,g1)
    c: Equal(g1,g5)
    c: Equal(g5,g4)
    c: DistanceY(g2,g0) = 7.35
    c: PointOnObject(g6,g-1)
    c: Tangent(g6,g0)
    c: Tangent(g6,g1)
    c: PointOnObject(g4,g-1)
    c: Tangent(g7,g5)
    c: Equal(g7,g6)
    c: Symmetric(g7,g6,g-2)
    c: DistanceX(g6,g7) = 38
FEATURE [PartDesign::Pocket] Pocket025  label="BL Nutslot001"
  BaseFeature = -> Mirrored005
  Direction = (0,0,-1)
  Length = 3.5
  Length2 = 100
  Placement = pos=(0,0,0) rot=(1,0,0;1.5708rad)
  Profile = -> Sketch089
  Suppressed = false
  Type = 0
FEATURE [Sketcher::SketchObject] Sketch090  label="bl esp pcb pocket001"
  ArcFitTolerance = 0
  AttachmentSupport = -> [YZ_Plane020]
  FullyConstrained = true
  MakeInternals = false
  MapMode = 5
  Placement = pos=(0,0,0) rot=(0.57735,0.57735,0.57735;2.0944rad)
  sketch-geometry (4):
    g0: LineSegment StartX=-4.3 StartY=-26.2 StartZ=0 EndX=-2.7 EndY=-26.2 EndZ=0
    g1: LineSegment StartX=-2.7 StartY=-26.2 StartZ=0 EndX=-2.7 EndY=-57.8 EndZ=0
    g2: LineSegment StartX=-2.7 StartY=-57.8 StartZ=0 EndX=-4.3 EndY=-57.8 EndZ=0
    g3: LineSegment StartX=-4.3 StartY=-57.8 StartZ=0 EndX=-4.3 EndY=-26.2 EndZ=0
  constraints (12):
    c: Coincident(g0,g1)
    c: Coincident(g1,g2)
    c: Coincident(g2,g3)
    c: Coincident(g3,g0)
    c: Horizontal(g0)
    c: Horizontal(g2)
    c: Vertical(g1)
    c: Vertical(g3)
    c: DistanceX(g0,g-1) = 2.7
    c: DistanceX(g0,g0) = 1.6
    c: DistanceY(g0,g-1) = 26.2
    c: DistanceY(g3,g3) = 31.6
FEATURE [Sketcher::SketchObject] Sketch091  label="bl bolthole001"
  ArcFitTolerance = 0
  AttachmentSupport = -> [XZ_Plane019]
  FullyConstrained = true
  MakeInternals = false
  MapMode = 5
  Placement = pos=(0,0,0) rot=(1,0,0;1.5708rad)
  sketch-geometry (5):
    g0: LineSegment StartX=19 StartY=3 StartZ=0 EndX=21.3 EndY=3 EndZ=0
    g1: LineSegment StartX=21.3 StartY=3 StartZ=0 EndX=21.3 EndY=-14 EndZ=0
    g2: LineSegment StartX=21.3 StartY=-14 StartZ=0 EndX=19 EndY=-14 EndZ=0
    g3: LineSegment StartX=19 StartY=-14 StartZ=0 EndX=19 EndY=3 EndZ=0
    g4: LineSegment [constr] StartX=19 StartY=-14 StartZ=0 EndX=19 EndY=-16.3 EndZ=0
  constraints (15):
    c: Coincident(g0,g1)
    c: Coincident(g1,g2)
    c: Coincident(g2,g3)
    c: Coincident(g3,g0)
    c: Horizontal(g0)
    c: Horizontal(g2)
    c: Vertical(g1)
    c: Vertical(g3)
    c: DistanceX(g0) = 19
    c: DistanceY(g0) = 3
    c: DistanceX(g0,g0) = 2.3
    c: DistanceY(g1,g1) = 17
    c: Coincident(g4,g2)
    c: Vertical(g4)
    c: Equal(g2,g4)
FEATURE [PartDesign::Groove] Groove005  label="BL Bolt hole R001"
  Angle = 360
  Angle2 = 60
  Axis = (0,-5e-16,-2.3)
  Base = (19,-3.1e-15,-14)
  BaseFeature = -> Pocket025
  Placement = pos=(0,0,0) rot=(1,0,0;1.5708rad)
  Profile = -> Sketch091
  ReferenceAxis = -> Sketch091 [Axis]
  Reversed = true
  Suppressed = false
  Type = 0
FEATURE [PartDesign::Mirrored] Mirrored006  label="BL Bolt hole L001"
  BaseFeature = -> Groove005
  MirrorPlane = -> YZ_Plane020
  Originals = -> [Groove005]
  Placement = pos=(0,0,0) rot=(1,0,0;1.5708rad)
  Suppressed = false
  TransformMode = 0
FEATURE [PartDesign::Pocket] Pocket028  label="BL Stepper pocket001"
  BaseFeature = -> Mirrored006
  Direction = (0,0,-1)
  Length = 38.2
  Length2 = 100
  Placement = pos=(0,0,0) rot=(1,0,0;1.5708rad)
  Profile = -> Sketch088
  Suppressed = false
  Type = 0
FEATURE [PartDesign::Pocket] Pocket021  label="BL ESP PCB pocket001"
  BaseFeature = -> Pocket028
  Direction = (-1,0,0)
  Length = 13.7
  Length2 = 25.7
  Placement = pos=(0,0,0) rot=(1,0,0;1.5708rad)
  Profile = -> Sketch090
  Suppressed = false
  Type = 4
FEATURE [Sketcher::SketchObject] Sketch073  label="bl esp component pocket001"
  ArcFitTolerance = 0
  AttachmentSupport = -> [XZ_Plane019]
  ExternalGeometry = -> [Sketch090,Pocket021]
  FullyConstrained = true
  MakeInternals = false
  MapMode = 5
  Placement = pos=(0,0,0) rot=(1,0,0;1.5708rad)
  sketch-geometry (6):
    g0: LineSegment StartX=-9.5 StartY=-26.2 StartZ=0 EndX=25.7 EndY=-26.2 EndZ=0
    g1: LineSegment StartX=25.7 StartY=-26.2 StartZ=0 EndX=25.7 EndY=-52.8 EndZ=0
    g2: LineSegment StartX=24.2 StartY=-57.8 StartZ=0 EndX=-9.5 EndY=-57.8 EndZ=0
    g3: LineSegment StartX=-9.5 StartY=-57.8 StartZ=0 EndX=-9.5 EndY=-26.2 EndZ=0
    g4: LineSegment StartX=25.7 StartY=-52.8 StartZ=0 EndX=24.2 EndY=-52.8 EndZ=0
    g5: LineSegment StartX=24.2 StartY=-52.8 StartZ=0 EndX=24.2 EndY=-57.8 EndZ=0
  constraints (18):
    c: Coincident(g0,g1)
    c: Coincident(g2,g3)
    c: Coincident(g3,g0)
    c: Horizontal(g0)
    c: Horizontal(g2)
    c: Vertical(g1)
    c: Vertical(g3)
    c: PointOnObject(g-3,g0)
    c: PointOnObject(g-3,g2)
    c: DistanceX(g2,g-3) = 9.5
    c: DistanceX(g0) = 25.7
    c: Coincident(g4,g5)
    c: Horizontal(g4)
    c: Vertical(g5)
    c: Coincident(g1,g4)
    c: Coincident(g5,g2)
    c: DistanceY(g5,g5) = 5
    c: DistanceX(g4,g4) = 1.5
FEATURE [PartDesign::Pocket] Pocket024  label="BL ESP Component pocket001"
  BaseFeature = -> Pocket021
  Direction = (0,1,-2e-16)
  Length = 4
  Length2 = 5.3
  Placement = pos=(0,0,0) rot=(1,0,0;1.5708rad)
  Profile = -> Sketch073
  Suppressed = false
  Type = 4
FEATURE [PartDesign::Pocket] Pocket030  label="BL ESP USB pocket001"
  BaseFeature = -> Pocket024
  Direction = (-1,0,0)
  Length = 5
  Length2 = 100
  Placement = pos=(0,0,0) rot=(1,0,0;1.5708rad)
  Profile = -> Sketch072
  Reversed = true
  Suppressed = false
  Type = 1
FEATURE [PartDesign::SubtractivePipe] SubtractivePipe004  label="BL ESP USB recess001"
  AuxilleryCurvelinear = true
  AuxillerySpineTangent = false
  BaseFeature = -> Pocket030
  Binormal = (0,0,0)
  Mode = 0
  Placement = pos=(0,0,0) rot=(1,0,0;1.5708rad)
  Profile = -> Sketch071
  Spine = -> Sketch070
  SpineTangent = false
  Suppressed = false
  Transformation = 0
  Transition = 0
FEATURE [PartDesign::Pocket] Pocket022  label="BL ESP antenna cutout001"
  BaseFeature = -> SubtractivePipe004
  Direction = (0,1,-2e-16)
  Length = 2
  Length2 = 100
  Placement = pos=(0,0,0) rot=(1,0,0;1.5708rad)
  Profile = -> Sketch074
  Reversed = true
  Suppressed = false
  Type = 0
FEATURE [PartDesign::Pocket] Pocket031  label="BL Relay cutout001"
  BaseFeature = -> Pocket022
  Direction = (-1,0,0)
  Length = 18
  Length2 = 100
  Midplane = true
  Placement = pos=(0,0,0) rot=(1,0,0;1.5708rad)
  Profile = -> Sketch075
  Suppressed = false
  Type = 0
FEATURE [PartDesign::SubtractivePipe] SubtractivePipe005  label="BL Narrow cable channel001"
  AuxilleryCurvelinear = true
  AuxillerySpineTangent = false
  BaseFeature = -> Pocket031
  Binormal = (0,0,0)
  Mode = 0
  Placement = pos=(0,0,0) rot=(1,0,0;1.5708rad)
  Profile = -> Sketch078
  Spine = -> Sketch076
  SpineTangent = false
  Suppressed = false
  Transformation = 0
  Transition = 0
FEATURE [PartDesign::SubtractivePipe] SubtractivePipe006  label="BL Wide cable channel001"
  AuxilleryCurvelinear = true
  AuxillerySpineTangent = false
  BaseFeature = -> SubtractivePipe005
  Binormal = (0,0,0)
  Mode = 0
  Placement = pos=(0,0,0) rot=(1,0,0;1.5708rad)
  Profile = -> Sketch081
  Spine = -> Sketch077
  SpineTangent = false
  Suppressed = false
  Transformation = 0
  Transition = 0
FEATURE [PartDesign::Pocket] Pocket023  label="BL Large cable channel001"
  BaseFeature = -> SubtractivePipe006
  Direction = (0,1,-2e-16)
  Length = 40
  Length2 = 100
  Midplane = true
  Placement = pos=(0,0,0) rot=(1,0,0;1.5708rad)
  Profile = -> Sketch080
  Suppressed = false
  Type = 0
FEATURE [PartDesign::Groove] Groove006  label="BL Screwhole 004"
  Angle = 360
  Angle2 = 60
  Axis = (3,0,0)
  Base = (35,-8,-70)
  BaseFeature = -> Pocket023
  Placement = pos=(0,0,0) rot=(1,0,0;1.5708rad)
  Profile = -> Sketch069
  ReferenceAxis = -> Sketch069 [Axis]
  Reversed = true
  Suppressed = false
  Type = 0
FEATURE [PartDesign::Groove] Groove008  label="BL Screwhole 006"
  Angle = 360
  Angle2 = 60
  Axis = (-3,0,0)
  Base = (35,25,-50)
  BaseFeature = -> Groove006
  Placement = pos=(0,0,0) rot=(1,0,0;1.5708rad)
  Profile = -> Sketch079
  ReferenceAxis = -> Sketch079 [Axis]
  Suppressed = false
  Type = 0
FEATURE [Sketcher::SketchObject] Sketch092  label="br rim trj"
  ArcFitTolerance = 0
  AttachmentSupport = -> [YZ_Plane020]
  FullyConstrained = true
  MakeInternals = false
  MapMode = 5
  Placement = pos=(0,0,0) rot=(0.57735,0.57735,0.57735;2.0944rad)
  sketch-geometry (2):
    g0: ArcOfCircle CenterX=0 CenterY=-47 CenterZ=0 NormalX=0 NormalY=0 NormalZ=1 AngleXU=0 Radius=28.5 StartAngle=4.84612 EndAngle=6.28319
    g1: LineSegment StartX=28.5 StartY=0 StartZ=0 EndX=28.5 EndY=-47 EndZ=0
  constraints (7):
    c: Vertical(g1)
    c: DistanceY(g0,g-1) = 47
    c: PointOnObject(g1,g-1)
    c: DistanceX(g1) = 28.5
    c: PointOnObject(g0,g-2)
    c: DistanceX(g0) = 3.8
    c: Tangent(g0,g1) = 1.5708
FEATURE [Sketcher::SketchObject] Sketch093  label="bl screwhole 006"
  ArcFitTolerance = 0
  AttachmentOffset = pos=(0,0,25) rot=(0,0,1;0rad)
  AttachmentSupport = -> [XZ_Plane019]
  FullyConstrained = true
  MakeInternals = false
  MapMode = 5
  Placement = pos=(0,-25,5.6e-15) rot=(1,0,0;1.5708rad)
  sketch-geometry (7):
    g0: LineSegment StartX=35 StartY=-37 StartZ=0 EndX=4.3 EndY=-37 EndZ=0
    g1: LineSegment StartX=4.3 StartY=-37 StartZ=0 EndX=3 EndY=-38.3 EndZ=0
    g2: LineSegment StartX=3 StartY=-38.3 StartZ=0 EndX=0 EndY=-38.3 EndZ=0
    g3: LineSegment StartX=0 StartY=-38.3 StartZ=0 EndX=-12 EndY=-40 EndZ=0
    g4: LineSegment StartX=-12 StartY=-40 StartZ=0 EndX=35 EndY=-40 EndZ=0
    g5: LineSegment StartX=35 StartY=-40 StartZ=0 EndX=35 EndY=-37 EndZ=0
    g6: LineSegment [constr] StartX=35 StartY=-40 StartZ=0 EndX=32 EndY=-40 EndZ=0
  constraints (21):
    c: Horizontal(g0)
    c: Coincident(g0,g1)
    c: Coincident(g1,g2)
    c: Horizontal(g2)
    c: Coincident(g2,g3)
    c: Coincident(g3,g4)
    c: Horizontal(g4)
    c: Coincident(g4,g5)
    c: Coincident(g5,g0)
    c: Vertical(g5)
    c: Coincident(g6,g4)
    c: Horizontal(g6)
    c: Equal(g5,g6)
    c: DistanceY(g6,g-1) = 40
    c: DistanceY(g4,g1) = 1.7
    c: Angle(g1,g2) = 2.35619
    c: DistanceX(g1) = 3
    c: DistanceY(g5,g5) = 3
    c: PointOnObject(g2,g-2)
    c: DistanceX(g3,g3) = 12
    c: DistanceX(g0) = 35
FEATURE [PartDesign::Groove] Groove007  label="BL Screwhole 005"
  Angle = 360
  Angle2 = 60
  Axis = (-3,0,0)
  Base = (35,-25,-40)
  BaseFeature = -> Groove008
  Placement = pos=(0,0,0) rot=(1,0,0;1.5708rad)
  Profile = -> Sketch093
  ReferenceAxis = -> Sketch093 [Axis]
  Suppressed = false
  Type = 0
FEATURE [Sketcher::SketchObject] Sketch094  label="br cutout right half"
  ArcFitTolerance = 0
  AttachmentSupport = -> [XZ_Plane019]
  FullyConstrained = true
  MakeInternals = false
  MapMode = 5
  Placement = pos=(0,0,0) rot=(1,0,0;1.5708rad)
  sketch-geometry (4):
    g0: LineSegment StartX=-35 StartY=5 StartZ=0 EndX=0.5 EndY=5 EndZ=0
    g1: LineSegment StartX=0.5 StartY=5 StartZ=0 EndX=0.5 EndY=-80 EndZ=0
    g2: LineSegment StartX=0.5 StartY=-80 StartZ=0 EndX=-35 EndY=-80 EndZ=0
    g3: LineSegment StartX=-35 StartY=-80 StartZ=0 EndX=-35 EndY=5 EndZ=0
  constraints (12):
    c: Coincident(g0,g1)
    c: Coincident(g1,g2)
    c: Coincident(g2,g3)
    c: Coincident(g3,g0)
    c: Horizontal(g0)
    c: Horizontal(g2)
    c: Vertical(g1)
    c: Vertical(g3)
    c: DistanceX(g1,g-1) = -0.5
    c: DistanceY(g2,g-1) = 80
    c: DistanceY(g0) = 5
    c: DistanceX(g0) = -35
FEATURE [PartDesign::Pocket] Pocket032  label="BR Cutout Right"
  BaseFeature = -> Groove007
  Direction = (0,1,-2e-16)
  Length = 5
  Length2 = 100
  Midplane = true
  Placement = pos=(0,0,0) rot=(1,0,0;1.5708rad)
  Profile = -> Sketch094
  Suppressed = false
  Type = 1
FEATURE [Sketcher::SketchObject] Sketch095  label="br rim crs"
  ArcFitTolerance = 0
  AttachmentSupport = -> [XY_Plane019]
  FullyConstrained = true
  MakeInternals = false
  MapMode = 5
  sketch-geometry (5):
    g0: LineSegment StartX=0.5 StartY=30.2411 StartZ=0 EndX=-1.5 EndY=29.2 EndZ=0
    g1: LineSegment StartX=-1.5 StartY=29.2 StartZ=0 EndX=-1.5 EndY=27.8 EndZ=0
    g2: LineSegment StartX=-1.5 StartY=27.8 StartZ=0 EndX=0.5 EndY=26.7589 EndZ=0
    g3: LineSegment StartX=0.5 StartY=26.7589 StartZ=0 EndX=0.5 EndY=30.2411 EndZ=0
    g4: LineSegment [constr] StartX=-1.5 StartY=28.5 StartZ=0 EndX=0.5 EndY=28.5 EndZ=0
  constraints (14):
    c: Coincident(g0,g1)
    c: Vertical(g1)
    c: Coincident(g1,g2)
    c: Coincident(g2,g3)
    c: Coincident(g3,g0)
    c: PointOnObject(g4,g1)
    c: PointOnObject(g4,g3)
    c: DistanceY(g4) = 28.5
    c: Symmetric(g2,g0,g4)
    c: Symmetric(g1,g0,g4)
    c: DistanceY(g1,g1) = 1.4
    c: Angle(g2,g0) = 0.959931
    c: DistanceX(g0,g0) = 2
    c: DistanceX(g0) = 0.5
FEATURE [PartDesign::AdditivePipe] AdditivePipe002  label="BR Rim R"
  AuxilleryCurvelinear = true
  AuxillerySpineTangent = false
  BaseFeature = -> Pocket032
  Binormal = (0,0,0)
  Mode = 0
  Placement = pos=(0,0,0) rot=(1,0,0;1.5708rad)
  Profile = -> Sketch095
  Spine = -> Sketch092
  SpineTangent = false
  Suppressed = false
  Transformation = 0
  Transition = 0
FEATURE [PartDesign::Mirrored] Mirrored007
  BaseFeature = -> AdditivePipe002
  MirrorPlane = -> XZ_Plane019
  Originals = -> [AdditivePipe002]
  Placement = pos=(0,0,0) rot=(1,0,0;1.5708rad)
  Suppressed = false
  TransformMode = 0
FEATURE [PartDesign::Fillet] Fillet002
  Base = -> Mirrored007 [Edge234,Edge279,Edge291]
  BaseFeature = -> Mirrored007
  Placement = pos=(0,0,0) rot=(1,0,0;1.5708rad)
  Radius = 1
  SupportTransform = false
  Suppressed = false
  UseAllEdges = false
FEATURE [PartDesign::Fillet] Fillet003
  Base = -> Fillet002 [Edge16]
  BaseFeature = -> Fillet002
  Placement = pos=(0,0,0) rot=(1,0,0;1.5708rad)
  Radius = 5
  SupportTransform = false
  Suppressed = false
  UseAllEdges = false
FEATURE [PartDesign::Body] Body019  label="Body Right"
  AllowCompound = false
  Group = -> [Sketch082,Pad015,Sketch084,Sketch083,Sketch086,SubtractiveLoft001,Pocket027,Sketch087,Pocket026,Sketch085,Pocket029,Mirrored005,Sketch089,Pocket025,Sketch091,Groove005,Mirrored006,Sketch088,Pocket028,Sketch090,Pocket021,Sketch073,Pocket024,Sketch072,Pocket030,Sketch070,Sketch071,SubtractivePipe004,Sketch074,Pocket022,Sketch075,Pocket031,Sketch078,Sketch076,SubtractivePipe005,Sketch077,Sketch081,+17 more]
  Origin = -> Origin019
  Tip = -> Fillet003
FEATURE [Sketcher::SketchObject] Sketch096  label="pcb"
  ArcFitTolerance = 0
  AttachmentSupport = -> [XY_Plane020]
  FullyConstrained = true
  MakeInternals = false
  MapMode = 5
  sketch-geometry (12):
    g0: LineSegment StartX=-17.35 StartY=16.15 StartZ=0 EndX=17.35 EndY=16.15 EndZ=0
    g1: LineSegment StartX=17.35 StartY=16.15 StartZ=0 EndX=17.35 EndY=-16.15 EndZ=0
    g2: LineSegment StartX=17.35 StartY=-16.15 StartZ=0 EndX=-17.35 EndY=-16.15 EndZ=0
    g3: LineSegment StartX=-17.35 StartY=-16.15 StartZ=0 EndX=-17.35 EndY=16.15 EndZ=0
    g4: LineSegment [constr] StartX=-14.9 StartY=13.2 StartZ=0 EndX=14.9 EndY=13.2 EndZ=0
    g5: LineSegment [constr] StartX=14.9 StartY=13.2 StartZ=0 EndX=14.9 EndY=-13.2 EndZ=0
    g6: LineSegment [constr] StartX=14.9 StartY=-13.2 StartZ=0 EndX=-14.9 EndY=-13.2 EndZ=0
    g7: LineSegment [constr] StartX=-14.9 StartY=-13.2 StartZ=0 EndX=-14.9 EndY=13.2 EndZ=0
    g8: Circle CenterX=14.9 CenterY=13.2 CenterZ=0 NormalX=0 NormalY=0 NormalZ=1 AngleXU=0 Radius=1.5
    g9: Circle CenterX=-14.9 CenterY=13.2 CenterZ=0 NormalX=0 NormalY=0 NormalZ=1 AngleXU=0 Radius=1.5
    g10: Circle CenterX=-14.9 CenterY=-13.2 CenterZ=0 NormalX=0 NormalY=0 NormalZ=1 AngleXU=0 Radius=1.5
    g11: Circle CenterX=14.9 CenterY=-13.2 CenterZ=0 NormalX=0 NormalY=0 NormalZ=1 AngleXU=0 Radius=1.5
  constraints (28):
    c: Coincident(g0,g1)
    c: Coincident(g1,g2)
    c: Coincident(g2,g3)
    c: Coincident(g3,g0)
    c: Horizontal(g2)
    c: Vertical(g3)
    c: DistanceX(g0,g0) = 34.7
    c: Symmetric(g0,g0,g-2)
    c: Symmetric(g1,g0,g-1)
    c: DistanceY(g1,g1) = 32.3
    c: Coincident(g4,g5)
    c: Coincident(g5,g6)
    c: Coincident(g6,g7)
    c: Coincident(g7,g4)
    c: Horizontal(g6)
    c: Vertical(g7)
    c: Symmetric(g4,g4,g-2)
    c: Symmetric(g5,g4,g-1)
    c: DistanceX(g4,g4) = 29.8
    c: DistanceY(g5,g5) = 26.4
    c: Coincident(g8,g4)
    c: Radius(g8) = 1.5
    c: Coincident(g9,g4)
    c: Coincident(g10,g6)
    c: Coincident(g11,g5)
    c: Equal(g11,g10)
    c: Equal(g10,g9)
    c: Equal(g9,g8)
FEATURE [PartDesign::Pad] Pad016  label="PCB001"
  AllowMultiFace = false
  Direction = (0,0,1)
  Length = 1.8
  Length2 = 100
  Profile = -> Sketch096
  Suppressed = false
  Type = 0
FEATURE [PartDesign::Plane] DatumPlane  label="top of pcb"
  AttachmentOffset = pos=(0,0,1.8) rot=(0,0,1;0rad)
  AttachmentSupport = -> [XY_Plane020]
  Length = 60
  MapMode = 5
  Placement = pos=(0,0,1.8) rot=(0,0,1;0rad)
  ResizeMode = 0
  Width = 60
FEATURE [Sketcher::SketchObject] Sketch097
  ArcFitTolerance = 0
  AttachmentSupport = -> [DatumPlane]
  FullyConstrained = true
  MakeInternals = false
  MapMode = 5
  Placement = pos=(0,0,1.8) rot=(0,0,1;0rad)
  sketch-geometry (4):
    g0: LineSegment StartX=4 StartY=14.5 StartZ=0 EndX=8 EndY=14.5 EndZ=0
    g1: LineSegment StartX=8 StartY=14.5 StartZ=0 EndX=8 EndY=3 EndZ=0
    g2: LineSegment StartX=8 StartY=3 StartZ=0 EndX=4 EndY=3 EndZ=0
    g3: LineSegment StartX=4 StartY=3 StartZ=0 EndX=4 EndY=14.5 EndZ=0
  constraints (12):
    c: Coincident(g0,g1)
    c: Coincident(g1,g2)
    c: Coincident(g2,g3)
    c: Coincident(g3,g0)
    c: Horizontal(g0)
    c: Horizontal(g2)
    c: Vertical(g1)
    c: Vertical(g3)
    c: DistanceX(g2) = 4
    c: DistanceY(g2) = 3
    c: DistanceY(g1,g1) = 11.5
    c: DistanceX(g0,g0) = 4
FEATURE [PartDesign::Pad] Pad017
  AllowMultiFace = false
  BaseFeature = -> Pad016
  Direction = (0,0,1)
  Length = 11.8
  Length2 = 100
  Profile = -> Sketch097
  Suppressed = false
  Type = 0
FEATURE [Sketcher::SketchObject] Sketch098
  ArcFitTolerance = 0
  AttachmentOffset = pos=(0,0,-1) rot=(0,0,1;0rad)
  AttachmentSupport = -> [Pad017]
  ExternalGeometry = -> [DatumPlane,Sketch097]
  FullyConstrained = true
  MakeInternals = false
  MapMode = 5
  Placement = pos=(0,4,-2e-16) rot=(1,0,0;1.5708rad)
  sketch-geometry (8):
    g0: ArcOfCircle CenterX=2.1 CenterY=13.6 CenterZ=0 NormalX=0 NormalY=0 NormalZ=1 AngleXU=0 Radius=3.4 StartAngle=0 EndAngle=2.0944
    g1: ArcOfCircle CenterX=2.1 CenterY=13.6 CenterZ=0 NormalX=0 NormalY=0 NormalZ=1 AngleXU=0 Radius=4.4 StartAngle=0 EndAngle=2.0944
    g2: LineSegment StartX=-0.1 StartY=17.4105 StartZ=0 EndX=0.4 EndY=16.5445 EndZ=0
    g3: LineSegment [constr] StartX=2.1 StartY=18 StartZ=0 EndX=2.1 EndY=13.6 EndZ=0
    g4: LineSegment [constr] StartX=6 StartY=1.8 StartZ=0 EndX=6 EndY=13.6 EndZ=0
    g5: LineSegment StartX=6.5 StartY=13.6 StartZ=0 EndX=6.5 EndY=1.8 EndZ=0
    g6: LineSegment StartX=6.5 StartY=1.8 StartZ=0 EndX=5.5 EndY=1.8 EndZ=0
    g7: LineSegment StartX=5.5 StartY=1.8 StartZ=0 EndX=5.5 EndY=13.6 EndZ=0
  constraints (22):
    c: Coincident(g1,g0)
    c: Coincident(g2,g1)
    c: Coincident(g2,g0)
    c: PointOnObject(g0,g2)
    c: PointOnObject(g3,g1)
    c: Coincident(g3,g0)
    c: DistanceY(g3) = 18
    c: Distance(g2) = 1
    c: Symmetric(g1,g0,g4)
    c: Vertical(g3)
    c: Angle(g3,g2) = 0.523599
    c: Coincident(g5,g6)
    c: Coincident(g6,g7)
    c: Horizontal(g6)
    c: Vertical(g5)
    c: PointOnObject(g5,g-3)
    c: Symmetric(g-4,g-4,g4)
    c: PointOnObject(g4,g-3)
    c: DistanceY(g1) = 13.6
    c: Tangent(g0,g7) = -1.5708
    c: Tangent(g1,g5) = 1.5708
    c: Equal(g5,g4)
FEATURE [PartDesign::Pad] Pad018
  AllowMultiFace = false
  BaseFeature = -> Pad017
  Direction = (0,-1,2e-16)
  Length = 9.5
  Length2 = 100
  Profile = -> Sketch098
  Reversed = true
  Suppressed = false
  Type = 0
FEATURE [PartDesign::Fillet] Fillet004
  Base = -> Pad018 [Edge41,Edge46,Edge42,Edge45]
  BaseFeature = -> Pad018
  Radius = 0.4
  SupportTransform = false
  Suppressed = false
  UseAllEdges = false
FEATURE [Sketcher::SketchObject] Sketch099
  ArcFitTolerance = 0
  AttachmentOffset = pos=(0,0,3) rot=(0,0,1;0rad)
  AttachmentSupport = -> [XZ_Plane020]
  ExternalGeometry = -> [DatumPlane]
  FullyConstrained = true
  MakeInternals = false
  MapMode = 5
  Placement = pos=(0,-3,7e-16) rot=(1,0,0;1.5708rad)
  sketch-geometry (5):
    g0: ArcOfCircle CenterX=12.35 CenterY=5.8 CenterZ=0 NormalX=0 NormalY=0 NormalZ=1 AngleXU=0 Radius=1.5 StartAngle=3e-16 EndAngle=1.5708
    g1: LineSegment StartX=13.85 StartY=5.8 StartZ=0 EndX=13.85 EndY=1.8 EndZ=0
    g2: LineSegment StartX=13.85 StartY=1.8 StartZ=0 EndX=12.35 EndY=1.8 EndZ=0
    g3: LineSegment StartX=12.35 StartY=1.8 StartZ=0 EndX=12.35 EndY=7.3 EndZ=0
    g4: LineSegment [constr] StartX=12.35 StartY=7.3 StartZ=0 EndX=12.35 EndY=8.8 EndZ=0
  constraints (15):
    c: Vertical(g1)
    c: Coincident(g1,g2)
    c: Horizontal(g2)
    c: Coincident(g2,g3)
    c: Vertical(g3)
    c: Coincident(g0,g3)
    c: PointOnObject(g0,g3)
    c: Tangent(g0,g1) = 1.5708
    c: DistanceY(g1,g0) = 5.5
    c: Radius(g0) = 1.5
    c: Coincident(g4,g0)
    c: Vertical(g4)
    c: Equal(g2,g4)
    c: DistanceX(g2) = 12.35
    c: PointOnObject(g2,g-3)
FEATURE [PartDesign::Revolution] Revolution013
  AllowMultiFace = false
  Angle = 360
  Angle2 = 60
  Axis = (0,3e-16,1.5)
  Base = (12.35,-3,7.3)
  BaseFeature = -> Fillet004
  Profile = -> Sketch099
  ReferenceAxis = -> Sketch099 [Axis]
  Reversed = true
  Suppressed = false
  Type = 0
FEATURE [PartDesign::LinearPattern] LinearPattern002
  BaseFeature = -> Revolution013
  Direction = -> Y_Axis020
  Length = 14
  Mode = 0
  Occurrences = 4
  Offset = 4.66667
  Originals = -> [Revolution013]
  Suppressed = false
  TransformMode = 0
FEATURE [Sketcher::SketchObject] Sketch100
  ArcFitTolerance = 0
  AttachmentSupport = -> [DatumPlane]
  FullyConstrained = true
  MakeInternals = false
  MapMode = 5
  Placement = pos=(0,0,1.8) rot=(0,0,1;0rad)
  sketch-geometry (4):
    g0: LineSegment StartX=1.95 StartY=15.15 StartZ=0 EndX=-8.05 EndY=15.15 EndZ=0
    g1: LineSegment StartX=-8.05 StartY=15.15 StartZ=0 EndX=-8.05 EndY=-5.35 EndZ=0
    g2: LineSegment StartX=-8.05 StartY=-5.35 StartZ=0 EndX=1.95 EndY=-5.35 EndZ=0
    g3: LineSegment StartX=1.95 StartY=-5.35 StartZ=0 EndX=1.95 EndY=15.15 EndZ=0
  constraints (12):
    c: Coincident(g0,g1)
    c: Coincident(g1,g2)
    c: Coincident(g2,g3)
    c: Coincident(g3,g0)
    c: Horizontal(g0)
    c: Horizontal(g2)
    c: Vertical(g1)
    c: Vertical(g3)
    c: DistanceY(g1,g1) = 20.5
    c: DistanceX(g0,g0) = 10
    c: DistanceX(g2) = 1.95
    c: DistanceY(g2) = -5.35
FEATURE [PartDesign::Pad] Pad019
  AllowMultiFace = false
  BaseFeature = -> LinearPattern002
  Direction = (0,0,1)
  Length = 8.3
  Length2 = 100
  Profile = -> Sketch100
  Suppressed = false
  Type = 0
FEATURE [Sketcher::SketchObject] Sketch101
  ArcFitTolerance = 0
  AttachmentSupport = -> [DatumPlane]
  FullyConstrained = true
  MakeInternals = false
  MapMode = 5
  Placement = pos=(0,0,1.8) rot=(0,0,1;0rad)
  sketch-geometry (4):
    g0: LineSegment StartX=-11.35 StartY=11.35 StartZ=0 EndX=-8.81 EndY=11.35 EndZ=0
    g1: LineSegment StartX=-8.81 StartY=11.35 StartZ=0 EndX=-8.81 EndY=8.81 EndZ=0
    g2: LineSegment StartX=-8.81 StartY=8.81 StartZ=0 EndX=-11.35 EndY=8.81 EndZ=0
    g3: LineSegment StartX=-11.35 StartY=8.81 StartZ=0 EndX=-11.35 EndY=11.35 EndZ=0
  constraints (12):
    c: Coincident(g0,g1)
    c: Coincident(g1,g2)
    c: Coincident(g2,g3)
    c: Coincident(g3,g0)
    c: Horizontal(g0)
    c: Horizontal(g2)
    c: Vertical(g1)
    c: Vertical(g3)
    c: Equal(g3,g0)
    c: DistanceX(g0,g0) = 2.54
    c: DistanceX(g1) = -8.81
    c: DistanceY(g1) = 8.81
FEATURE [PartDesign::Pad] Pad020
  AllowMultiFace = false
  BaseFeature = -> Pad019
  Direction = (0,0,1)
  Length = 16.5
  Length2 = 100
  Profile = -> Sketch101
  Suppressed = false
  Type = 0
FEATURE [Sketcher::SketchObject] Sketch102
  ArcFitTolerance = 0
  AttachmentSupport = -> [DatumPlane]
  ExternalGeometry = -> [Sketch101]
  FullyConstrained = true
  MakeInternals = false
  MapMode = 5
  Placement = pos=(0,0,1.8) rot=(0,0,1;0rad)
  sketch-geometry (2):
    g0: Circle [constr] CenterX=-10.08 CenterY=10.08 CenterZ=0 NormalX=0 NormalY=0 NormalZ=1 AngleXU=0 Radius=1.27
    g1: Circle CenterX=-10.08 CenterY=10.08 CenterZ=0 NormalX=0 NormalY=0 NormalZ=1 AngleXU=0 Radius=0.5
  constraints (5):
    c: Coincident(g1,g0)
    c: Radius(g1) = 0.5
    c: Tangent(g-5,g0)
    c: Tangent(g-3,g0)
    c: Tangent(g0,g-4)
FEATURE [Sketcher::SketchObject] Sketch105
  ArcFitTolerance = 0
  AttachmentSupport = -> [XY_Plane020]
  ExternalGeometry = -> [Sketch101]
  FullyConstrained = true
  MakeInternals = false
  MapMode = 5
  sketch-geometry (1):
    g0: LineSegment StartX=-10.08 StartY=10.08 StartZ=0 EndX=-10.08 EndY=7.54 EndZ=0
  constraints (3):
    c: Symmetric(g-4,g-4,g0)
    c: Symmetric(g0,g0,g-4)
    c: Equal(g0,g-4)
FEATURE [PartDesign::Plane] DatumPlane001  label="wire plane"
  AttachmentSupport = -> [Sketch105,Y_Axis020]
  Length = 60
  MapMode = 7
  Placement = pos=(-10.08,10.08,0) rot=(1,0,0;1.5708rad)
  ResizeMode = 0
  Width = 60
FEATURE [Sketcher::SketchObject] Sketch103
  ArcFitTolerance = 0
  AttachmentSupport = -> [DatumPlane001]
  ExternalGeometry = -> [Sketch101,DatumPlane]
  FullyConstrained = true
  MakeInternals = false
  MapMode = 5
  Placement = pos=(-10.08,10.08,0) rot=(1,0,0;1.5708rad)
  sketch-geometry (3):
    g0: ArcOfCircle CenterX=-5 CenterY=18.2 CenterZ=0 NormalX=0 NormalY=0 NormalZ=1 AngleXU=0 Radius=5 StartAngle=0 EndAngle=2.35619
    g1: LineSegment [constr] StartX=-8.53553 StartY=21.7355 StartZ=0 EndX=-5 EndY=18.2 EndZ=0
    g2: LineSegment StartX=3.6e-15 StartY=18.2 StartZ=0 EndX=3.6e-15 EndY=1.8 EndZ=0
  constraints (8):
    c: Coincident(g1,g0)
    c: Coincident(g1,g0)
    c: Radius(g0) = 5
    c: DistanceY(g0) = 18.2
    c: Symmetric(g-3,g-3,g2)
    c: Tangent(g2,g0) = 1.5708
    c: Angle(g1,g-1) = 0.785398
    c: PointOnObject(g2,g-4)
FEATURE [PartDesign::AdditivePipe] AdditivePipe003
  AuxilleryCurvelinear = true
  AuxillerySpineTangent = false
  BaseFeature = -> Pad020
  Binormal = (0,0,0)
  Mode = 0
  Profile = -> Sketch102
  Refine = true
  Spine = -> Sketch103
  SpineTangent = false
  Suppressed = false
  Transformation = 0
  Transition = 0
FEATURE [PartDesign::LinearPattern] LinearPattern003
  BaseFeature = -> AdditivePipe003
  Direction = -> Y_Axis020
  Length = 7.62
  Mode = 0
  Occurrences = 4
  Offset = 2.54
  Originals = -> [Pad020,AdditivePipe003]
  Reversed = true
  Suppressed = false
  TransformMode = 0
FEATURE [Sketcher::SketchObject] Sketch104
  ArcFitTolerance = 0
  AttachmentSupport = -> [DatumPlane]
  ExternalGeometry = -> [LinearPattern003]
  FullyConstrained = true
  MakeInternals = false
  MapMode = 5
  Placement = pos=(0,0,1.8) rot=(0,0,1;0rad)
  sketch-geometry (4):
    g0: LineSegment StartX=-8.05 StartY=-10.31 StartZ=0 EndX=2.11 EndY=-10.31 EndZ=0
    g1: LineSegment StartX=2.11 StartY=-10.31 StartZ=0 EndX=2.11 EndY=-12.85 EndZ=0
    g2: LineSegment StartX=2.11 StartY=-12.85 StartZ=0 EndX=-8.05 EndY=-12.85 EndZ=0
    g3: LineSegment StartX=-8.05 StartY=-12.85 StartZ=0 EndX=-8.05 EndY=-10.31 EndZ=0
  constraints (12):
    c: Coincident(g0,g1)
    c: Coincident(g1,g2)
    c: Coincident(g2,g3)
    c: Coincident(g3,g0)
    c: Horizontal(g0)
    c: Horizontal(g2)
    c: Vertical(g1)
    c: Vertical(g3)
    c: DistanceY(g3,g3) = 2.54
    c: DistanceX(g0,g0) = 10.16
    c: DistanceX(g0) = 2.11
    c: DistanceY(g0) = -10.31
FEATURE [PartDesign::Pad] Pad021
  AllowMultiFace = false
  BaseFeature = -> LinearPattern003
  Direction = (0,0,1)
  Length = 8.6
  Length2 = 100
  Profile = -> Sketch104
  ReferenceAxis = -> Sketch104 [N_Axis]
  Suppressed = false
  Type = 0
FEATURE [PartDesign::Body] Body020  label="ULN2003"
  AllowCompound = false
  Group = -> [Sketch096,Pad016,Sketch097,DatumPlane,Pad017,Sketch098,Pad018,Fillet004,Sketch099,Revolution013,LinearPattern002,Sketch100,Pad019,Sketch101,Pad020,Sketch102,Sketch103,Sketch105,DatumPlane001,AdditivePipe003,LinearPattern003,Sketch104,Pad021]
  Origin = -> Origin020
  Placement = pos=(0,-1,-41) rot=(0,0,1;0rad)
  Tip = -> Pad021
FEATURE [Part::FeaturePython] Screw002  label="M4x20-Screw002"  # WARN: FeaturePython — macro-defined, semantics opaque (R4)
  Diameter = 2
  Invert = false
  LeftHanded = false
  Length = 6
  LengthCustom = 20
  MatchOuter = false
  Placement = pos=(19,0,9) rot=(0,0,1;0rad)
  Thread = false
  Type = 84
FEATURE [Part::FeaturePython] Nut002  label="M4-Nut002"  # WARN: FeaturePython — macro-defined, semantics opaque (R4)
  Diameter = 6
  Invert = false
  LeftHanded = false
  MatchOuter = false
  Placement = pos=(19,0,-5.8) rot=(0,1,0;3.14159rad)
  Thread = false
  Type = 31
FEATURE [Part::FeaturePython] Screw003  label="M4x20-Screw"  # WARN: FeaturePython — macro-defined, semantics opaque (R4)
  Diameter = 2
  Invert = false
  LeftHanded = false
  Length = 6
  LengthCustom = 20
  MatchOuter = false
  Placement = pos=(-19,0,9) rot=(0,0,1;0rad)
  Thread = false
  Type = 84
FEATURE [Part::FeaturePython] Nut003  label="M4-Nut"  # WARN: FeaturePython — macro-defined, semantics opaque (R4)
  Diameter = 6
  Invert = false
  LeftHanded = false
  MatchOuter = false
  Placement = pos=(-19,0,-5.8) rot=(0,1,0;3.14159rad)
  Thread = false
  Type = 31
FEATURE [PartDesign::SubShapeBinder] Binder  label="cp ref pcb"
  BindCopyOnChange = 0
  BindMode = 0
  ClaimChildren = false
  Context = -> Body [Binder.]
  Fuse = false
  MakeFace = true
  OffsetFill = false
  OffsetIntersection = false
  OffsetJoinType = 0
  OffsetOpenResult = false
  PartialLoad = false
  Refine = true
  Relative = true
  Support = -> [Part__Feature[Face46]]
  _Version = 2
FEATURE [PartDesign::SubShapeBinder] Binder001  label="cp ref housing ESP"
  BindCopyOnChange = 0
  BindMode = 0
  ClaimChildren = false
  Context = -> Body [Binder001.]
  Fuse = false
  MakeFace = true
  OffsetFill = false
  OffsetIntersection = false
  OffsetJoinType = 0
  OffsetOpenResult = false
  PartialLoad = false
  Refine = true
  Relative = true
  Support = -> [Part__Feature[Face987,Face424,Face706]]
  _Version = 2
FEATURE [PartDesign::SubShapeBinder] Binder002  label="cp ref pins"
  BindCopyOnChange = 0
  BindMode = 0
  ClaimChildren = false
  Context = -> Body [Binder002.]
  Fuse = false
  MakeFace = true
  OffsetFill = false
  OffsetIntersection = false
  OffsetJoinType = 0
  OffsetOpenResult = false
  PartialLoad = false
  Refine = true
  Relative = true
  Support = -> [Part__Feature[Edge654,Edge649]]
  _Version = 2
FEATURE [PartDesign::Point] DatumPoint  label="cp ref gnd"
  AttacherType = Attacher::AttachEnginePoint
  AttachmentSupport = -> [Binder002]
  MapMode = 36
  Placement = pos=(11.43,0.999,3.49) rot=(0,1,0;3.14159rad)
FEATURE [PartDesign::Point] DatumPoint001  label="cp ref VCC"
  AttacherType = Attacher::AttachEnginePoint
  AttachmentSupport = -> [Binder002]
  MapMode = 36
  Placement = pos=(11.43,0.999,6.03) rot=(0,1,0;3.14159rad)
FEATURE [PartDesign::Plane] DatumPlane002  label="cp pln capacitor"
  AttachmentOffset = pos=(0,0,-3) rot=(0,0,1;0rad)
  AttachmentSupport = -> [DatumPoint,XY_Plane]
  Length = 60
  MapMode = 6
  Placement = pos=(11.43,0.999,0.49) rot=(0,0,1;3.14159rad)
  ResizeMode = 0
  Width = 60
FEATURE [Sketcher::SketchObject] Sketch
  ArcFitTolerance = 1e-06
  AttachmentSupport = -> [DatumPlane002]
  ExternalGeometry = -> [Binder001]
  FullyConstrained = true
  MakeInternals = false
  MapMode = 5
  Placement = pos=(11.43,0.999,0.49) rot=(0,0,1;3.14159rad)
  sketch-geometry (1):
    g0: Circle CenterX=-0.541184 CenterY=-4.25 CenterZ=0 NormalX=0 NormalY=0 NormalZ=1 AngleXU=0 Radius=4.25
  constraints (3):
    c: Tangent(g0,g-1)
    c: Diameter(g0) = 8.5
    c: PointOnObject(g-4,g0)
FEATURE [PartDesign::Pad] Pad
  Direction = (0,0,1)
  Length = 17
  Length2 = 10
  Placement = pos=(11.43,0.999,0.49) rot=(0,0,1;3.14159rad)
  Profile = -> Sketch
  ReferenceAxis = -> Sketch [N_Axis]
  Refine = true
  Reversed = true
  Suppressed = false
  Type = 0
FEATURE [PartDesign::Body] Body  label="Capacitor 1 mF"
  AllowCompound = false
  Group = -> [Binder,Binder002,DatumPoint,DatumPoint001,Binder001,DatumPlane002,Sketch,Pad]
  Origin = -> Origin
  Tip = -> Pad
FEATURE [Part::Compound] Compound004  label="ESP with Capacitor"
  Links = -> [Part__Feature,Body]
  Placement = pos=(0,-10,-53) rot=(1,0,0;1.5708rad)
FEATURE [PartDesign::Plane] DatumPlane003  label="c cable pln crs"
  AttachmentSupport = -> [Sketch039]
  Length = 60
  MapMode = 7
  Placement = pos=(0,20,0) rot=(0,0,1;0rad)
  ResizeMode = 0
  Width = 60
FEATURE [Sketcher::SketchObject] Sketch038  label="c cable crs"
  ArcFitTolerance = 0
  AttachmentSupport = -> [DatumPlane003]
  FullyConstrained = true
  MakeInternals = false
  MapMode = 5
  Placement = pos=(0,20,0) rot=(0,0,1;0rad)
  sketch-geometry (1):
    g0: Circle CenterX=0 CenterY=0 CenterZ=0 NormalX=0 NormalY=0 NormalZ=1 AngleXU=0 Radius=3
  constraints (2):
    c: Coincident(g0,g-1)
    c: Radius(g0) = 3
FEATURE [PartDesign::AdditivePipe] AdditivePipe
  AuxilleryCurvelinear = true
  AuxillerySpineTangent = false
  Binormal = (0,0,0)
  Mode = 0
  Placement = pos=(0,20,0) rot=(0,0,1;0rad)
  Profile = -> Sketch038
  Refine = true
  Spine = -> Sketch039
  SpineTangent = false
  Suppressed = false
  Transformation = 0
  Transition = 0
FEATURE [PartDesign::Body] Body015  label="Cable"
  AllowCompound = false
  Group = -> [Sketch038,Sketch039,DatumPlane003,AdditivePipe]
  Origin = -> Origin015
  Tip = -> AdditivePipe
FEATURE [PartDesign::SubShapeBinder] Binder003  label="sk ref wallsocket"
  BindCopyOnChange = 0
  BindMode = 0
  ClaimChildren = false
  Context = -> Body021 [Binder003.]
  Fuse = false
  MakeFace = true
  OffsetFill = false
  OffsetIntersection = false
  OffsetJoinType = 0
  OffsetOpenResult = false
  PartialLoad = false
  Refine = true
  Relative = true
  Support = -> [Body013[Fillet001.Face4]]
  _Version = 2
FEATURE [PartDesign::SubShapeBinder] Binder004  label="sk ref nuts"
  BindCopyOnChange = 0
  BindMode = 0
  ClaimChildren = false
  Context = -> Body021 [Binder004.]
  Fuse = false
  MakeFace = true
  OffsetFill = false
  OffsetIntersection = false
  OffsetJoinType = 0
  OffsetOpenResult = false
  PartialLoad = false
  Refine = true
  Relative = true
  Support = -> [Nut003[Face18],Nut002[Face18]]
  _Version = 2
FEATURE [PartDesign::SubShapeBinder] Binder005  label="sk ref relay"
  BindCopyOnChange = 0
  BindMode = 0
  ClaimChildren = false
  Context = -> Body021 [Binder005.]
  Fuse = false
  MakeFace = true
  OffsetFill = false
  OffsetIntersection = false
  OffsetJoinType = 0
  OffsetOpenResult = false
  PartialLoad = false
  Refine = true
  Relative = true
  Support = -> [Compound[Face8,Face9,Face15]]
  _Version = 2
FEATURE [PartDesign::SubShapeBinder] Binder006  label="sk ref ULN2003"
  BindCopyOnChange = 0
  BindMode = 0
  ClaimChildren = false
  Context = -> Body021 [Binder006.]
  Fuse = false
  MakeFace = true
  OffsetFill = false
  OffsetIntersection = false
  OffsetJoinType = 0
  OffsetOpenResult = false
  PartialLoad = false
  Refine = true
  Relative = true
  Support = -> [Body020[Pad021.Face42,Pad021.Face24,Pad021.Face3,Pad021.Face37,Pad021.Face11]]
  _Version = 2
FEATURE [PartDesign::SubShapeBinder] Binder007  label="sk ref ESP32"
  BindCopyOnChange = 0
  BindMode = 0
  ClaimChildren = false
  Context = -> Body021 [Binder007.]
  Fuse = false
  MakeFace = true
  OffsetFill = false
  OffsetIntersection = false
  OffsetJoinType = 0
  OffsetOpenResult = false
  PartialLoad = false
  Refine = true
  Relative = true
  Support = -> [Compound004[Face114,Face113,Face412,Face410,Face5497,Face5496,Edge4629,Edge4648]]
  _Version = 2
FEATURE [PartDesign::SubShapeBinder] Binder008  label="sk ref cable"
  BindCopyOnChange = 0
  BindMode = 0
  ClaimChildren = false
  Context = -> Body021 [Binder008.]
  Fuse = false
  MakeFace = true
  OffsetFill = false
  OffsetIntersection = false
  OffsetJoinType = 0
  OffsetOpenResult = false
  PartialLoad = false
  Refine = true
  Relative = true
  Support = -> [Body015[Sketch038.,Sketch039.]]
  _Version = 2
FEATURE [Sketcher::SketchObject] Sketch106  label="sk right"
  ArcFitTolerance = 1e-06
  AttachmentSupport = -> [YZ_Plane022]
  ExternalGeometry = -> [Binder003,Binder008]
  FullyConstrained = true
  MakeInternals = false
  MapMode = 5
  Placement = pos=(0,0,0) rot=(0.57735,0.57735,0.57735;2.0944rad)
  sketch-geometry (9):
    g0: LineSegment StartX=-30.6 StartY=0 StartZ=0 EndX=-30.6 EndY=-58 EndZ=0
    g1: LineSegment StartX=-30.6 StartY=-58 StartZ=0 EndX=19 EndY=-58 EndZ=0
    g2: LineSegment StartX=30.6 StartY=-46.4 StartZ=0 EndX=30.6 EndY=0 EndZ=0
    g3: LineSegment StartX=30.6 StartY=0 StartZ=0 EndX=28.3 EndY=0 EndZ=0
    g4: LineSegment StartX=-28.3 StartY=1.5 StartZ=0 EndX=-28.3 EndY=0 EndZ=0
    g5: LineSegment StartX=28.3 StartY=0 StartZ=0 EndX=28.3 EndY=1.5 EndZ=0
    g6: LineSegment StartX=28.3 StartY=1.5 StartZ=0 EndX=-28.3 EndY=1.5 EndZ=0
    g7: LineSegment StartX=-28.3 StartY=0 StartZ=0 EndX=-30.6 EndY=0 EndZ=0
    g8: ArcOfCircle CenterX=19 CenterY=-46.4 CenterZ=0 NormalX=0 NormalY=0 NormalZ=1 AngleXU=0 Radius=11.6 StartAngle=4.71239 EndAngle=6.28319
  constraints (22):
    c: Coincident(g0,g1)
    c: Coincident(g2,g3)
    c: Coincident(g7,g0)
    c: Vertical(g0)
    c: Vertical(g2)
    c: Horizontal(g1)
    c: Coincident(g0,g-3)
    c: Coincident(g2,g-4)
    c: Coincident(g5,g6)
    c: Coincident(g6,g4)
    c: Vertical(g4)
    c: Vertical(g5)
    c: Horizontal(g6)
    c: Coincident(g3,g5)
    c: Coincident(g3,g-5)
    c: Coincident(g4,g7)
    c: Coincident(g4,g-6)
    c: DistanceY(g5,g5) = 1.5
    c: Tangent(g1,g8) = -1.5708
    c: Tangent(g2,g8) = -1.5708
    c: DistanceY(g0,g-1) = 58
    c: Distance(g1,g-7) = 3
FEATURE [Sketcher::SketchObject] Sketch107  label="sk front"
  ArcFitTolerance = 1e-06
  AttachmentSupport = -> [XZ_Plane021]
  ExternalGeometry = -> [Binder003,Sketch106]
  FullyConstrained = true
  MakeInternals = false
  MapMode = 5
  Placement = pos=(0,0,0) rot=(1,0,0;1.5708rad)
  sketch-geometry (8):
    g0: LineSegment StartX=-28.3 StartY=1.5 StartZ=0 EndX=-28.3 EndY=0 EndZ=0
    g1: LineSegment StartX=28.3 StartY=0 StartZ=0 EndX=28.3 EndY=1.5 EndZ=0
    g2: LineSegment StartX=28.3 StartY=1.5 StartZ=0 EndX=-28.3 EndY=1.5 EndZ=0
    g3: LineSegment StartX=-30.6 StartY=0 StartZ=0 EndX=-30.6 EndY=-58 EndZ=0
    g4: LineSegment StartX=-30.6 StartY=-58 StartZ=0 EndX=30.6 EndY=-58 EndZ=0
    g5: LineSegment StartX=30.6 StartY=-58 StartZ=0 EndX=30.6 EndY=0 EndZ=0
    g6: LineSegment StartX=30.6 StartY=0 StartZ=0 EndX=28.3 EndY=0 EndZ=0
    g7: LineSegment StartX=-28.3 StartY=0 StartZ=0 EndX=-30.6 EndY=0 EndZ=0
  constraints (20):
    c: Coincident(g1,g2)
    c: Coincident(g2,g0)
    c: Vertical(g0)
    c: Vertical(g1)
    c: Horizontal(g2)
    c: Coincident(g3,g4)
    c: Coincident(g4,g5)
    c: Coincident(g5,g6)
    c: Coincident(g7,g3)
    c: Vertical(g3)
    c: Vertical(g5)
    c: Horizontal(g4)
    c: Coincident(g3,g-3)
    c: PointOnObject(g-8,g4)
    c: Coincident(g1,g6)
    c: Coincident(g0,g7)
    c: Coincident(g0,g-4)
    c: Coincident(g1,g-5)
    c: Coincident(g5,g-6)
    c: PointOnObject(g-7,g2)
FEATURE [Sketcher::SketchObject] Sketch108  label="sk relay slot"
  ArcFitTolerance = 1e-06
  AttachmentSupport = -> [XZ_Plane021]
  ExternalGeometry = -> [Binder005]
  FullyConstrained = true
  MakeInternals = false
  MapMode = 5
  Placement = pos=(0,0,0) rot=(1,0,0;1.5708rad)
  sketch-geometry (14):
    g0: LineSegment StartX=-5.1 StartY=-0.7 StartZ=0 EndX=-5.1 EndY=-18.15 EndZ=0
    g1: LineSegment StartX=-5.1 StartY=-22.5 StartZ=0 EndX=11.1 EndY=-22.5 EndZ=0
    g2: LineSegment StartX=11.1 StartY=-22.5 StartZ=0 EndX=11.1 EndY=-20.25 EndZ=0
    g3: LineSegment StartX=11.1 StartY=-0.7 StartZ=0 EndX=-5.1 EndY=-0.7 EndZ=0
    g4: LineSegment StartX=-6.05 StartY=-18.15 StartZ=0 EndX=-6.05 EndY=-20.25 EndZ=0
    g5: LineSegment StartX=-6.05 StartY=-20.25 StartZ=0 EndX=-5.1 EndY=-20.25 EndZ=0
    g6: LineSegment StartX=12.05 StartY=-20.25 StartZ=0 EndX=12.05 EndY=-18.15 EndZ=0
    g7: LineSegment StartX=12.05 StartY=-18.15 StartZ=0 EndX=11.1 EndY=-18.15 EndZ=0
    g8: Circle [constr] CenterX=11.8 CenterY=-18.4 CenterZ=0 NormalX=0 NormalY=0 NormalZ=1 AngleXU=0 Radius=0.25
    g9: Circle [constr] CenterX=-5.8 CenterY=-20 CenterZ=0 NormalX=0 NormalY=0 NormalZ=1 AngleXU=0 Radius=0.25
    g10: LineSegment StartX=-5.1 StartY=-18.15 StartZ=0 EndX=-6.05 EndY=-18.15 EndZ=0
    g11: LineSegment StartX=11.1 StartY=-20.25 StartZ=0 EndX=12.05 EndY=-20.25 EndZ=0
    g12: LineSegment StartX=-5.1 StartY=-20.25 StartZ=0 EndX=-5.1 EndY=-22.5 EndZ=0
    g13: LineSegment StartX=11.1 StartY=-18.15 StartZ=0 EndX=11.1 EndY=-0.7 EndZ=0
  constraints (42):
    c: Coincident(g12,g1)
    c: Coincident(g1,g2)
    c: Coincident(g13,g3)
    c: Coincident(g3,g0)
    c: Vertical(g0)
    c: Vertical(g2)
    c: Horizontal(g1)
    c: Horizontal(g3)
    c: Coincident(g4,g5)
    c: Coincident(g11,g6)
    c: Coincident(g6,g7)
    c: Coincident(g10,g4)
    c: Vertical(g4)
    c: Vertical(g6)
    c: Horizontal(g5)
    c: Horizontal(g7)
    c: DistanceX(g-5,g13) = 0.5
    c: DistanceX(g0,g-5) = 0.5
    c: DistanceY(g-5,g0) = 2
    c: Coincident(g8,g-3)
    c: Coincident(g9,g-4)
    c: Tangent(g5,g9)
    c: Tangent(g9,g4)
    c: Tangent(g8,g6)
    c: Tangent(g8,g7)
    c: DistanceX(g8,g6) = 0.25
    c: Equal(g8,g9)
    c: PointOnObject(g7,g13)
    c: Coincident(g0,g10)
    c: PointOnObject(g5,g12)
    c: PointOnObject(g12,g5)
    c: DistanceY(g1,g-4) = 2.5
    c: PointOnObject(g13,g7)
    c: Coincident(g2,g11)
    c: PointOnObject(g0,g7)
    c: PointOnObject(g5,g11)
    c: PointOnObject(g5,g0)
    c: Vertical(g12)
    c: Horizontal(g10)
    c: Vertical(g13)
    c: Horizontal(g11)
    c: PointOnObject(g2,g13)
FEATURE [Sketcher::SketchObject] Sketch109  label="sk ULN2003 slot"
  ArcFitTolerance = 1e-06
  AttachmentSupport = -> [XZ_Plane021]
  ExternalGeometry = -> [Binder006]
  FullyConstrained = true
  MakeInternals = false
  MapMode = 5
  Placement = pos=(0,0,0) rot=(1,0,0;1.5708rad)
  sketch-geometry (14):
    g0: Circle [constr] CenterX=17.35 CenterY=-39.2 CenterZ=0 NormalX=0 NormalY=0 NormalZ=1 AngleXU=0 Radius=0.125
    g1: Circle [constr] CenterX=-17.35 CenterY=-41 CenterZ=0 NormalX=0 NormalY=0 NormalZ=1 AngleXU=0 Radius=0.125
    g2: LineSegment StartX=-17.475 StartY=-39.075 StartZ=0 EndX=-17.475 EndY=-41.125 EndZ=0
    g3: LineSegment StartX=-17.475 StartY=-41.125 StartZ=0 EndX=-15.975 EndY=-41.125 EndZ=0
    g4: LineSegment StartX=17.475 StartY=-41.125 StartZ=0 EndX=17.475 EndY=-39.075 EndZ=0
    g5: LineSegment StartX=17.475 StartY=-39.075 StartZ=0 EndX=15.975 EndY=-39.075 EndZ=0
    g6: LineSegment StartX=15.975 StartY=-25.4 StartZ=0 EndX=-15.975 EndY=-25.4 EndZ=0
    g7: LineSegment StartX=-15.975 StartY=-25.4 StartZ=0 EndX=-15.975 EndY=-39.075 EndZ=0
    g8: LineSegment StartX=-15.975 StartY=-43.625 StartZ=0 EndX=15.975 EndY=-43.625 EndZ=0
    g9: LineSegment StartX=15.975 StartY=-43.625 StartZ=0 EndX=15.975 EndY=-41.125 EndZ=0
    g10: LineSegment StartX=-15.975 StartY=-39.075 StartZ=0 EndX=-17.475 EndY=-39.075 EndZ=0
    g11: LineSegment StartX=-15.975 StartY=-41.125 StartZ=0 EndX=-15.975 EndY=-43.625 EndZ=0
    g12: LineSegment StartX=15.975 StartY=-39.075 StartZ=0 EndX=15.975 EndY=-25.4 EndZ=0
    g13: LineSegment StartX=15.975 StartY=-41.125 StartZ=0 EndX=17.475 EndY=-41.125 EndZ=0
  constraints (42):
    c: Coincident(g0,g-3)
    c: Coincident(g1,g-4)
    c: Coincident(g2,g3)
    c: Coincident(g13,g4)
    c: Coincident(g4,g5)
    c: Coincident(g10,g2)
    c: Vertical(g2)
    c: Vertical(g4)
    c: Horizontal(g3)
    c: Horizontal(g5)
    c: Tangent(g0,g4)
    c: Tangent(g0,g5)
    c: Tangent(g1,g3)
    c: Tangent(g1,g2)
    c: Diameter(g0) = 0.25
    c: Coincident(g6,g7)
    c: Coincident(g11,g8)
    c: Coincident(g8,g9)
    c: Coincident(g12,g6)
    c: Horizontal(g6)
    c: Horizontal(g8)
    c: Vertical(g7)
    c: Vertical(g9)
    c: PointOnObject(g5,g12)
    c: Coincident(g7,g10)
    c: PointOnObject(g12,g5)
    c: PointOnObject(g9,g13)
    c: Coincident(g3,g11)
    c: PointOnObject(g13,g9)
    c: Equal(g0,g1)
    c: Vertical(g11)
    c: PointOnObject(g3,g7)
    c: Horizontal(g10)
    c: PointOnObject(g7,g5)
    c: Horizontal(g13)
    c: PointOnObject(g4,g3)
    c: PointOnObject(g9,g12)
    c: Vertical(g12)
    c: Distance(g5,g5) = 1.5
    c: Equal(g10,g5)
    c: DistanceY(g9,g9) = 2.5
    c: Distance(g-5,g6) = 2
FEATURE [Sketcher::SketchObject] Sketch110  label="sk separation"
  ArcFitTolerance = 1e-06
  AttachmentSupport = -> [YZ_Plane022]
  ExternalGeometry = -> [Sketch106]
  FullyConstrained = true
  MakeInternals = false
  MapMode = 5
  Placement = pos=(0,0,0) rot=(0.57735,0.57735,0.57735;2.0944rad)
  sketch-geometry (5):
    g0: LineSegment StartX=15.85 StartY=0 StartZ=0 EndX=15.85 EndY=-58 EndZ=0
    g1: LineSegment StartX=15.85 StartY=-58 StartZ=0 EndX=16.15 EndY=-58 EndZ=0
    g2: LineSegment StartX=16.15 StartY=-58 StartZ=0 EndX=16.15 EndY=0 EndZ=0
    g3: LineSegment StartX=16.15 StartY=0 StartZ=0 EndX=15.85 EndY=0 EndZ=0
    g4: GeomPoint X=16 Y=0 Z=0
  constraints (13):
    c: Coincident(g0,g1)
    c: Coincident(g1,g2)
    c: Coincident(g2,g3)
    c: Coincident(g3,g0)
    c: Vertical(g0)
    c: Vertical(g2)
    c: Horizontal(g1)
    c: Horizontal(g3)
    c: PointOnObject(g0,g-1)
    c: Distance(g3,g3) = 0.3
    c: Symmetric(g0,g2,g4)
    c: DistanceX(g-1,g4) = 16
    c: PointOnObject(g0,g-3)
FEATURE [Sketcher::SketchObject] Sketch111  label="sk ULN2003 slot depth"
  ArcFitTolerance = 1e-06
  AttachmentSupport = -> [YZ_Plane022]
  ExternalGeometry = -> [Sketch109,Sketch110]
  FullyConstrained = true
  MakeInternals = false
  MapMode = 5
  Placement = pos=(0,0,0) rot=(0.57735,0.57735,0.57735;2.0944rad)
  sketch-geometry (3):
    g0: LineSegment StartX=-17.5 StartY=-41.125 StartZ=0 EndX=16 EndY=-41.125 EndZ=0
    g1: GeomPoint X=15.85 Y=-41.125 Z=0
    g2: GeomPoint X=16.15 Y=-41.125 Z=0
  constraints (7):
    c: Horizontal(g0)
    c: PointOnObject(g-3,g0)
    c: DistanceX(g0,g-1) = 17.5
    c: PointOnObject(g1,g-5)
    c: PointOnObject(g2,g-6)
    c: Symmetric(g1,g2,g0)
    c: PointOnObject(g1,g0)
FEATURE [Sketcher::SketchObject] Sketch112  label="sk relay slot depth"
  ArcFitTolerance = 1e-06
  AttachmentSupport = -> [YZ_Plane022]
  ExternalGeometry = -> [Sketch108,Sketch110]
  FullyConstrained = true
  MakeInternals = false
  MapMode = 5
  Placement = pos=(0,0,0) rot=(0.57735,0.57735,0.57735;2.0944rad)
  sketch-geometry (3):
    g0: LineSegment StartX=-28.5 StartY=-20.25 StartZ=0 EndX=16 EndY=-20.25 EndZ=0
    g1: GeomPoint X=15.85 Y=-20.25 Z=0
    g2: GeomPoint X=16.15 Y=-20.25 Z=0
  constraints (7):
    c: Horizontal(g0)
    c: PointOnObject(g-3,g0)
    c: PointOnObject(g1,g-4)
    c: PointOnObject(g2,g-5)
    c: Symmetric(g1,g2,g0)
    c: PointOnObject(g1,g0)
    c: DistanceX(g0,g-1) = 28.5
FEATURE [PartDesign::Body] Body021  label="Skeleton"
  AllowCompound = false
  Group = -> [Binder003,Binder004,Binder005,Binder006,Binder007,Binder008,Sketch106,Sketch107,Sketch108,Sketch109,Sketch110,Sketch111,Sketch112]
  Origin = -> Origin021
